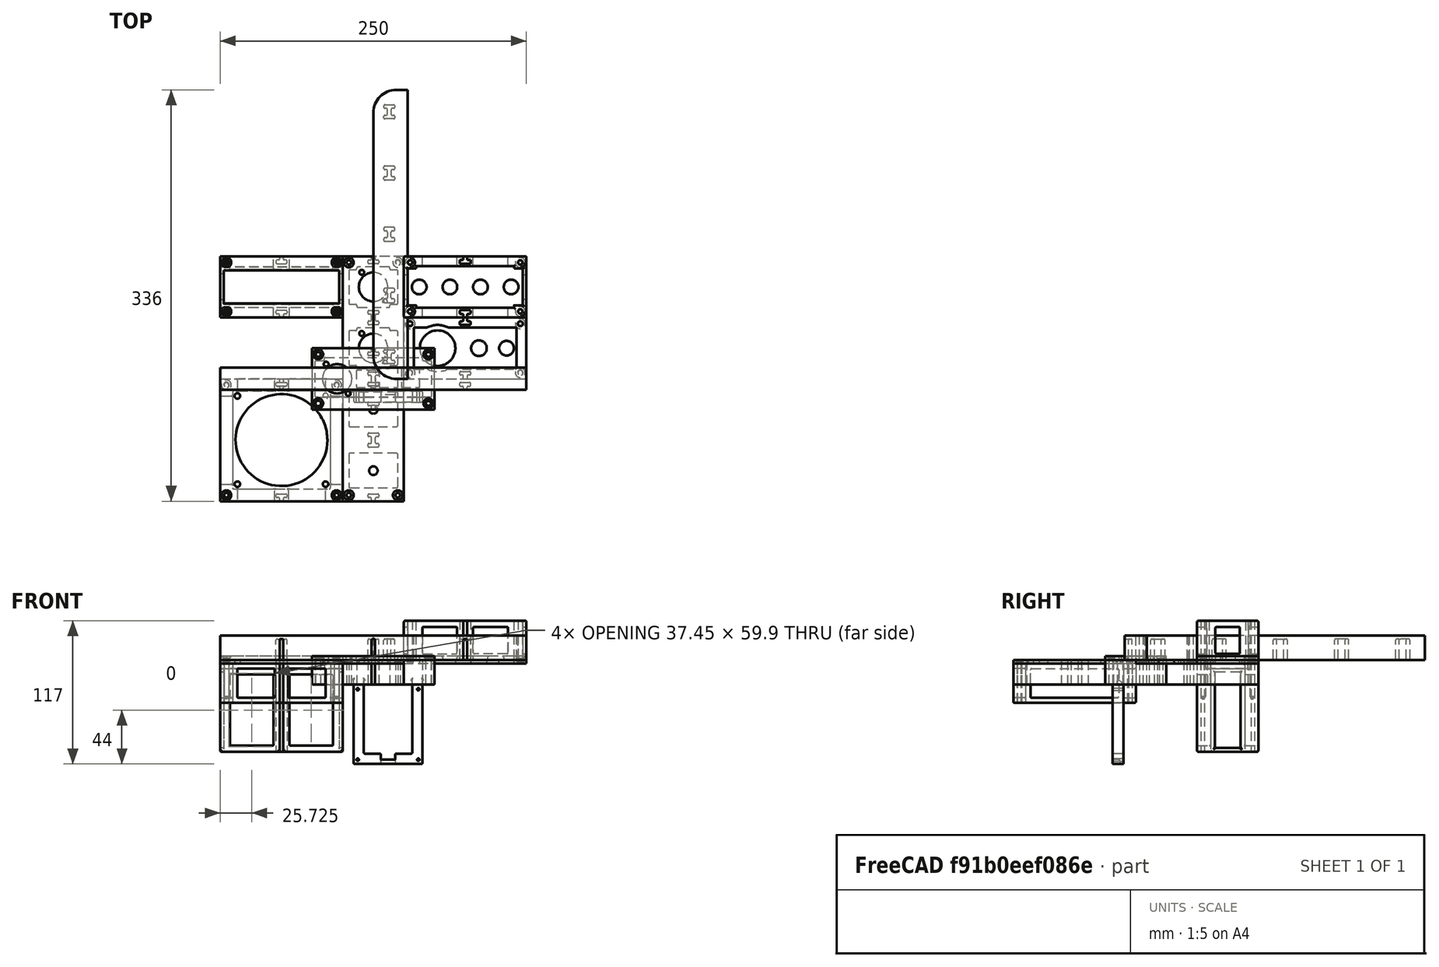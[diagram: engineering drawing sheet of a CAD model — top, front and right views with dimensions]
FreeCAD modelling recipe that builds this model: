
FCSTD DOCUMENT  (FreeCAD 1.2R20260106 (Git shallow))
Label: Rack
License: All rights reserved
LicenseURL: https://en.wikipedia.org/wiki/All_rights_reserved
objects: Sketcher::SketchObject×46, PartDesign::Pocket×35, PartDesign::Pad×20, App::Link×20, PartDesign::Fillet×19, App::Point×15, PartDesign::Body×14, PartDesign::Hole×13, PartDesign::SubShapeBinder×12, App::FeaturePython×3, Assembly::JointGroup×1, Assembly::SimulationGroup×1, Assembly::AssemblyObject×1
note: 379 computed .brp shape members not serialized (recipe doc carries the construction recipe); baked Part::Feature solids carry a one-line shape summary decoded from their .brp
EXTERNAL_REF file=Joints.FCStd obj=Body003
EXTERNAL_REF file=Joints.FCStd obj=Body001
EXTERNAL_REF file=Joints.FCStd obj=Body005
EXTERNAL_REF file=Joints.FCStd obj=Body004

FEATURE [Sketcher::SketchObject] Sketch  label="Master Sketch"
  ArcFitTolerance = 1e-06
  ExternalTypes = [0]
  FullyConstrained = true
  MakeInternals = false
  MapMode = 5
  sketch-geometry (103):
    g0: LineSegment StartX=-125 StartY=100 StartZ=0 EndX=-125 EndY=50 EndZ=0
    g1: LineSegment StartX=-125 StartY=50 StartZ=0 EndX=-25 EndY=50 EndZ=0
    g2: LineSegment StartX=-25 StartY=50 StartZ=0 EndX=-25 EndY=100 EndZ=0
    g3: LineSegment StartX=-25 StartY=100 StartZ=0 EndX=-125 EndY=100 EndZ=0
    g4: LineSegment StartX=-25 StartY=100 StartZ=0 EndX=-25 EndY=-100 EndZ=0
    g5: LineSegment StartX=-25 StartY=-100 StartZ=0 EndX=25 EndY=-100 EndZ=0
    g6: LineSegment StartX=25 StartY=-100 StartZ=0 EndX=25 EndY=100 EndZ=0
    g7: LineSegment StartX=25 StartY=100 StartZ=0 EndX=-25 EndY=100 EndZ=0
    g8: LineSegment StartX=25 StartY=100 StartZ=0 EndX=25 EndY=50 EndZ=0
    g9: LineSegment StartX=25 StartY=50 StartZ=0 EndX=125 EndY=50 EndZ=0
    g10: LineSegment StartX=125 StartY=50 StartZ=0 EndX=125 EndY=100 EndZ=0
    g11: LineSegment StartX=125 StartY=100 StartZ=0 EndX=25 EndY=100 EndZ=0
    g12: LineSegment StartX=-25 StartY=50 StartZ=0 EndX=-125 EndY=50 EndZ=0
    g13: LineSegment StartX=-125 StartY=50 StartZ=0 EndX=-125 EndY=7.1e-15 EndZ=0
    g14: LineSegment StartX=-125 StartY=7.1e-15 StartZ=0 EndX=-25 EndY=7.1e-15 EndZ=0
    g15: LineSegment StartX=-25 StartY=7.1e-15 StartZ=0 EndX=-25 EndY=50 EndZ=0
    g16: LineSegment StartX=125 StartY=50 StartZ=0 EndX=25 EndY=50 EndZ=0
    g17: LineSegment StartX=25 StartY=50 StartZ=0 EndX=25 EndY=7.1e-15 EndZ=0
    g18: LineSegment StartX=25 StartY=7.1e-15 StartZ=0 EndX=125 EndY=7.1e-15 EndZ=0
    g19: LineSegment StartX=125 StartY=7.1e-15 StartZ=0 EndX=125 EndY=50 EndZ=0
    g20: LineSegment StartX=-125 StartY=7.1e-15 StartZ=0 EndX=-125 EndY=-50 EndZ=0
    g21: LineSegment StartX=125 StartY=-50 StartZ=0 EndX=125 EndY=7.1e-15 EndZ=0
    g22: LineSegment StartX=125 StartY=-50 StartZ=0 EndX=25 EndY=-50 EndZ=0
    g23: LineSegment StartX=25 StartY=-50 StartZ=0 EndX=25 EndY=-100 EndZ=0
    g24: LineSegment StartX=-125 StartY=-50 StartZ=0 EndX=-125 EndY=-100 EndZ=0
    g25: LineSegment StartX=-125 StartY=-100 StartZ=0 EndX=-25 EndY=-100 EndZ=0
    g26: LineSegment StartX=-25 StartY=-100 StartZ=0 EndX=-25 EndY=-50 EndZ=0
    g27: LineSegment StartX=-25 StartY=-50 StartZ=0 EndX=-125 EndY=-50 EndZ=0
    g28: LineSegment StartX=125 StartY=-50 StartZ=0 EndX=25 EndY=-50 EndZ=0
    g29: LineSegment StartX=25 StartY=-50 StartZ=0 EndX=25 EndY=-100 EndZ=0
    g30: LineSegment StartX=25 StartY=-100 StartZ=0 EndX=125 EndY=-100 EndZ=0
    g31: LineSegment StartX=125 StartY=-100 StartZ=0 EndX=125 EndY=-50 EndZ=0
    g32: Circle CenterX=-120 CenterY=95 CenterZ=0 NormalX=0 NormalY=0 NormalZ=1 AngleXU=0 Radius=0.825
    g33: Circle CenterX=-30 CenterY=55 CenterZ=0 NormalX=0 NormalY=0 NormalZ=1 AngleXU=0 Radius=0.825
    g34: Circle CenterX=-30 CenterY=95 CenterZ=0 NormalX=0 NormalY=0 NormalZ=1 AngleXU=0 Radius=0.825
    g35: Circle CenterX=-120 CenterY=55 CenterZ=0 NormalX=0 NormalY=0 NormalZ=1 AngleXU=0 Radius=0.825
    g36: LineSegment [constr] StartX=-120 StartY=95 StartZ=0 EndX=-120 EndY=55 EndZ=0
    g37: LineSegment [constr] StartX=-120 StartY=55 StartZ=0 EndX=-30 EndY=55 EndZ=0
    g38: LineSegment [constr] StartX=-30 StartY=55 StartZ=0 EndX=-30 EndY=95 EndZ=0
    g39: LineSegment [constr] StartX=-30 StartY=95 StartZ=0 EndX=-120 EndY=95 EndZ=0
    g40: LineSegment [constr] StartX=-120 StartY=-5 StartZ=0 EndX=-120 EndY=-95 EndZ=0
    g41: LineSegment [constr] StartX=-120 StartY=-95 StartZ=0 EndX=-30 EndY=-95 EndZ=0
    g42: LineSegment [constr] StartX=-30 StartY=-95 StartZ=0 EndX=-30 EndY=-5 EndZ=0
    g43: LineSegment [constr] StartX=-30 StartY=-5 StartZ=0 EndX=-120 EndY=-5 EndZ=0
    g44: Circle CenterX=-120 CenterY=-5 CenterZ=0 NormalX=0 NormalY=0 NormalZ=1 AngleXU=0 Radius=0.825
    g45: Circle CenterX=-30 CenterY=-5 CenterZ=0 NormalX=0 NormalY=0 NormalZ=1 AngleXU=0 Radius=0.825
    g46: Circle CenterX=-30 CenterY=-95 CenterZ=0 NormalX=0 NormalY=0 NormalZ=1 AngleXU=0 Radius=0.825
    g47: Circle CenterX=-120 CenterY=-95 CenterZ=0 NormalX=0 NormalY=0 NormalZ=1 AngleXU=0 Radius=0.825
    g48: LineSegment StartX=-115 StartY=-10 StartZ=0 EndX=-115 EndY=-90 EndZ=0
    g49: LineSegment StartX=-115 StartY=-90 StartZ=0 EndX=-35 EndY=-90 EndZ=0
    g50: LineSegment StartX=-35 StartY=-90 StartZ=0 EndX=-35 EndY=-10 EndZ=0
    g51: LineSegment StartX=-35 StartY=-10 StartZ=0 EndX=-115 EndY=-10 EndZ=0
    g52: GeomPoint X=-75 Y=-50 Z=0
    g53: GeomPoint X=-75 Y=-50 Z=0
    g54: LineSegment [constr] StartX=-111 StartY=-14 StartZ=0 EndX=-111 EndY=-86 EndZ=0
    g55: LineSegment [constr] StartX=-111 StartY=-86 StartZ=0 EndX=-39 EndY=-86 EndZ=0
    g56: LineSegment [constr] StartX=-39 StartY=-86 StartZ=0 EndX=-39 EndY=-14 EndZ=0
    g57: LineSegment [constr] StartX=-39 StartY=-14 StartZ=0 EndX=-111 EndY=-14 EndZ=0
    g58: Circle CenterX=-111 CenterY=-14 CenterZ=0 NormalX=0 NormalY=0 NormalZ=1 AngleXU=0 Radius=2
    g59: Circle CenterX=-39 CenterY=-14 CenterZ=0 NormalX=0 NormalY=0 NormalZ=1 AngleXU=0 Radius=2
    g60: Circle CenterX=-39 CenterY=-86 CenterZ=0 NormalX=0 NormalY=0 NormalZ=1 AngleXU=0 Radius=2
    g61: Circle CenterX=-111 CenterY=-86 CenterZ=0 NormalX=0 NormalY=0 NormalZ=1 AngleXU=0 Radius=2
    g62: Circle CenterX=-75 CenterY=-50 CenterZ=0 NormalX=0 NormalY=0 NormalZ=1 AngleXU=0 Radius=37.5
    g63: GeomPoint X=75 Y=75 Z=0
    g64: LineSegment [constr] StartX=30 StartY=55 StartZ=0 EndX=120 EndY=55 EndZ=0
    g65: LineSegment [constr] StartX=120 StartY=55 StartZ=0 EndX=120 EndY=95 EndZ=0
    g66: LineSegment [constr] StartX=120 StartY=95 StartZ=0 EndX=30 EndY=95 EndZ=0
    g67: LineSegment [constr] StartX=30 StartY=95 StartZ=0 EndX=30 EndY=55 EndZ=0
    g68: GeomPoint [constr] X=75 Y=75 Z=0
    g69: Circle CenterX=30 CenterY=95 CenterZ=0 NormalX=0 NormalY=0 NormalZ=1 AngleXU=0 Radius=0.825
    g70: Circle CenterX=120 CenterY=95 CenterZ=0 NormalX=0 NormalY=0 NormalZ=1 AngleXU=0 Radius=0.825
    g71: Circle CenterX=120 CenterY=55 CenterZ=0 NormalX=0 NormalY=0 NormalZ=1 AngleXU=0 Radius=0.825
    g72: Circle CenterX=30 CenterY=55 CenterZ=0 NormalX=0 NormalY=0 NormalZ=1 AngleXU=0 Radius=0.825
    g73: Circle CenterX=37.5 CenterY=75 CenterZ=0 NormalX=0 NormalY=0 NormalZ=1 AngleXU=0 Radius=6
    g74: LineSegment [constr] StartX=30 StartY=75 StartZ=0 EndX=120 EndY=75 EndZ=0
    g75: Circle CenterX=62.5 CenterY=75 CenterZ=0 NormalX=0 NormalY=0 NormalZ=1 AngleXU=0 Radius=6
    g76: Circle CenterX=87.5 CenterY=75 CenterZ=0 NormalX=0 NormalY=0 NormalZ=1 AngleXU=0 Radius=6
    g77: Circle CenterX=112.5 CenterY=75 CenterZ=0 NormalX=0 NormalY=0 NormalZ=1 AngleXU=0 Radius=6
    g78: LineSegment [constr] StartX=62.5 StartY=55 StartZ=0 EndX=87.5 EndY=55 EndZ=0
    g79: LineSegment [constr] StartX=87.5 StartY=55 StartZ=0 EndX=87.5 EndY=95 EndZ=0
    g80: LineSegment [constr] StartX=87.5 StartY=95 StartZ=0 EndX=62.5 EndY=95 EndZ=0
    g81: LineSegment [constr] StartX=62.5 StartY=95 StartZ=0 EndX=62.5 EndY=55 EndZ=0
    g82: GeomPoint [constr] X=75 Y=75 Z=0
    g83: GeomPoint [constr] X=75 Y=25 Z=0
    g84: LineSegment StartX=30 StartY=5 StartZ=0 EndX=120 EndY=5 EndZ=0
    g85: LineSegment StartX=120 StartY=5 StartZ=0 EndX=120 EndY=45 EndZ=0
    g86: LineSegment StartX=120 StartY=45 StartZ=0 EndX=30 EndY=45 EndZ=0
    g87: LineSegment StartX=30 StartY=45 StartZ=0 EndX=30 EndY=5 EndZ=0
    g88: GeomPoint [constr] X=75 Y=25 Z=0
    g89: LineSegment [constr] StartX=75 StartY=25 StartZ=0 EndX=120 EndY=25 EndZ=0
    g90: LineSegment [constr] StartX=75 StartY=25 StartZ=0 EndX=30 EndY=25 EndZ=0
    g91: LineSegment [constr] StartX=75 StartY=25 StartZ=0 EndX=75 EndY=5 EndZ=0
    g92: LineSegment [constr] StartX=75 StartY=25 StartZ=0 EndX=75 EndY=45 EndZ=0
    g93: Circle CenterX=52.5 CenterY=25 CenterZ=0 NormalX=0 NormalY=0 NormalZ=1 AngleXU=0 Radius=14.5
    g94: Circle CenterX=86.25 CenterY=25 CenterZ=0 NormalX=0 NormalY=0 NormalZ=1 AngleXU=0 Radius=6.375
    g95: Circle CenterX=108.75 CenterY=25 CenterZ=0 NormalX=0 NormalY=0 NormalZ=1 AngleXU=0 Radius=6
    g96: GeomPoint [constr] X=97.5 Y=25 Z=0
    g97: LineSegment [constr] StartX=97.5 StartY=25 StartZ=0 EndX=97.5 EndY=45 EndZ=0
    g98: GeomPoint [constr] X=86.25 Y=35 Z=0
    g99: LineSegment [constr] StartX=86.25 StartY=35 StartZ=0 EndX=86.25 EndY=25 EndZ=0
    g100: GeomPoint [constr] X=108.75 Y=35 Z=0
    g101: LineSegment [constr] StartX=108.75 StartY=35 StartZ=0 EndX=108.75 EndY=25 EndZ=0
    g102: GeomPoint [constr] X=52.5 Y=25 Z=0
  constraints (255):
    c: Coincident(g0,g1)
    c: Coincident(g1,g2)
    c: Coincident(g2,g3)
    c: Coincident(g3,g0)
    c: Vertical(g0)
    c: Vertical(g2)
    c: Horizontal(g1)
    c: Horizontal(g3)
    c: DistanceX(g3,g3) = 100
    c: DistanceY(g0,g0) = 50
    c: Coincident(g4,g5)
    c: Coincident(g5,g6)
    c: Coincident(g6,g7)
    c: Coincident(g7,g4)
    c: Vertical(g4)
    c: Vertical(g6)
    c: Horizontal(g5)
    c: Horizontal(g7)
    c: DistanceY(g6,g6) = 200
    c: DistanceX(g7,g7) = 50
    c: Symmetric(g6,g4,g-1)
    c: Coincident(g2,g4)
    c: Coincident(g8,g9)
    c: Coincident(g9,g10)
    c: Coincident(g10,g11)
    c: Coincident(g11,g8)
    c: Vertical(g8)
    c: Vertical(g10)
    c: Horizontal(g9)
    c: Horizontal(g11)
    c: Coincident(g8,g6)
    c: Equal(g3,g11)
    c: Equal(g0,g10)
    c: Coincident(g12,g13)
    c: Coincident(g13,g14)
    c: Coincident(g14,g15)
    c: Coincident(g15,g12)
    c: Horizontal(g12)
    c: Horizontal(g14)
    c: Vertical(g13)
    c: Vertical(g15)
    c: Coincident(g12,g1)
    c: Equal(g14,g1)
    c: Equal(g13,g0)
    c: Coincident(g16,g17)
    c: Coincident(g17,g18)
    c: Coincident(g18,g19)
    c: Coincident(g19,g16)
    c: Horizontal(g16)
    c: Horizontal(g18)
    c: Vertical(g17)
    c: Vertical(g19)
    c: Coincident(g16,g9)
    c: Equal(g0,g19)
    c: Equal(g14,g18)
    c: Vertical(g20)
    c: Coincident(g20,g13)
    c: Equal(g20,g13)
    c: Vertical(g21)
    c: Coincident(g21,g18)
    c: Coincident(g22,g23)
    c: Horizontal(g22)
    c: Vertical(g23)
    c: Coincident(g22,g21)
    c: Coincident(g23,g5)
    c: Equal(g21,g20)
    c: Coincident(g24,g25)
    c: Coincident(g25,g26)
    c: Coincident(g26,g27)
    c: Coincident(g27,g24)
    c: Vertical(g24)
    c: Vertical(g26)
    c: Horizontal(g25)
    c: Horizontal(g27)
    c: Coincident(g24,g20)
    c: PointOnObject(g25,g4)
    c: Coincident(g28,g29)
    c: Coincident(g29,g30)
    c: Coincident(g30,g31)
    c: Coincident(g31,g28)
    c: Horizontal(g28)
    c: Horizontal(g30)
    c: Vertical(g29)
    c: Vertical(g31)
    c: Coincident(g28,g21)
    c: PointOnObject(g29,g6)
    c: Equal(g31,g21)
    c: Equal(g24,g20)
    c: Diameter(g32) = 1.65
    c: Equal(g32,g34)
    c: Equal(g34,g35)
    c: Equal(g35,g33)
    c: Coincident(g36,g37)
    c: Coincident(g37,g38)
    c: Coincident(g38,g39)
    c: Coincident(g39,g36)
    c: Vertical(g36)
    c: Vertical(g38)
    c: Horizontal(g37)
    c: Horizontal(g39)
    c: Coincident(g36,g32)
    c: Coincident(g36,g35)
    c: Coincident(g37,g33)
    c: Coincident(g38,g34)
    c: Distance(g39,g3) = 5
    c: Distance(g0,g36) = 5
    c: Distance(g1,g37) = 5
    c: Distance(g2,g38) = 5
    c: Coincident(g40,g41)
    c: Coincident(g41,g42)
    c: Coincident(g42,g43)
    c: Coincident(g43,g40)
    c: Vertical(g40)
    c: Vertical(g42)
    c: Horizontal(g41)
    c: Horizontal(g43)
    c: Equal(g43,g39)
    c: Distance(g43,g14) = 5
    c: Distance(g20,g40) = 5
    c: Diameter(g44) = 1.65
    c: Coincident(g44,g40)
    c: Coincident(g45,g42)
    c: Coincident(g46,g41)
    c: Coincident(g47,g40)
    c: Equal(g45,g44)
    c: Equal(g46,g45)
    c: Equal(g47,g46)
    c: Coincident(g48,g49)
    c: Coincident(g49,g50)
    c: Coincident(g50,g51)
    c: Coincident(g51,g48)
    c: Vertical(g48)
    c: Vertical(g50)
    c: Horizontal(g49)
    c: Horizontal(g51)
    c: DistanceX(g51,g51) = 80
    c: Equal(g51,g50)
    c: Distance(g25,g41) = 5
    c: Symmetric(g40,g42,g52)
    c: Symmetric(g48,g50,g53)
    c: Coincident(g52,g53)
    c: Coincident(g54,g55)
    c: Coincident(g55,g56)
    c: Coincident(g56,g57)
    c: Coincident(g57,g54)
    c: Vertical(g54)
    c: Vertical(g56)
    c: Horizontal(g55)
    c: Horizontal(g57)
    c: Distance(g51,g57) = 4
    c: Distance(g48,g54) = 4
    c: Distance(g50,g56) = 4
    c: Distance(g55,g49) = 4
    c: Diameter(g58) = 4
    c: Coincident(g58,g54)
    c: Coincident(g59,g56)
    c: Coincident(g60,g55)
    c: Coincident(g61,g54)
    c: Equal(g58,g59)
    c: Equal(g60,g61)
    c: Equal(g60,g59)
    c: Diameter(g62) = 75
    c: Coincident(g62,g52)
    c: Symmetric(g8,g10,g63)
    c: Coincident(g64,g65)
    c: Coincident(g65,g66)
    c: Coincident(g66,g67)
    c: Coincident(g67,g64)
    c: Horizontal(g64)
    c: Horizontal(g66)
    c: Vertical(g65)
    c: Vertical(g67)
    c: Symmetric(g66,g64,g68)
    c: Coincident(g68,g63)
    c: Distance(g11,g66) = 5
    c: Distance(g10,g65) = 5
    c: Coincident(g69,g66)
    c: Equal(g69,g34)
    c: Coincident(g70,g65)
    c: Coincident(g71,g64)
    c: Coincident(g72,g64)
    c: Equal(g69,g70)
    c: Equal(g70,g71)
    c: Equal(g72,g71)
    c: Diameter(g73) = 12
    c: Horizontal(g74)
    c: PointOnObject(g63,g74)
    c: PointOnObject(g74,g67)
    c: PointOnObject(g74,g65)
    c: PointOnObject(g73,g74)
    c: Diameter(g75) = 12
    c: Diameter(g76) = 12
    c: Diameter(g77) = 12
    c: DistanceX(g73,g75) = 25
    c: DistanceX(g76,g77) = 25
    c: PointOnObject(g75,g74)
    c: PointOnObject(g76,g74)
    c: PointOnObject(g77,g74)
    c: Coincident(g78,g79)
    c: Coincident(g79,g80)
    c: Coincident(g80,g81)
    c: Coincident(g81,g78)
    c: Horizontal(g78)
    c: Horizontal(g80)
    c: Vertical(g79)
    c: Vertical(g81)
    c: Symmetric(g80,g78,g82)
    c: Coincident(g82,g63)
    c: DistanceX(g80,g80) = 25
    c: PointOnObject(g75,g81)
    c: PointOnObject(g76,g79)
    c: PointOnObject(g78,g64)
    c: Symmetric(g17,g9,g83)
    c: Coincident(g84,g85)
    c: Coincident(g85,g86)
    c: Coincident(g86,g87)
    c: Coincident(g87,g84)
    c: Horizontal(g84)
    c: Horizontal(g86)
    c: Vertical(g85)
    c: Vertical(g87)
    c: Symmetric(g86,g84,g88)
    c: Coincident(g88,g83)
    c: Equal(g86,g64)
    c: Equal(g85,g65)
    c: Coincident(g89,g83)
    c: Horizontal(g89)
    c: PointOnObject(g89,g85)
    c: Coincident(g90,g83)
    c: Horizontal(g90)
    c: PointOnObject(g90,g87)
    c: Coincident(g91,g83)
    c: Symmetric(g84,g84,g91)
    c: Coincident(g92,g83)
    c: Vertical(g92)
    c: PointOnObject(g92,g86)
    c: Diameter(g93) = 29
    c: Diameter(g94) = 12.75
    c: Diameter(g95) = 12
    c: Symmetric(g91,g85,g96)
    c: Coincident(g97,g96)
    c: Vertical(g97)
    c: PointOnObject(g97,g86)
    c: Symmetric(g83,g97,g98)
    c: Coincident(g99,g98)
    c: Vertical(g99)
    c: PointOnObject(g99,g89)
    c: Coincident(g94,g99)
    c: Symmetric(g96,g85,g100)
    c: Coincident(g101,g100)
    c: Vertical(g101)
    c: PointOnObject(g101,g89)
    c: Coincident(g95,g101)
    c: Symmetric(g84,g92,g102)
    c: Coincident(g93,g102)
FEATURE [App::Point] Origin001
  Role = Origin
FEATURE [PartDesign::SubShapeBinder] Binder
  BindCopyOnChange = 0
  BindMode = 0
  ClaimChildren = false
  Context = -> Body [Binder.]
  Fuse = false
  MakeFace = true
  OffsetFill = false
  OffsetIntersection = false
  OffsetJoinType = 0
  OffsetOpenResult = false
  PartialLoad = false
  Refine = true
  Relative = true
  Support = -> [Sketch]
  _Version = 2
FEATURE [Sketcher::SketchObject] Sketch001  label="SketchHoles"
  ArcFitTolerance = 1e-06
  AttachmentSupport = -> [Origin]
  ExternalGeometry = -> [Binder]
  ExternalTypes = [0,0,0,0,0,0,0,0]
  FullyConstrained = true
  MakeInternals = false
  MapMode = 5
FEATURE [PartDesign::Pad] Pad
  Direction = (0,0,1)
  Length = 3
  Length2 = 10
  Profile = -> Sketch001
  ReferenceAxis = -> Sketch001 [N_Axis]
  Refine = true
  Reversed = true
  SideType = 0
  Suppressed = false
  Type = 0
  Type2 = 0
FEATURE [PartDesign::Hole] Hole
  BaseFeature = -> Pad
  BaseProfileType = 7
  CustomThreadClearance = 0
  Depth = 3
  DepthType = 0
  Diameter = 4.5
  DrillForDepth = false
  DrillPoint = 1
  DrillPointAngle = 118
  HoleCutCountersinkAngle = 90
  HoleCutCustomValues = false
  HoleCutDepth = 4
  HoleCutDiameter = 8
  HoleCutType = 2
  ModelThread = false
  Profile = -> Pad [Face5,Face6,Face7,Face8]
  Refine = true
  Suppressed = false
  Tapered = false
  TaperedAngle = 90
  ThreadClass = 0
  ThreadDepth = 3
  ThreadDepthType = 0
  ThreadDiameter = 4
  ThreadDirection = 0
  ThreadFit = 0
  ThreadSize = 11
  ThreadType = 1
  Threaded = false
  UseCustomThreadClearance = false
FEATURE [Sketcher::SketchObject] Sketch002  label="SketchInside"
  ArcFitTolerance = 1e-06
  AttachmentSupport = -> [Hole]
  ExternalGeometry = -> [Sketch001,Hole]
  ExternalTypes = [0,0,0,0,0,0,0,0]
  FullyConstrained = true
  MakeInternals = false
  MapMode = 5
  Placement = pos=(0,0,0) rot=(0,1,0;3.14159rad)
  sketch-geometry (17):
    g0: LineSegment StartX=27.95 StartY=84 StartZ=0 EndX=27.95 EndY=66 EndZ=0
    g1: LineSegment StartX=27.95 StartY=66 StartZ=0 EndX=122.05 EndY=66 EndZ=0
    g2: LineSegment StartX=122.05 StartY=66 StartZ=0 EndX=122.05 EndY=84 EndZ=0
    g3: LineSegment StartX=122.05 StartY=84 StartZ=0 EndX=27.95 EndY=84 EndZ=0
    g4: GeomPoint X=75 Y=75 Z=0
    g5: LineSegment [constr] StartX=120 StartY=95 StartZ=0 EndX=120 EndY=55 EndZ=0
    g6: LineSegment [constr] StartX=120 StartY=55 StartZ=0 EndX=30 EndY=55 EndZ=0
    g7: LineSegment [constr] StartX=30 StartY=55 StartZ=0 EndX=30 EndY=95 EndZ=0
    g8: LineSegment [constr] StartX=30 StartY=95 StartZ=0 EndX=120 EndY=95 EndZ=0
    g9: LineSegment StartX=27.95 StartY=88.5 StartZ=0 EndX=27.95 EndY=61.5 EndZ=0
    g10: LineSegment StartX=27.95 StartY=61.5 StartZ=0 EndX=122.05 EndY=61.5 EndZ=0
    g11: LineSegment StartX=122.05 StartY=61.5 StartZ=0 EndX=122.05 EndY=88.5 EndZ=0
    g12: LineSegment StartX=122.05 StartY=88.5 StartZ=0 EndX=27.95 EndY=88.5 EndZ=0
    g13: LineSegment StartX=25 StartY=91.5 StartZ=0 EndX=125 EndY=91.5 EndZ=0
    g14: LineSegment StartX=125 StartY=91.5 StartZ=0 EndX=125 EndY=58.5 EndZ=0
    g15: LineSegment StartX=125 StartY=58.5 StartZ=0 EndX=25 EndY=58.5 EndZ=0
    g16: LineSegment StartX=25 StartY=58.5 StartZ=0 EndX=25 EndY=91.5 EndZ=0
  constraints (44):
    c: Coincident(g0,g1)
    c: Coincident(g1,g2)
    c: Coincident(g2,g3)
    c: Coincident(g3,g0)
    c: Vertical(g0)
    c: Vertical(g2)
    c: Horizontal(g1)
    c: Horizontal(g3)
    c: DistanceX(g3,g3) = 94.1
    c: DistanceY(g0,g0) = 18
    c: Symmetric(g0,g2,g4)
    c: Coincident(g5,g6)
    c: Coincident(g6,g7)
    c: Coincident(g7,g8)
    c: Coincident(g8,g5)
    c: Vertical(g5)
    c: Vertical(g7)
    c: Horizontal(g6)
    c: Horizontal(g8)
    c: Coincident(g5,g-7)
    c: Coincident(g6,g-10)
    c: Symmetric(g5,g7,g4)
    c: Coincident(g9,g10)
    c: Coincident(g10,g11)
    c: Coincident(g11,g12)
    c: Coincident(g12,g9)
    c: Vertical(g9)
    c: Vertical(g11)
    c: Horizontal(g10)
    c: Horizontal(g12)
    c: Symmetric(g9,g10,g4)
    c: DistanceY(g11,g11) = 27
    c: Equal(g12,g3)
    c: Coincident(g13,g14)
    c: Coincident(g14,g15)
    c: Coincident(g15,g16)
    c: Coincident(g16,g13)
    c: Horizontal(g13)
    c: Horizontal(g15)
    c: Vertical(g14)
    c: Vertical(g16)
    c: Symmetric(g13,g14,g4)
    c: Distance(g12,g13) = 3
    c: Equal(g13,g-3)
FEATURE [PartDesign::Pocket] Pocket
  BaseFeature = -> Hole
  Direction = (0,0,1)
  Length = 3
  Length2 = 5
  Profile = -> Sketch002 [Edge3,Edge2,Edge1,Edge4]
  ReferenceAxis = -> Sketch002 [N_Axis]
  Refine = true
  Reversed = true
  SideType = 0
  Suppressed = false
  Type = 0
  Type2 = 0
FEATURE [PartDesign::Pad] Pad001
  BaseFeature = -> Pocket
  Direction = (0,0,-1)
  Length = 10
  Length2 = 10
  Profile = -> Sketch002 [Edge7,Edge8,Edge5,Edge6,Edge11,Edge12,Edge9,Edge10]
  ReferenceAxis = -> Sketch002 [N_Axis]
  Refine = true
  SideType = 0
  Suppressed = false
  Type = 0
  Type2 = 0
FEATURE [Sketcher::SketchObject] Sketch003
  ArcFitTolerance = 1e-06
  AttachmentSupport = -> [Pad001]
  ExternalGeometry = -> [Sketch002]
  ExternalTypes = [0,0,0,0,0,0]
  FullyConstrained = true
  MakeInternals = false
  MapMode = 5
  Placement = pos=(0,0,-3) rot=(1,0,0;3.14159rad)
  sketch-geometry (8):
    g0: LineSegment StartX=-122.05 StartY=-61.5 StartZ=0 EndX=-122.05 EndY=-66 EndZ=0
    g1: LineSegment StartX=-122.05 StartY=-66 StartZ=0 EndX=-27.95 EndY=-66 EndZ=0
    g2: LineSegment StartX=-27.95 StartY=-66 StartZ=0 EndX=-27.95 EndY=-61.5 EndZ=0
    g3: LineSegment StartX=-27.95 StartY=-61.5 StartZ=0 EndX=-122.05 EndY=-61.5 EndZ=0
    g4: LineSegment StartX=-122.05 StartY=-84 StartZ=0 EndX=-122.05 EndY=-88.5 EndZ=0
    g5: LineSegment StartX=-122.05 StartY=-88.5 StartZ=0 EndX=-27.95 EndY=-88.5 EndZ=0
    g6: LineSegment StartX=-27.95 StartY=-88.5 StartZ=0 EndX=-27.95 EndY=-84 EndZ=0
    g7: LineSegment StartX=-27.95 StartY=-84 StartZ=0 EndX=-122.05 EndY=-84 EndZ=0
  constraints (20):
    c: Coincident(g0,g1)
    c: Coincident(g1,g2)
    c: Coincident(g2,g3)
    c: Coincident(g3,g0)
    c: Vertical(g0)
    c: Vertical(g2)
    c: Horizontal(g1)
    c: Horizontal(g3)
    c: Coincident(g0,g-4)
    c: Coincident(g1,g-7)
    c: Coincident(g4,g5)
    c: Coincident(g5,g6)
    c: Coincident(g6,g7)
    c: Coincident(g7,g4)
    c: Vertical(g4)
    c: Vertical(g6)
    c: Horizontal(g5)
    c: Horizontal(g7)
    c: Coincident(g4,g-8)
    c: Coincident(g5,g-6)
FEATURE [PartDesign::Pocket] Pocket001
  BaseFeature = -> Pad001
  Direction = (0,0,1)
  Length = 2
  Length2 = 5
  Profile = -> Sketch003
  ReferenceAxis = -> Sketch003 [N_Axis]
  Refine = true
  SideType = 0
  Suppressed = false
  Type = 3
  Type2 = 0
  UpToFace = -> Pad001 [Face28]
FEATURE [PartDesign::Body] Body  label="Switch Top"
  AllowCompound = true
  Group = -> [Binder,Sketch001,Pad,Hole,Sketch002,Pocket,Pad001,Sketch003,Pocket001]
  Origin = -> Origin
  Placement = pos=(0,0,3) rot=(0,0,1;0rad)
  Tip = -> Pocket001
FEATURE [App::Point] Origin003
  Role = Origin
FEATURE [PartDesign::SubShapeBinder] Binder001
  BindCopyOnChange = 0
  BindMode = 0
  ClaimChildren = false
  Context = -> Body001 [Binder001.]
  Fuse = false
  MakeFace = true
  OffsetFill = false
  OffsetIntersection = false
  OffsetJoinType = 0
  OffsetOpenResult = false
  PartialLoad = false
  Refine = true
  Relative = true
  Support = -> [Sketch]
  _Version = 2
FEATURE [Sketcher::SketchObject] Sketch004
  ArcFitTolerance = 1e-06
  AttachmentSupport = -> [Origin002]
  ExternalGeometry = -> [Binder001]
  ExternalTypes = [0,0,0,0,0,0,0,0,0]
  FullyConstrained = true
  MakeInternals = false
  MapMode = 5
  sketch-geometry (1):
    g0: LineSegment StartX=-25 StartY=0 StartZ=0 EndX=-25 EndY=-100 EndZ=0
  constraints (2):
    c: Coincident(g0,g-4)
    c: Coincident(g0,g-6)
FEATURE [PartDesign::Pad] Pad002
  Direction = (0,0,1)
  Length = 3
  Length2 = 10
  Profile = -> Sketch004
  ReferenceAxis = -> Sketch004 [N_Axis]
  Refine = true
  Reversed = true
  SideType = 0
  Suppressed = false
  Type = 0
  Type2 = 0
FEATURE [PartDesign::Hole] Hole001  label="HolesOutside"
  BaseFeature = -> Pad002
  BaseProfileType = 7
  CustomThreadClearance = 0
  Depth = 10
  DepthType = 0
  Diameter = 4.5
  DrillForDepth = false
  DrillPoint = 1
  DrillPointAngle = 118
  HoleCutCountersinkAngle = 90
  HoleCutCustomValues = false
  HoleCutDepth = 4
  HoleCutDiameter = 8
  HoleCutType = 2
  ModelThread = false
  Profile = -> Pad002 [Face8,Face7,Face6,Face5]
  Refine = true
  Suppressed = false
  Tapered = false
  TaperedAngle = 90
  ThreadClass = 0
  ThreadDepth = 10
  ThreadDepthType = 0
  ThreadDiameter = 4
  ThreadDirection = 0
  ThreadFit = 0
  ThreadSize = 11
  ThreadType = 1
  Threaded = false
  UseCustomThreadClearance = false
FEATURE [PartDesign::Hole] Hole002  label="HolesInside"
  BaseFeature = -> Hole001
  BaseProfileType = 7
  CustomThreadClearance = 0
  Depth = 3
  DepthType = 0
  Diameter = 4.5
  DrillForDepth = false
  DrillPoint = 1
  DrillPointAngle = 118
  HoleCutCountersinkAngle = 90
  HoleCutCustomValues = false
  HoleCutDepth = 0
  HoleCutDiameter = 0
  HoleCutType = 0
  ModelThread = false
  Profile = -> Binder001 [Edge45,Edge46,Edge47,Edge48]
  Refine = true
  Suppressed = false
  Tapered = false
  TaperedAngle = 90
  ThreadClass = 0
  ThreadDepth = 3
  ThreadDepthType = 0
  ThreadDiameter = 4
  ThreadDirection = 0
  ThreadFit = 0
  ThreadSize = 11
  ThreadType = 1
  Threaded = false
  UseCustomThreadClearance = false
FEATURE [PartDesign::Pocket] Pocket002
  BaseFeature = -> Hole002
  Direction = (0,0,-1)
  Length = 5
  Length2 = 5
  Profile = -> Binder001 [Edge49]
  Refine = true
  SideType = 0
  Suppressed = false
  Type = 0
  Type2 = 0
FEATURE [Sketcher::SketchObject] Sketch005  label="SketchBottomInner"
  ArcFitTolerance = 1e-06
  AttachmentSupport = -> [Pocket002]
  ExternalGeometry = -> [Binder001]
  ExternalTypes = [0,0,0,0]
  FullyConstrained = true
  MakeInternals = false
  MapMode = 5
  Placement = pos=(0,0,-3) rot=(1,0,0;3.14159rad)
FEATURE [App::Point] Origin005  label="Origin006"
  Role = Origin
FEATURE [PartDesign::SubShapeBinder] Binder002
  BindCopyOnChange = 0
  BindMode = 0
  ClaimChildren = false
  Context = -> Body002 [Pad003.Binder002.]
  Fuse = false
  MakeFace = true
  OffsetFill = false
  OffsetIntersection = false
  OffsetJoinType = 0
  OffsetOpenResult = false
  PartialLoad = false
  Refine = true
  Relative = true
  Support = -> [Sketch,Binder003]
  _Version = 2
FEATURE [PartDesign::Pad] Pad003  label="PadBody"
  Direction = (0,0,1)
  Length = 75
  Length2 = 10
  Profile = -> Binder002 [Edge52,Edge27,Edge55,Edge54,Edge25,Edge21,Edge56,Edge53]
  Refine = true
  Reversed = true
  SideType = 0
  Suppressed = false
  Type = 0
  Type2 = 0
FEATURE [PartDesign::SubShapeBinder] Binder003
  BindCopyOnChange = 0
  BindMode = 0
  ClaimChildren = false
  Context = -> Body002 [Binder003.]
  Fuse = false
  MakeFace = true
  OffsetFill = false
  OffsetIntersection = false
  OffsetJoinType = 0
  OffsetOpenResult = false
  PartialLoad = false
  Refine = true
  Relative = true
  Support = -> [Body[Sketch002.]]
  _Version = 2
FEATURE [Sketcher::SketchObject] Sketch006  label="SketchInside001"
  ArcFitTolerance = 1e-06
  AttachmentSupport = -> [Pad003]
  ExternalGeometry = -> [Binder003]
  ExternalTypes = [0,0,0,0,0,0,0,0]
  FullyConstrained = true
  MakeInternals = false
  MapMode = 5
  sketch-geometry (4):
    g0: LineSegment StartX=-122.05 StartY=88.5 StartZ=0 EndX=-122.05 EndY=61.5 EndZ=0
    g1: LineSegment StartX=-122.05 StartY=61.5 StartZ=0 EndX=-27.95 EndY=61.5 EndZ=0
    g2: LineSegment StartX=-27.95 StartY=61.5 StartZ=0 EndX=-27.95 EndY=88.5 EndZ=0
    g3: LineSegment StartX=-27.95 StartY=88.5 StartZ=0 EndX=-122.05 EndY=88.5 EndZ=0
  constraints (10):
    c: Coincident(g0,g1)
    c: Coincident(g1,g2)
    c: Coincident(g2,g3)
    c: Coincident(g3,g0)
    c: Vertical(g0)
    c: Vertical(g2)
    c: Horizontal(g1)
    c: Horizontal(g3)
    c: Coincident(g0,g-5)
    c: Coincident(g1,g-9)
FEATURE [PartDesign::Pocket] Pocket004  label="PocketInner"
  BaseFeature = -> Pad003
  Direction = (0,0,-1)
  Length = 82
  Length2 = 5
  Profile = -> Sketch006
  ReferenceAxis = -> Sketch006 [N_Axis]
  Refine = true
  SideType = 0
  Suppressed = false
  Type = 0
  Type2 = 0
FEATURE [Sketcher::SketchObject] Sketch007
  ArcFitTolerance = 1e-06
  AttachmentOffset = pos=(0,-3,0) rot=(0,0,1;0rad)
  AttachmentSupport = -> [Pocket004,Pad003]
  ExternalGeometry = -> [Binder003,Binder002]
  ExternalTypes = [0,0,0]
  FullyConstrained = true
  MakeInternals = false
  MapMode = 5
  Placement = pos=(-125,0,-3) rot=(0.57735,-0.57735,-0.57735;2.0944rad)
  sketch-geometry (6):
    g0: LineSegment StartX=-91.5 StartY=3 StartZ=0 EndX=-91.5 EndY=-4 EndZ=0
    g1: LineSegment StartX=-91.5 StartY=-4 StartZ=0 EndX=-58.5 EndY=-4 EndZ=0
    g2: LineSegment StartX=-58.5 StartY=-4 StartZ=0 EndX=-58.5 EndY=3 EndZ=0
    g3: LineSegment StartX=-58.5 StartY=3 StartZ=0 EndX=-91.5 EndY=3 EndZ=0
    g4: LineSegment [constr] StartX=-91.5 StartY=6 StartZ=0 EndX=-91.5 EndY=3 EndZ=0
    g5: LineSegment [constr] StartX=-58.5 StartY=6 StartZ=0 EndX=-58.5 EndY=3 EndZ=0
  constraints (16):
    c: Vertical(g0)
    c: Vertical(g2)
    c: Horizontal(g1)
    c: DistanceY(g2,g2) = 7
    c: Coincident(g4,g-3)
    c: PointOnObject(g4,g-5)
    c: Vertical(g4)
    c: Coincident(g5,g-4)
    c: PointOnObject(g5,g-5)
    c: Vertical(g5)
    c: Coincident(g3,g4)
    c: Coincident(g3,g5)
    c: Coincident(g0,g1)
    c: Coincident(g1,g2)
    c: Coincident(g0,g3)
    c: Coincident(g2,g3)
FEATURE [PartDesign::Pocket] Pocket005  label="PocketKnotch"
  BaseFeature = -> Pocket004
  Direction = (1,0,0)
  Length = 5
  Length2 = 5
  Offset = -3
  Profile = -> Sketch007
  ReferenceAxis = -> Sketch007 [N_Axis]
  Refine = true
  SideType = 0
  Suppressed = false
  Type = 1
  Type2 = 0
FEATURE [PartDesign::Pocket] Pocket006  label="PocketTopTolerance"
  BaseFeature = -> Pocket005
  Direction = (0,1,0)
  Length = 0.575
  Length2 = 5
  Profile = -> Pocket005 [Face18]
  Refine = true
  SideType = 0
  Suppressed = false
  Type = 0
  Type2 = 0
  expr: Length = (27.15 - 26) / 2
FEATURE [PartDesign::Pocket] Pocket007  label="PocketBottomTolerance"
  BaseFeature = -> Pocket006
  Direction = (0,-1,0)
  Length = 0.575
  Length2 = 5
  Profile = -> Pocket006 [Face15]
  Refine = true
  SideType = 0
  Suppressed = false
  Type = 0
  Type2 = 0
  expr: Length = (27.15 - 26) / 2
FEATURE [Sketcher::SketchObject] Sketch008  label="SketchJointFemale"
  ArcFitTolerance = 1e-06
  AttachmentSupport = -> [Pocket007]
  ExternalGeometry = -> [Pocket007]
  ExternalTypes = [0,0,0,0]
  FullyConstrained = true
  MakeInternals = false
  MapMode = 5
  sketch-geometry (26):
    g0: LineSegment StartX=-76.5 StartY=100 StartZ=0 EndX=-76.5 EndY=97 EndZ=0
    g1: LineSegment StartX=-76.5 StartY=97 StartZ=0 EndX=-79.5 EndY=97 EndZ=0
    g2: LineSegment StartX=-79.5 StartY=97 StartZ=0 EndX=-79.5 EndY=94 EndZ=0
    g3: LineSegment StartX=-79.5 StartY=94 StartZ=0 EndX=-70.5 EndY=94 EndZ=0
    g4: LineSegment StartX=-70.5 StartY=94 StartZ=0 EndX=-70.5 EndY=97 EndZ=0
    g5: LineSegment StartX=-70.5 StartY=97 StartZ=0 EndX=-73.5 EndY=97 EndZ=0
    g6: LineSegment StartX=-73.5 StartY=97 StartZ=0 EndX=-73.5 EndY=100 EndZ=0
    g7: LineSegment StartX=-73.5 StartY=100 StartZ=0 EndX=-76.5 EndY=100 EndZ=0
    g8: GeomPoint [constr] X=-75 Y=95.5 Z=0
    g9: LineSegment [constr] StartX=-75 StartY=91 StartZ=0 EndX=-75 EndY=100 EndZ=0
    g10: LineSegment [constr] StartX=-75 StartY=100 StartZ=0 EndX=-76.5 EndY=100 EndZ=0
    g11: LineSegment [constr] StartX=-76.5 StartY=100 StartZ=0 EndX=-76.5 EndY=97 EndZ=0
    g12: LineSegment [constr] StartX=-76.5 StartY=97 StartZ=0 EndX=-75 EndY=97 EndZ=0
    g13: LineSegment [constr] StartX=-75 StartY=97 StartZ=0 EndX=-75 EndY=100 EndZ=0
    g14: LineSegment [constr] StartX=-75 StartY=100 StartZ=0 EndX=-75 EndY=97 EndZ=0
    g15: LineSegment [constr] StartX=-75 StartY=97 StartZ=0 EndX=-73.5 EndY=97 EndZ=0
    g16: LineSegment [constr] StartX=-73.5 StartY=97 StartZ=0 EndX=-73.5 EndY=100 EndZ=0
    g17: LineSegment [constr] StartX=-73.5 StartY=100 StartZ=0 EndX=-75 EndY=100 EndZ=0
    g18: LineSegment [constr] StartX=-73.5 StartY=97 StartZ=0 EndX=-73.5 EndY=94 EndZ=0
    g19: LineSegment [constr] StartX=-73.5 StartY=94 StartZ=0 EndX=-70.5 EndY=94 EndZ=0
    g20: LineSegment [constr] StartX=-70.5 StartY=94 StartZ=0 EndX=-70.5 EndY=97 EndZ=0
    g21: LineSegment [constr] StartX=-70.5 StartY=97 StartZ=0 EndX=-73.5 EndY=97 EndZ=0
    g22: LineSegment [constr] StartX=-76.5 StartY=97 StartZ=0 EndX=-79.5 EndY=97 EndZ=0
    g23: LineSegment [constr] StartX=-79.5 StartY=97 StartZ=0 EndX=-79.5 EndY=94 EndZ=0
    g24: LineSegment [constr] StartX=-79.5 StartY=94 StartZ=0 EndX=-76.5 EndY=94 EndZ=0
    g25: LineSegment [constr] StartX=-76.5 StartY=94 StartZ=0 EndX=-76.5 EndY=97 EndZ=0
  constraints (65):
    c: Symmetric(g-5,g-6,g8)
    c: Vertical(g9)
    c: PointOnObject(g8,g9)
    c: PointOnObject(g9,g-3)
    c: PointOnObject(g9,g-5)
    c: Coincident(g10,g11)
    c: Coincident(g11,g12)
    c: Coincident(g12,g13)
    c: Coincident(g13,g10)
    c: Horizontal(g10)
    c: Horizontal(g12)
    c: Vertical(g11)
    c: Vertical(g13)
    c: Coincident(g10,g9)
    c: Coincident(g14,g15)
    c: Coincident(g15,g16)
    c: Coincident(g16,g17)
    c: Coincident(g17,g14)
    c: Vertical(g14)
    c: Vertical(g16)
    c: Horizontal(g15)
    c: Horizontal(g17)
    c: Coincident(g14,g9)
    c: DistanceX(g10,g10) = 1.5
    c: Equal(g10,g17)
    c: DistanceY(g16,g16) = 3
    c: Equal(g11,g16)
    c: Coincident(g18,g19)
    c: Coincident(g19,g20)
    c: Coincident(g20,g21)
    c: Coincident(g21,g18)
    c: Vertical(g18)
    c: Vertical(g20)
    c: Horizontal(g19)
    c: Horizontal(g21)
    c: Coincident(g18,g15)
    c: Coincident(g22,g23)
    c: Coincident(g23,g24)
    c: Coincident(g24,g25)
    c: Coincident(g25,g22)
    c: Horizontal(g22)
    c: Horizontal(g24)
    c: Vertical(g23)
    c: Vertical(g25)
    c: Coincident(g22,g11)
    c: Equal(g21,g16)
    c: Equal(g20,g21)
    c: Equal(g23,g18)
    c: Equal(g22,g23)
    c: Coincident(g10,g7)
    c: Coincident(g7,g16)
    c: Coincident(g0,g7)
    c: Coincident(g0,g11)
    c: Coincident(g1,g0)
    c: Coincident(g1,g22)
    c: Coincident(g2,g1)
    c: Coincident(g2,g23)
    c: Coincident(g3,g2)
    c: Coincident(g3,g19)
    c: Coincident(g4,g3)
    c: Coincident(g4,g20)
    c: Coincident(g5,g4)
    c: Coincident(g5,g15)
    c: Coincident(g6,g7)
    c: Coincident(g6,g5)
FEATURE [PartDesign::Pocket] Pocket008  label="JointFemale"
  BaseFeature = -> Pocket007
  Direction = (0,0,-1)
  Length = 67
  Length2 = 5
  Profile = -> Sketch008
  ReferenceAxis = -> Sketch008 [N_Axis]
  Refine = true
  SideType = 0
  Suppressed = false
  Type = 3
  Type2 = 0
  UpToFace = -> Pocket007 [Face5]
FEATURE [Sketcher::SketchObject] Sketch009  label="SketchJointFemale001"
  ArcFitTolerance = 1e-06
  AttachmentSupport = -> [Pocket008]
  ExternalGeometry = -> [Sketch008,Binder003]
  ExternalTypes = [0,0,0,0,0,0,0,0,0,0,0,0]
  FullyConstrained = true
  MakeInternals = false
  MapMode = 5
  sketch-geometry (26):
    g0: GeomPoint [constr] X=-75 Y=54.25 Z=0
    g1: LineSegment [constr] StartX=-75 StartY=54.25 StartZ=0 EndX=-75 EndY=50 EndZ=0
    g2: LineSegment [constr] StartX=-75 StartY=50 StartZ=0 EndX=-73.5 EndY=50 EndZ=0
    g3: LineSegment [constr] StartX=-73.5 StartY=50 StartZ=0 EndX=-73.5 EndY=53 EndZ=0
    g4: LineSegment [constr] StartX=-73.5 StartY=53 StartZ=0 EndX=-75 EndY=53 EndZ=0
    g5: LineSegment [constr] StartX=-75 StartY=53 StartZ=0 EndX=-75 EndY=50 EndZ=0
    g6: LineSegment [constr] StartX=-75 StartY=50 StartZ=0 EndX=-75 EndY=53 EndZ=0
    g7: LineSegment [constr] StartX=-75 StartY=53 StartZ=0 EndX=-76.5 EndY=53 EndZ=0
    g8: LineSegment [constr] StartX=-76.5 StartY=53 StartZ=0 EndX=-76.5 EndY=50 EndZ=0
    g9: LineSegment [constr] StartX=-76.5 StartY=50 StartZ=0 EndX=-75 EndY=50 EndZ=0
    g10: LineSegment [constr] StartX=-76.5 StartY=53 StartZ=0 EndX=-76.5 EndY=56 EndZ=0
    g11: LineSegment [constr] StartX=-76.5 StartY=56 StartZ=0 EndX=-79.5 EndY=56 EndZ=0
    g12: LineSegment [constr] StartX=-79.5 StartY=56 StartZ=0 EndX=-79.5 EndY=53 EndZ=0
    g13: LineSegment [constr] StartX=-79.5 StartY=53 StartZ=0 EndX=-76.5 EndY=53 EndZ=0
    g14: LineSegment [constr] StartX=-73.5 StartY=53 StartZ=0 EndX=-70.5 EndY=53 EndZ=0
    g15: LineSegment [constr] StartX=-70.5 StartY=53 StartZ=0 EndX=-70.5 EndY=56 EndZ=0
    g16: LineSegment [constr] StartX=-70.5 StartY=56 StartZ=0 EndX=-73.5 EndY=56 EndZ=0
    g17: LineSegment [constr] StartX=-73.5 StartY=56 StartZ=0 EndX=-73.5 EndY=53 EndZ=0
    g18: LineSegment StartX=-79.5 StartY=56 StartZ=0 EndX=-79.5 EndY=53 EndZ=0
    g19: LineSegment StartX=-79.5 StartY=53 StartZ=0 EndX=-76.5 EndY=53 EndZ=0
    g20: LineSegment StartX=-76.5 StartY=53 StartZ=0 EndX=-76.5 EndY=50 EndZ=0
    g21: LineSegment StartX=-76.5 StartY=50 StartZ=0 EndX=-73.5 EndY=50 EndZ=0
    g22: LineSegment StartX=-73.5 StartY=50 StartZ=0 EndX=-73.5 EndY=53 EndZ=0
    g23: LineSegment StartX=-73.5 StartY=53 StartZ=0 EndX=-70.5 EndY=53 EndZ=0
    g24: LineSegment StartX=-70.5 StartY=53 StartZ=0 EndX=-70.5 EndY=56 EndZ=0
    g25: LineSegment StartX=-70.5 StartY=56 StartZ=0 EndX=-79.5 EndY=56 EndZ=0
  constraints (63):
    c: Symmetric(g-12,g-13,g0)
    c: Coincident(g1,g0)
    c: Symmetric(g-11,g-11,g1)
    c: Coincident(g2,g3)
    c: Coincident(g3,g4)
    c: Coincident(g4,g5)
    c: Coincident(g5,g2)
    c: Horizontal(g2)
    c: Horizontal(g4)
    c: Vertical(g3)
    c: Vertical(g5)
    c: Coincident(g2,g1)
    c: Coincident(g6,g7)
    c: Coincident(g7,g8)
    c: Coincident(g8,g9)
    c: Coincident(g9,g6)
    c: Vertical(g6)
    c: Vertical(g8)
    c: Horizontal(g7)
    c: Horizontal(g9)
    c: Coincident(g6,g1)
    c: DistanceX(g9,g9) = 1.5
    c: Equal(g2,g9)
    c: DistanceY(g8,g8) = 3
    c: Equal(g8,g3)
    c: Coincident(g10,g11)
    c: Coincident(g11,g12)
    c: Coincident(g12,g13)
    c: Coincident(g13,g10)
    c: Vertical(g10)
    c: Vertical(g12)
    c: Horizontal(g11)
    c: Horizontal(g13)
    c: Distance(g10,g12) = 3
    c: Distance(g11,g13) = 3
    c: Coincident(g10,g7)
    c: Coincident(g14,g15)
    c: Coincident(g15,g16)
    c: Coincident(g16,g17)
    c: Coincident(g17,g14)
    c: Horizontal(g14)
    c: Horizontal(g16)
    c: Vertical(g15)
    c: Vertical(g17)
    c: Coincident(g14,g3)
    c: Equal(g12,g17)
    c: Equal(g14,g13)
    c: Coincident(g18,g11)
    c: Coincident(g18,g12)
    c: Coincident(g19,g12)
    c: Coincident(g19,g7)
    c: Coincident(g20,g7)
    c: Coincident(g20,g8)
    c: Coincident(g21,g8)
    c: Coincident(g21,g2)
    c: Coincident(g22,g2)
    c: Coincident(g22,g3)
    c: Coincident(g23,g3)
    c: Coincident(g23,g14)
    c: Coincident(g24,g14)
    c: Coincident(g24,g15)
    c: Coincident(g25,g15)
    c: Coincident(g25,g11)
FEATURE [PartDesign::Pocket] Pocket009  label="PocketBottomJoint"
  BaseFeature = -> Pocket008
  Direction = (0,0,-1)
  Length = 67
  Length2 = 5
  Profile = -> Sketch009
  ReferenceAxis = -> Sketch009 [N_Axis]
  Refine = true
  SideType = 0
  Suppressed = false
  Type = 3
  Type2 = 0
  UpToFace = -> Pocket008 [Face4]
FEATURE [PartDesign::Hole] Hole003  label="HoleScrews"
  BaseFeature = -> Pocket009
  BaseProfileType = 7
  CustomThreadClearance = 0
  Depth = 30
  DepthType = 0
  Diameter = 3.7
  DrillForDepth = false
  DrillPoint = 1
  DrillPointAngle = 118
  HoleCutCountersinkAngle = 90
  HoleCutCustomValues = false
  HoleCutDepth = 0
  HoleCutDiameter = 0
  HoleCutType = 0
  ModelThread = false
  Profile = -> Binder002 [Edge53,Edge54,Edge56,Edge55]
  Refine = true
  Suppressed = false
  Tapered = false
  TaperedAngle = 90
  ThreadClass = 0
  ThreadDepth = 30
  ThreadDepthType = 0
  ThreadDiameter = 4.5
  ThreadDirection = 0
  ThreadFit = 0
  ThreadSize = 12
  ThreadType = 1
  Threaded = true
  UseCustomThreadClearance = false
FEATURE [App::Point] Origin007  label="Origin009"
  Role = Origin
FEATURE [App::Point] Origin009  label="Origin011"
  Role = Origin
FEATURE [PartDesign::SubShapeBinder] Binder008
  BindCopyOnChange = 0
  BindMode = 0
  ClaimChildren = false
  Context = -> Body003 [Binder008.]
  Fuse = false
  MakeFace = true
  OffsetFill = false
  OffsetIntersection = false
  OffsetJoinType = 0
  OffsetOpenResult = false
  PartialLoad = false
  Refine = true
  Relative = true
  Support = -> [Sketch]
  _Version = 2
FEATURE [Sketcher::SketchObject] Sketch012  label="SketchFanBottom"
  ArcFitTolerance = 1e-06
  AttachmentSupport = -> [Origin008]
  ExternalGeometry = -> [Binder008]
  ExternalTypes = [0,0,0,0,0,0,0,0,0,0,0,0,0]
  FullyConstrained = true
  MakeInternals = false
  MapMode = 5
  sketch-geometry (1):
    g0: LineSegment StartX=-25 StartY=0 StartZ=0 EndX=-25 EndY=-100 EndZ=0
  constraints (2):
    c: Coincident(g0,g-3)
    c: Coincident(g0,g-5)
FEATURE [PartDesign::Pad] Pad005  label="PadBody001"
  Direction = (0,0,1)
  Length = 32
  Length2 = 10
  Profile = -> Sketch012 [Edge4,Edge5,Edge3,Edge2,Edge1,Edge8,Edge7,Edge6,Edge9]
  ReferenceAxis = -> Sketch012 [N_Axis]
  Refine = true
  Reversed = true
  SideType = 0
  Suppressed = false
  Type = 0
  Type2 = 0
FEATURE [PartDesign::Hole] Hole004  label="HoleScrews001"
  BaseFeature = -> Pad005
  BaseProfileType = 7
  CustomThreadClearance = 0
  Depth = 292.893
  DepthType = 1
  Diameter = 3.7
  DrillForDepth = false
  DrillPoint = 1
  DrillPointAngle = 118
  HoleCutCountersinkAngle = 90
  HoleCutCustomValues = false
  HoleCutDepth = 0
  HoleCutDiameter = 0
  HoleCutType = 0
  ModelThread = false
  Profile = -> Sketch012 [Edge13,Edge10,Edge11,Edge12]
  Refine = true
  Suppressed = false
  Tapered = false
  TaperedAngle = 90
  ThreadClass = 0
  ThreadDepth = 292.893
  ThreadDepthType = 0
  ThreadDiameter = 4.5
  ThreadDirection = 0
  ThreadFit = 0
  ThreadSize = 12
  ThreadType = 1
  Threaded = true
  UseCustomThreadClearance = false
FEATURE [Sketcher::SketchObject] Sketch013  label="SketchJointTop"
  ArcFitTolerance = 1e-06
  AttachmentSupport = -> [Origin008]
  ExternalGeometry = -> [Sketch012]
  ExternalTypes = [0,0,0,0,0,0,0]
  FullyConstrained = true
  MakeInternals = false
  MapMode = 5
  sketch-geometry (21):
    g0: LineSegment [constr] StartX=-35 StartY=-10 StartZ=0 EndX=-35 EndY=0 EndZ=0
    g1: GeomPoint [constr] X=-75 Y=-5 Z=0
    g2: LineSegment [constr] StartX=-75 StartY=0 StartZ=0 EndX=-75 EndY=-100 EndZ=0
    g3: LineSegment [constr] StartX=-79.5 StartY=-3 StartZ=0 EndX=-79.5 EndY=-6 EndZ=0
    g4: LineSegment [constr] StartX=-79.5 StartY=-6 StartZ=0 EndX=-70.5 EndY=-6 EndZ=0
    g5: LineSegment [constr] StartX=-70.5 StartY=-6 StartZ=0 EndX=-70.5 EndY=-3 EndZ=0
    g6: LineSegment [constr] StartX=-70.5 StartY=-3 StartZ=0 EndX=-79.5 EndY=-3 EndZ=0
    g7: LineSegment [constr] StartX=-76.5 StartY=0 StartZ=0 EndX=-76.5 EndY=-6 EndZ=0
    g8: LineSegment [constr] StartX=-76.5 StartY=-6 StartZ=0 EndX=-73.5 EndY=-6 EndZ=0
    g9: LineSegment [constr] StartX=-73.5 StartY=-6 StartZ=0 EndX=-73.5 EndY=0 EndZ=0
    g10: LineSegment [constr] StartX=-73.5 StartY=0 StartZ=0 EndX=-76.5 EndY=0 EndZ=0
    g11: LineSegment StartX=-76.5 StartY=0 StartZ=0 EndX=-73.5 EndY=0 EndZ=0
    g12: GeomPoint X=-73.5 Y=-3 Z=0
    g13: GeomPoint X=-76.5 Y=-3 Z=0
    g14: LineSegment StartX=-73.5 StartY=0 StartZ=0 EndX=-73.5 EndY=-3 EndZ=0
    g15: LineSegment StartX=-73.5 StartY=-3 StartZ=0 EndX=-70.5 EndY=-3 EndZ=0
    g16: LineSegment StartX=-70.5 StartY=-3 StartZ=0 EndX=-70.5 EndY=-6 EndZ=0
    g17: LineSegment StartX=-70.5 StartY=-6 StartZ=0 EndX=-79.5 EndY=-6 EndZ=0
    g18: LineSegment StartX=-79.5 StartY=-6 StartZ=0 EndX=-79.5 EndY=-3 EndZ=0
    g19: LineSegment StartX=-79.5 StartY=-3 StartZ=0 EndX=-76.5 EndY=-3 EndZ=0
    g20: LineSegment StartX=-76.5 StartY=-3 StartZ=0 EndX=-76.5 EndY=0 EndZ=0
  constraints (52):
    c: Coincident(g0,g-8)
    c: PointOnObject(g0,g-5)
    c: Vertical(g0)
    c: Symmetric(g-8,g0,g1)
    c: Vertical(g2)
    c: PointOnObject(g1,g2)
    c: PointOnObject(g2,g-6)
    c: PointOnObject(g2,g-5)
    c: Coincident(g3,g4)
    c: Coincident(g4,g5)
    c: Coincident(g5,g6)
    c: Coincident(g6,g3)
    c: Vertical(g3)
    c: Vertical(g5)
    c: Horizontal(g4)
    c: Horizontal(g6)
    c: Coincident(g7,g8)
    c: Coincident(g8,g9)
    c: Coincident(g9,g10)
    c: Coincident(g10,g7)
    c: Vertical(g7)
    c: Vertical(g9)
    c: Horizontal(g8)
    c: Horizontal(g10)
    c: DistanceX(g10,g10) = 3
    c: DistanceY(g9,g9) = 6
    c: Equal(g5,g10)
    c: DistanceX(g4,g4) = 9
    c: PointOnObject(g7,g4)
    c: Distance(g7,g3) = 3
    c: PointOnObject(g2,g10)
    c: Distance(g2,g7) = 1.5
    c: Coincident(g11,g7)
    c: Coincident(g11,g9)
    c: PointOnObject(g12,g6)
    c: PointOnObject(g12,g9)
    c: PointOnObject(g13,g6)
    c: PointOnObject(g13,g7)
    c: Coincident(g14,g9)
    c: Coincident(g14,g12)
    c: Coincident(g15,g12)
    c: Coincident(g15,g5)
    c: Coincident(g16,g5)
    c: Coincident(g16,g4)
    c: Coincident(g17,g4)
    c: Coincident(g17,g3)
    c: Coincident(g18,g3)
    c: Coincident(g18,g3)
    c: Coincident(g19,g3)
    c: Coincident(g19,g13)
    c: Coincident(g20,g13)
    c: Coincident(g20,g7)
FEATURE [PartDesign::Pocket] Pocket014  label="PocketJointTop"
  BaseFeature = -> Hole004
  Direction = (0,0,-1)
  Length = 25
  Length2 = 5
  Profile = -> Sketch013
  ReferenceAxis = -> Sketch013 [N_Axis]
  Refine = true
  SideType = 0
  Suppressed = false
  Type = 3
  Type2 = 0
  UpToFace = -> Hole004 [Face5]
FEATURE [Sketcher::SketchObject] Sketch014  label="SketchJointBottom"
  ArcFitTolerance = 1e-06
  AttachmentSupport = -> [Pocket014]
  ExternalGeometry = -> [Sketch013,Binder008]
  ExternalTypes = [0,0,0,0,0,0,0,0,0,0]
  FullyConstrained = true
  MakeInternals = false
  MapMode = 5
  sketch-geometry (21):
    g0: LineSegment [constr] StartX=-115 StartY=-90 StartZ=0 EndX=-115 EndY=-100 EndZ=0
    g1: GeomPoint [constr] X=-75 Y=-95 Z=0
    g2: LineSegment [constr] StartX=-75 StartY=-95 StartZ=0 EndX=-75 EndY=-100 EndZ=0
    g3: LineSegment [constr] StartX=-76.5 StartY=-100 StartZ=0 EndX=-73.5 EndY=-100 EndZ=0
    g4: LineSegment [constr] StartX=-73.5 StartY=-100 StartZ=0 EndX=-73.5 EndY=-97 EndZ=0
    g5: LineSegment [constr] StartX=-73.5 StartY=-97 StartZ=0 EndX=-76.5 EndY=-97 EndZ=0
    g6: LineSegment [constr] StartX=-76.5 StartY=-97 StartZ=0 EndX=-76.5 EndY=-100 EndZ=0
    g7: GeomPoint [constr] X=-75 Y=-98.5 Z=0
    g8: LineSegment [constr] StartX=-79.5 StartY=-94 StartZ=0 EndX=-79.5 EndY=-97 EndZ=0
    g9: LineSegment [constr] StartX=-79.5 StartY=-97 StartZ=0 EndX=-70.5 EndY=-97 EndZ=0
    g10: LineSegment [constr] StartX=-70.5 StartY=-97 StartZ=0 EndX=-70.5 EndY=-94 EndZ=0
    g11: LineSegment [constr] StartX=-70.5 StartY=-94 StartZ=0 EndX=-79.5 EndY=-94 EndZ=0
    g12: GeomPoint [constr] X=-75 Y=-95.5 Z=0
    g13: LineSegment StartX=-79.5 StartY=-94 StartZ=0 EndX=-70.5 EndY=-94 EndZ=0
    g14: LineSegment StartX=-70.5 StartY=-94 StartZ=0 EndX=-70.5 EndY=-97 EndZ=0
    g15: LineSegment StartX=-70.5 StartY=-97 StartZ=0 EndX=-73.5 EndY=-97 EndZ=0
    g16: LineSegment StartX=-73.5 StartY=-97 StartZ=0 EndX=-73.5 EndY=-100 EndZ=0
    g17: LineSegment StartX=-73.5 StartY=-100 StartZ=0 EndX=-76.5 EndY=-100 EndZ=0
    g18: LineSegment StartX=-76.5 StartY=-100 StartZ=0 EndX=-76.5 EndY=-97 EndZ=0
    g19: LineSegment StartX=-76.5 StartY=-97 StartZ=0 EndX=-79.5 EndY=-97 EndZ=0
    g20: LineSegment StartX=-79.5 StartY=-97 StartZ=0 EndX=-79.5 EndY=-94 EndZ=0
  constraints (48):
    c: Coincident(g0,g-12)
    c: PointOnObject(g0,g-11)
    c: Vertical(g0)
    c: Symmetric(g0,g-12,g1)
    c: Coincident(g2,g1)
    c: Symmetric(g-11,g-11,g2)
    c: Coincident(g3,g4)
    c: Coincident(g4,g5)
    c: Coincident(g5,g6)
    c: Coincident(g6,g3)
    c: Horizontal(g3)
    c: Horizontal(g5)
    c: Vertical(g4)
    c: Vertical(g6)
    c: PointOnObject(g3,g-11)
    c: Symmetric(g3,g4,g7)
    c: PointOnObject(g7,g2)
    c: Equal(g3,g-3)
    c: Equal(g4,g-10)
    c: Coincident(g8,g9)
    c: Coincident(g9,g10)
    c: Coincident(g10,g11)
    c: Coincident(g11,g8)
    c: Vertical(g8)
    c: Vertical(g10)
    c: Horizontal(g9)
    c: Horizontal(g11)
    c: Symmetric(g8,g10,g12)
    c: Equal(g10,g4)
    c: Equal(g11,g-7)
    c: PointOnObject(g12,g2)
    c: PointOnObject(g5,g9)
    c: Coincident(g13,g8)
    c: Coincident(g13,g10)
    c: Coincident(g14,g10)
    c: Coincident(g14,g9)
    c: Coincident(g15,g9)
    c: Coincident(g15,g4)
    c: Coincident(g16,g4)
    c: Coincident(g16,g3)
    c: Coincident(g17,g3)
    c: Coincident(g17,g3)
    c: Coincident(g18,g3)
    c: Coincident(g18,g5)
    c: Coincident(g19,g5)
    c: Coincident(g19,g8)
    c: Coincident(g20,g8)
    c: Coincident(g20,g8)
FEATURE [PartDesign::Pocket] Pocket015  label="PocketJointBottom"
  BaseFeature = -> Pocket014
  Direction = (0,0,-1)
  Length = 25
  Length2 = 5
  Profile = -> Sketch014
  ReferenceAxis = -> Sketch014 [N_Axis]
  Refine = true
  SideType = 0
  Suppressed = false
  Type = 3
  Type2 = 0
  UpToFace = -> Pocket014 [Face4]
FEATURE [Sketcher::SketchObject] Sketch015  label="SketchFrontVents"
  ArcFitTolerance = 1e-06
  AttachmentSupport = -> [Pocket015]
  ExternalGeometry = -> [Pocket015]
  ExternalTypes = [0,0,0,0,0,0,0,0]
  FullyConstrained = true
  MakeInternals = false
  MapMode = 5
  Placement = pos=(0,-10,0) rot=(1,0,0;1.5708rad)
  sketch-geometry (12):
    g0: GeomPoint X=-95.75 Y=-16 Z=0
    g1: GeomPoint [constr] X=-54.25 Y=-16 Z=0
    g2: LineSegment StartX=-111 StartY=-28 StartZ=0 EndX=-80.5 EndY=-28 EndZ=0
    g3: LineSegment StartX=-80.5 StartY=-28 StartZ=0 EndX=-80.5 EndY=-4 EndZ=0
    g4: LineSegment StartX=-80.5 StartY=-4 StartZ=0 EndX=-111 EndY=-4 EndZ=0
    g5: LineSegment StartX=-111 StartY=-4 StartZ=0 EndX=-111 EndY=-28 EndZ=0
    g6: GeomPoint [constr] X=-95.75 Y=-16 Z=0
    g7: LineSegment StartX=-69.5 StartY=-28 StartZ=0 EndX=-39 EndY=-28 EndZ=0
    g8: LineSegment StartX=-39 StartY=-28 StartZ=0 EndX=-39 EndY=-4 EndZ=0
    g9: LineSegment StartX=-39 StartY=-4 StartZ=0 EndX=-69.5 EndY=-4 EndZ=0
    g10: LineSegment StartX=-69.5 StartY=-4 StartZ=0 EndX=-69.5 EndY=-28 EndZ=0
    g11: GeomPoint [constr] X=-54.25 Y=-16 Z=0
  constraints (26):
    c: Coincident(g2,g3)
    c: Coincident(g3,g4)
    c: Coincident(g4,g5)
    c: Coincident(g5,g2)
    c: Horizontal(g2)
    c: Horizontal(g4)
    c: Vertical(g3)
    c: Vertical(g5)
    c: Symmetric(g4,g2,g6)
    c: Coincident(g7,g8)
    c: Coincident(g8,g9)
    c: Coincident(g9,g10)
    c: Coincident(g10,g7)
    c: Horizontal(g7)
    c: Horizontal(g9)
    c: Vertical(g8)
    c: Vertical(g10)
    c: Symmetric(g9,g7,g11)
    c: Distance(g4,g-4) = 4
    c: Equal(g9,g4)
    c: Equal(g10,g3)
    c: Coincident(g0,g6)
    c: Symmetric(g-8,g-5,g1)
    c: Coincident(g11,g1)
    c: Symmetric(g-6,g-10,g0)
    c: Distance(g-10,g5) = 4
FEATURE [PartDesign::Pocket] Pocket016  label="PocketFrontVents"
  BaseFeature = -> Pocket015
  Direction = (0,1,-2e-16)
  Length = 7
  Length2 = 5
  Profile = -> Sketch015
  ReferenceAxis = -> Sketch015 [N_Axis]
  Refine = true
  SideType = 1
  Suppressed = false
  Type = 3
  Type2 = 3
  UpToFace = -> Pocket015 [Face1]
  UpToFace2 = -> Pocket015 [Face22]
FEATURE [Sketcher::SketchObject] Sketch016  label="SketchSideVents"
  ArcFitTolerance = 1e-06
  AttachmentSupport = -> [Pocket016]
  ExternalGeometry = -> [Pocket016]
  ExternalTypes = [0,0,0,0]
  FullyConstrained = true
  MakeInternals = false
  MapMode = 5
  Placement = pos=(-125,0,0) rot=(0.57735,-0.57735,-0.57735;2.0944rad)
  sketch-geometry (6):
    g0: GeomPoint [constr] X=50 Y=-16 Z=0
    g1: LineSegment StartX=14 StartY=-28 StartZ=0 EndX=86 EndY=-28 EndZ=0
    g2: LineSegment StartX=86 StartY=-28 StartZ=0 EndX=86 EndY=-4 EndZ=0
    g3: LineSegment StartX=86 StartY=-4 StartZ=0 EndX=14 EndY=-4 EndZ=0
    g4: LineSegment StartX=14 StartY=-4 StartZ=0 EndX=14 EndY=-28 EndZ=0
    g5: GeomPoint [constr] X=50 Y=-16 Z=0
  constraints (13):
    c: Symmetric(g-6,g-5,g0)
    c: Coincident(g1,g2)
    c: Coincident(g2,g3)
    c: Coincident(g3,g4)
    c: Coincident(g4,g1)
    c: Horizontal(g1)
    c: Horizontal(g3)
    c: Vertical(g2)
    c: Vertical(g4)
    c: Symmetric(g3,g1,g5)
    c: Coincident(g5,g0)
    c: Distance(g-3,g4) = 4
    c: Distance(g3,g-5) = 4
FEATURE [PartDesign::Pocket] Pocket017  label="PocketSideVents001"
  BaseFeature = -> Pocket016
  Direction = (1,0,0)
  Length = 5
  Length2 = 5
  Profile = -> Sketch016
  ReferenceAxis = -> Sketch016 [N_Axis]
  Refine = true
  SideType = 0
  Suppressed = false
  Type = 3
  Type2 = 0
  UpToFace = -> Pocket016 [Face17]
FEATURE [PartDesign::Fillet] Fillet002
  Base = -> Pocket017 [Edge1,Edge2,?Edge3,Edge4,Edge5,Edge6,Edge7,Edge8,Edge9,Edge10,Edge11,Edge12,Edge13,Edge14,Edge15,Edge16,Edge17,Edge18,Edge19,Edge20,Edge21,Edge22,Edge23,Edge24,Edge25,Edge26,Edge27,Edge28,Edge29,Edge30,Edge31,Edge32,Edge33,Edge34,Edge35,Edge36,Edge37,Edge38,Edge39,Edge40,+116 more]
  BaseFeature = -> Pocket017
  Radius = 1
  Refine = true
  SupportTransform = false
  Suppressed = false
  UseAllEdges = true
FEATURE [PartDesign::Body] Body003  label="Fan Bottom"
  AllowCompound = true
  Group = -> [Binder008,Sketch012,Pad005,Hole004,Sketch013,Pocket014,Sketch014,Pocket015,Sketch015,Pocket016,Sketch016,Pocket017,Fillet002]
  Origin = -> Origin008
  Placement = pos=(0,0,-3) rot=(0,0,1;0rad)
  Tip = -> Fillet002
FEATURE [App::Point] Origin011  label="Origin014"
  Role = Origin
FEATURE [PartDesign::SubShapeBinder] Binder009
  BindCopyOnChange = 0
  BindMode = 0
  ClaimChildren = false
  Context = -> Body004 [Binder009.]
  Fuse = false
  MakeFace = true
  OffsetFill = false
  OffsetIntersection = false
  OffsetJoinType = 0
  OffsetOpenResult = false
  PartialLoad = false
  Refine = true
  Relative = true
  Support = -> [Sketch]
  _Version = 2
FEATURE [Sketcher::SketchObject] Sketch017
  ArcFitTolerance = 1e-06
  AttachmentSupport = -> [Origin010]
  ExternalGeometry = -> [Binder009]
  ExternalTypes = [0,0,0,0,0,0,0,0,0,0,0,0]
  FullyConstrained = true
  MakeInternals = false
  MapMode = 5
  sketch-geometry (1):
    g0: LineSegment StartX=25 StartY=100 StartZ=0 EndX=25 EndY=50 EndZ=0
  constraints (2):
    c: Coincident(g0,g-4)
    c: Coincident(g0,g-6)
FEATURE [App::Point] Origin013  label="Origin017"
  Role = Origin
FEATURE [PartDesign::SubShapeBinder] Binder010
  BindCopyOnChange = 0
  BindMode = 0
  ClaimChildren = false
  Context = -> Body005 [Binder010.]
  Fuse = false
  MakeFace = true
  OffsetFill = false
  OffsetIntersection = false
  OffsetJoinType = 0
  OffsetOpenResult = false
  PartialLoad = false
  Refine = true
  Relative = true
  Support = -> [Sketch]
  _Version = 2
FEATURE [Sketcher::SketchObject] Sketch018  label="SketchBody"
  ArcFitTolerance = 1e-06
  AttachmentSupport = -> [Origin012]
  ExternalGeometry = -> [Binder010]
  ExternalTypes = [0,0,0,0,0,0,0,0]
  FullyConstrained = true
  MakeInternals = false
  MapMode = 5
  sketch-geometry (40):
    g0: LineSegment [constr] StartX=35 StartY=90 StartZ=0 EndX=35 EndY=100 EndZ=0
    g1: LineSegment [constr] StartX=35 StartY=100 StartZ=0 EndX=25 EndY=100 EndZ=0
    g2: LineSegment [constr] StartX=25 StartY=100 StartZ=0 EndX=25 EndY=90 EndZ=0
    g3: LineSegment [constr] StartX=25 StartY=90 StartZ=0 EndX=35 EndY=90 EndZ=0
    g4: GeomPoint [constr] X=30 Y=95 Z=0
    g5: LineSegment [constr] StartX=115 StartY=90 StartZ=0 EndX=125 EndY=90 EndZ=0
    g6: LineSegment [constr] StartX=125 StartY=90 StartZ=0 EndX=125 EndY=100 EndZ=0
    g7: LineSegment [constr] StartX=125 StartY=100 StartZ=0 EndX=115 EndY=100 EndZ=0
    g8: LineSegment [constr] StartX=115 StartY=100 StartZ=0 EndX=115 EndY=90 EndZ=0
    g9: GeomPoint [constr] X=120 Y=95 Z=0
    g10: LineSegment [constr] StartX=115 StartY=60 StartZ=0 EndX=115 EndY=50 EndZ=0
    g11: LineSegment [constr] StartX=115 StartY=50 StartZ=0 EndX=125 EndY=50 EndZ=0
    g12: LineSegment [constr] StartX=125 StartY=50 StartZ=0 EndX=125 EndY=60 EndZ=0
    g13: LineSegment [constr] StartX=125 StartY=60 StartZ=0 EndX=115 EndY=60 EndZ=0
    g14: GeomPoint [constr] X=120 Y=55 Z=0
    g15: LineSegment [constr] StartX=35 StartY=60 StartZ=0 EndX=25 EndY=60 EndZ=0
    g16: LineSegment [constr] StartX=25 StartY=60 StartZ=0 EndX=25 EndY=50 EndZ=0
    g17: LineSegment [constr] StartX=25 StartY=50 StartZ=0 EndX=35 EndY=50 EndZ=0
    g18: LineSegment [constr] StartX=35 StartY=50 StartZ=0 EndX=35 EndY=60 EndZ=0
    g19: GeomPoint [constr] X=30 Y=55 Z=0
    g20: LineSegment [constr] StartX=28 StartY=90 StartZ=0 EndX=28 EndY=60 EndZ=0
    g21: LineSegment [constr] StartX=115 StartY=58 StartZ=0 EndX=35 EndY=58 EndZ=0
    g22: LineSegment [constr] StartX=35 StartY=92 StartZ=0 EndX=115 EndY=92 EndZ=0
    g23: LineSegment StartX=25 StartY=100 StartZ=0 EndX=25 EndY=50 EndZ=0
    g24: LineSegment StartX=25 StartY=50 StartZ=0 EndX=125 EndY=50 EndZ=0
    g25: LineSegment StartX=125 StartY=50 StartZ=0 EndX=125 EndY=100 EndZ=0
    g26: LineSegment StartX=125 StartY=100 StartZ=0 EndX=25 EndY=100 EndZ=0
    g27: LineSegment StartX=35 StartY=92 StartZ=0 EndX=35 EndY=90 EndZ=0
    g28: LineSegment StartX=35 StartY=90 StartZ=0 EndX=28 EndY=90 EndZ=0
    g29: LineSegment StartX=28 StartY=90 StartZ=0 EndX=28 EndY=60 EndZ=0
    g30: LineSegment StartX=28 StartY=60 StartZ=0 EndX=35 EndY=60 EndZ=0
    g31: LineSegment StartX=35 StartY=60 StartZ=0 EndX=35 EndY=58 EndZ=0
    g32: LineSegment StartX=35 StartY=58 StartZ=0 EndX=115 EndY=58 EndZ=0
    g33: LineSegment StartX=115 StartY=58 StartZ=0 EndX=115 EndY=60 EndZ=0
    g34: LineSegment StartX=35 StartY=92 StartZ=0 EndX=115 EndY=92 EndZ=0
    g35: LineSegment StartX=115 StartY=92 StartZ=0 EndX=115 EndY=90 EndZ=0
    g36: LineSegment [constr] StartX=122 StartY=60 StartZ=0 EndX=122 EndY=90 EndZ=0
    g37: LineSegment StartX=115 StartY=90 StartZ=0 EndX=122 EndY=90 EndZ=0
    g38: LineSegment StartX=122 StartY=90 StartZ=0 EndX=122 EndY=60 EndZ=0
    g39: LineSegment StartX=122 StartY=60 StartZ=0 EndX=115 EndY=60 EndZ=0
  constraints (92):
    c: Coincident(g0,g1)
    c: Coincident(g1,g2)
    c: Coincident(g2,g3)
    c: Coincident(g3,g0)
    c: Vertical(g0)
    c: Vertical(g2)
    c: Horizontal(g1)
    c: Horizontal(g3)
    c: Symmetric(g2,g0,g4)
    c: Coincident(g4,g-7)
    c: Coincident(g1,g-4)
    c: Coincident(g5,g6)
    c: Coincident(g6,g7)
    c: Coincident(g7,g8)
    c: Coincident(g8,g5)
    c: Horizontal(g5)
    c: Horizontal(g7)
    c: Vertical(g6)
    c: Vertical(g8)
    c: Symmetric(g7,g5,g9)
    c: Coincident(g9,g-10)
    c: Coincident(g6,g-6)
    c: Coincident(g10,g11)
    c: Coincident(g11,g12)
    c: Coincident(g12,g13)
    c: Coincident(g13,g10)
    c: Vertical(g10)
    c: Vertical(g12)
    c: Horizontal(g11)
    c: Horizontal(g13)
    c: Symmetric(g12,g10,g14)
    c: Coincident(g14,g-9)
    c: Coincident(g11,g-6)
    c: Coincident(g15,g16)
    c: Coincident(g16,g17)
    c: Coincident(g17,g18)
    c: Coincident(g18,g15)
    c: Horizontal(g15)
    c: Horizontal(g17)
    c: Vertical(g16)
    c: Vertical(g18)
    c: Symmetric(g17,g15,g19)
    c: Coincident(g19,g-8)
    c: Coincident(g16,g-5)
    c: PointOnObject(g20,g3)
    c: PointOnObject(g20,g15)
    c: Vertical(g20)
    c: PointOnObject(g21,g10)
    c: PointOnObject(g21,g18)
    c: Horizontal(g21)
    c: Distance(g-5,g21) = 8
    c: Distance(g20,g-3) = 3
    c: PointOnObject(g22,g0)
    c: PointOnObject(g22,g8)
    c: Horizontal(g22)
    c: Distance(g-4,g22) = 8
    c: Coincident(g23,g1)
    c: Coincident(g23,g16)
    c: Coincident(g24,g16)
    c: Coincident(g24,g11)
    c: Coincident(g25,g11)
    c: Coincident(g25,g6)
    c: Coincident(g26,g6)
    c: Coincident(g26,g1)
    c: Coincident(g27,g22)
    c: Coincident(g27,g0)
    c: Coincident(g28,g0)
    c: Coincident(g28,g20)
    c: Coincident(g29,g20)
    c: Coincident(g29,g20)
    c: Coincident(g30,g20)
    c: Coincident(g30,g15)
    c: Coincident(g31,g15)
    c: Coincident(g31,g21)
    c: Coincident(g32,g21)
    c: Coincident(g32,g21)
    c: Coincident(g33,g21)
    c: Coincident(g33,g10)
    c: Coincident(g34,g22)
    c: Coincident(g34,g22)
    c: Coincident(g35,g22)
    c: Coincident(g35,g5)
    c: Vertical(g36)
    c: PointOnObject(g36,g5)
    c: PointOnObject(g36,g13)
    c: Distance(g25,g36) = 3
    c: Coincident(g37,g5)
    c: Coincident(g37,g36)
    c: Coincident(g38,g36)
    c: Coincident(g38,g36)
    c: Coincident(g39,g36)
    c: Coincident(g39,g10)
FEATURE [PartDesign::Pad] Pad007  label="PadBody003"
  Direction = (0,0,1)
  Length = 32
  Length2 = 10
  Profile = -> Sketch018
  ReferenceAxis = -> Sketch018 [N_Axis]
  Refine = true
  SideType = 0
  Suppressed = false
  Type = 0
  Type2 = 0
FEATURE [Sketcher::SketchObject] Sketch019  label="SketchHoles001"
  ArcFitTolerance = 1e-06
  AttachmentSupport = -> [Pad007]
  ExternalGeometry = -> [Binder010]
  ExternalTypes = [0,0,0,0]
  FullyConstrained = true
  MakeInternals = false
  MapMode = 5
  Placement = pos=(0,0,32) rot=(0,0,1;0rad)
FEATURE [PartDesign::Hole] Hole006  label="HoleScrews002"
  BaseFeature = -> Pad007
  BaseProfileType = 7
  CustomThreadClearance = 0
  Depth = 35
  DepthType = 0
  Diameter = 3.7
  DrillForDepth = false
  DrillPoint = 1
  DrillPointAngle = 118
  HoleCutCountersinkAngle = 90
  HoleCutCustomValues = false
  HoleCutDepth = 0
  HoleCutDiameter = 0
  HoleCutType = 0
  ModelThread = false
  Profile = -> Sketch019
  Refine = true
  Suppressed = false
  Tapered = false
  TaperedAngle = 90
  ThreadClass = 0
  ThreadDepth = 35
  ThreadDepthType = 0
  ThreadDiameter = 4.5
  ThreadDirection = 0
  ThreadFit = 0
  ThreadSize = 12
  ThreadType = 1
  Threaded = true
  UseCustomThreadClearance = false
FEATURE [Sketcher::SketchObject] Sketch020  label="SketchJoints"
  ArcFitTolerance = 1e-06
  AttachmentSupport = -> [Hole006]
  ExternalGeometry = -> [Binder010]
  ExternalTypes = [0,0,0]
  FullyConstrained = true
  MakeInternals = false
  MapMode = 5
  Placement = pos=(0,0,32) rot=(0,0,1;0rad)
  sketch-geometry (55):
    g0: LineSegment [constr] StartX=25 StartY=100 StartZ=0 EndX=25 EndY=90 EndZ=0
    g1: LineSegment [constr] StartX=25 StartY=90 StartZ=0 EndX=125 EndY=90 EndZ=0
    g2: LineSegment [constr] StartX=125 StartY=90 StartZ=0 EndX=125 EndY=100 EndZ=0
    g3: LineSegment [constr] StartX=125 StartY=100 StartZ=0 EndX=25 EndY=100 EndZ=0
    g4: LineSegment [constr] StartX=25 StartY=60 StartZ=0 EndX=25 EndY=50 EndZ=0
    g5: LineSegment [constr] StartX=25 StartY=50 StartZ=0 EndX=125 EndY=50 EndZ=0
    g6: LineSegment [constr] StartX=125 StartY=50 StartZ=0 EndX=125 EndY=60 EndZ=0
    g7: LineSegment [constr] StartX=125 StartY=60 StartZ=0 EndX=25 EndY=60 EndZ=0
    g8: GeomPoint [constr] X=75 Y=95 Z=0
    g9: GeomPoint [constr] X=75 Y=55 Z=0
    g10: LineSegment [constr] StartX=75 StartY=100 StartZ=0 EndX=75 EndY=50 EndZ=0
    g11: LineSegment [constr] StartX=73.5 StartY=100 StartZ=0 EndX=73.5 EndY=97 EndZ=0
    g12: LineSegment [constr] StartX=73.5 StartY=97 StartZ=0 EndX=76.5 EndY=97 EndZ=0
    g13: LineSegment [constr] StartX=76.5 StartY=97 StartZ=0 EndX=76.5 EndY=100 EndZ=0
    g14: LineSegment [constr] StartX=76.5 StartY=100 StartZ=0 EndX=73.5 EndY=100 EndZ=0
    g15: LineSegment [constr] StartX=70.5 StartY=97 StartZ=0 EndX=70.5 EndY=94 EndZ=0
    g16: LineSegment [constr] StartX=70.5 StartY=94 StartZ=0 EndX=79.5 EndY=94 EndZ=0
    g17: LineSegment [constr] StartX=79.5 StartY=94 StartZ=0 EndX=79.5 EndY=97 EndZ=0
    g18: LineSegment [constr] StartX=79.5 StartY=97 StartZ=0 EndX=70.5 EndY=97 EndZ=0
    g19: GeomPoint [constr] X=75 Y=95.5 Z=0
    g20: GeomPoint [constr] X=75 Y=98.5 Z=0
    g21: LineSegment [constr] StartX=75 StartY=98.5 StartZ=0 EndX=75 EndY=97 EndZ=0
    g22: LineSegment [constr] StartX=75 StartY=97 StartZ=0 EndX=75 EndY=95.5 EndZ=0
    g23: GeomPoint [constr] X=75 Y=97 Z=0
    g24: LineSegment [constr] StartX=75 StartY=98.5 StartZ=0 EndX=75 EndY=100 EndZ=0
    g25: LineSegment StartX=73.5 StartY=100 StartZ=0 EndX=76.5 EndY=100 EndZ=0
    g26: LineSegment StartX=76.5 StartY=100 StartZ=0 EndX=76.5 EndY=97 EndZ=0
    g27: LineSegment StartX=76.5 StartY=97 StartZ=0 EndX=79.5 EndY=97 EndZ=0
    g28: LineSegment StartX=79.5 StartY=97 StartZ=0 EndX=79.5 EndY=94 EndZ=0
    g29: LineSegment StartX=79.5 StartY=94 StartZ=0 EndX=70.5 EndY=94 EndZ=0
    g30: LineSegment StartX=70.5 StartY=94 StartZ=0 EndX=70.5 EndY=97 EndZ=0
    g31: LineSegment StartX=70.5 StartY=97 StartZ=0 EndX=73.5 EndY=97 EndZ=0
    g32: LineSegment StartX=73.5 StartY=97 StartZ=0 EndX=73.5 EndY=100 EndZ=0
    g33: LineSegment [constr] StartX=70.5 StartY=56 StartZ=0 EndX=70.5 EndY=53 EndZ=0
    g34: LineSegment [constr] StartX=70.5 StartY=53 StartZ=0 EndX=79.5 EndY=53 EndZ=0
    g35: LineSegment [constr] StartX=79.5 StartY=53 StartZ=0 EndX=79.5 EndY=56 EndZ=0
    g36: LineSegment [constr] StartX=79.5 StartY=56 StartZ=0 EndX=70.5 EndY=56 EndZ=0
    g37: LineSegment [constr] StartX=73.5 StartY=53 StartZ=0 EndX=73.5 EndY=50 EndZ=0
    g38: LineSegment [constr] StartX=73.5 StartY=50 StartZ=0 EndX=76.5 EndY=50 EndZ=0
    g39: LineSegment [constr] StartX=76.5 StartY=50 StartZ=0 EndX=76.5 EndY=53 EndZ=0
    g40: LineSegment [constr] StartX=76.5 StartY=53 StartZ=0 EndX=73.5 EndY=53 EndZ=0
    g41: GeomPoint [constr] X=75 Y=54.5 Z=0
    g42: LineSegment [constr] StartX=75 StartY=56 StartZ=0 EndX=75 EndY=53 EndZ=0
    g43: GeomPoint [constr] X=75 Y=51.5 Z=0
    g44: LineSegment [constr] StartX=75 StartY=53 StartZ=0 EndX=75 EndY=51.5 EndZ=0
    g45: LineSegment [constr] StartX=75 StartY=51.5 StartZ=0 EndX=75 EndY=50 EndZ=0
    g46: LineSegment [constr] StartX=70.5 StartY=56 StartZ=0 EndX=79.5 EndY=56 EndZ=0
    g47: LineSegment StartX=70.5 StartY=56 StartZ=0 EndX=79.5 EndY=56 EndZ=0
    g48: LineSegment StartX=79.5 StartY=56 StartZ=0 EndX=79.5 EndY=53 EndZ=0
    g49: LineSegment StartX=79.5 StartY=53 StartZ=0 EndX=76.5 EndY=53 EndZ=0
    g50: LineSegment StartX=76.5 StartY=53 StartZ=0 EndX=76.5 EndY=50 EndZ=0
    g51: LineSegment StartX=76.5 StartY=50 StartZ=0 EndX=73.5 EndY=50 EndZ=0
    g52: LineSegment StartX=73.5 StartY=50 StartZ=0 EndX=73.5 EndY=53 EndZ=0
    g53: LineSegment StartX=73.5 StartY=53 StartZ=0 EndX=70.5 EndY=53 EndZ=0
    g54: LineSegment StartX=70.5 StartY=53 StartZ=0 EndX=70.5 EndY=56 EndZ=0
  constraints (130):
    c: Coincident(g0,g1)
    c: Coincident(g1,g2)
    c: Coincident(g2,g3)
    c: Coincident(g3,g0)
    c: Vertical(g0)
    c: Vertical(g2)
    c: Horizontal(g1)
    c: Horizontal(g3)
    c: Coincident(g0,g-4)
    c: PointOnObject(g1,g-5)
    c: Distance(g3,g1) = 10
    c: Coincident(g4,g5)
    c: Coincident(g5,g6)
    c: Coincident(g6,g7)
    c: Coincident(g7,g4)
    c: Vertical(g4)
    c: Vertical(g6)
    c: Horizontal(g5)
    c: Horizontal(g7)
    c: PointOnObject(g4,g-4)
    c: Coincident(g5,g-5)
    c: Distance(g5,g7) = 10
    c: Symmetric(g0,g2,g8)
    c: Symmetric(g4,g6,g9)
    c: Vertical(g10)
    c: PointOnObject(g10,g5)
    c: PointOnObject(g10,g3)
    c: PointOnObject(g8,g10)
    c: Coincident(g11,g12)
    c: Coincident(g12,g13)
    c: Coincident(g13,g14)
    c: Coincident(g14,g11)
    c: Vertical(g11)
    c: Vertical(g13)
    c: Horizontal(g12)
    c: Horizontal(g14)
    c: Coincident(g15,g16)
    c: Coincident(g16,g17)
    c: Coincident(g17,g18)
    c: Coincident(g18,g15)
    c: Vertical(g15)
    c: Vertical(g17)
    c: Horizontal(g16)
    c: Horizontal(g18)
    c: DistanceX(g14,g14) = 3
    c: Equal(g13,g14)
    c: Symmetric(g15,g17,g19)
    c: Symmetric(g11,g13,g20)
    c: Coincident(g21,g20)
    c: Symmetric(g18,g18,g21)
    c: Vertical(g21)
    c: Coincident(g22,g21)
    c: Coincident(g22,g19)
    c: PointOnObject(g23,g12)
    c: PointOnObject(g23,g21)
    c: PointOnObject(g23,g18)
    c: DistanceX(g18,g18) = 9
    c: Equal(g17,g13)
    c: Coincident(g24,g20)
    c: Symmetric(g14,g14,g24)
    c: Coincident(g24,g10)
    c: Coincident(g25,g11)
    c: Coincident(g25,g13)
    c: Coincident(g26,g13)
    c: Coincident(g26,g12)
    c: Coincident(g27,g12)
    c: Coincident(g27,g17)
    c: Coincident(g28,g17)
    c: Coincident(g28,g16)
    c: Coincident(g29,g16)
    c: Coincident(g29,g15)
    c: Coincident(g30,g15)
    c: Coincident(g30,g15)
    c: Coincident(g31,g15)
    c: Coincident(g31,g11)
    c: Coincident(g32,g11)
    c: Coincident(g32,g11)
    c: Coincident(g33,g34)
    c: Coincident(g34,g35)
    c: Coincident(g35,g36)
    c: Coincident(g36,g33)
    c: Vertical(g33)
    c: Vertical(g35)
    c: Horizontal(g34)
    c: Horizontal(g36)
    c: Coincident(g37,g38)
    c: Coincident(g38,g39)
    c: Coincident(g39,g40)
    c: Coincident(g40,g37)
    c: Vertical(g37)
    c: Vertical(g39)
    c: Horizontal(g38)
    c: Horizontal(g40)
    c: PointOnObject(g37,g34)
    c: Equal(g38,g37)
    c: Equal(g37,g25)
    c: Equal(g39,g35)
    c: Equal(g34,g29)
    c: Symmetric(g33,g35,g41)
    c: Vertical(g42)
    c: PointOnObject(g41,g42)
    c: PointOnObject(g42,g34)
    c: PointOnObject(g42,g36)
    c: Symmetric(g37,g39,g43)
    c: Vertical(g44)
    c: Coincident(g44,g42)
    c: Coincident(g44,g43)
    c: PointOnObject(g45,g38)
    c: Vertical(g45)
    c: Coincident(g45,g43)
    c: Coincident(g45,g10)
    c: Coincident(g47,g46)
    c: Coincident(g47,g46)
    c: Horizontal(g47)
    c: Coincident(g46,g33)
    c: Equal(g47,g36)
    c: Coincident(g48,g35)
    c: Coincident(g48,g34)
    c: Coincident(g49,g34)
    c: Coincident(g49,g39)
    c: Coincident(g50,g39)
    c: Coincident(g50,g38)
    c: Coincident(g51,g38)
    c: Coincident(g51,g37)
    c: Coincident(g52,g37)
    c: Coincident(g52,g37)
    c: Coincident(g53,g37)
    c: Coincident(g53,g33)
    c: Coincident(g54,g33)
    c: Coincident(g54,g33)
FEATURE [PartDesign::Pocket] Pocket018  label="PocketJoints"
  BaseFeature = -> Hole006
  Direction = (0,0,-1)
  Length = 5
  Length2 = 5
  Profile = -> Sketch020
  ReferenceAxis = -> Sketch020 [N_Axis]
  Refine = true
  SideType = 0
  Suppressed = false
  Type = 3
  Type2 = 0
  UpToFace = -> Hole006 [Face4]
FEATURE [Sketcher::SketchObject] Sketch021  label="SketchFrontVents001"
  ArcFitTolerance = 1e-06
  AttachmentSupport = -> [Pocket018]
  ExternalGeometry = -> [Pocket018]
  ExternalTypes = [0,0,0,0,0,0,0,0]
  FullyConstrained = true
  MakeInternals = false
  MapMode = 5
  Placement = pos=(0,50,0) rot=(1,0,0;1.5708rad)
  sketch-geometry (12):
    g0: GeomPoint [constr] X=54.25 Y=16 Z=0
    g1: GeomPoint [constr] X=95.75 Y=16 Z=0
    g2: LineSegment StartX=40 StartY=5 StartZ=0 EndX=68.5 EndY=5 EndZ=0
    g3: LineSegment StartX=68.5 StartY=5 StartZ=0 EndX=68.5 EndY=27 EndZ=0
    g4: LineSegment StartX=68.5 StartY=27 StartZ=0 EndX=40 EndY=27 EndZ=0
    g5: LineSegment StartX=40 StartY=27 StartZ=0 EndX=40 EndY=5 EndZ=0
    g6: GeomPoint [constr] X=54.25 Y=16 Z=0
    g7: LineSegment StartX=81.5 StartY=5 StartZ=0 EndX=110 EndY=5 EndZ=0
    g8: LineSegment StartX=110 StartY=5 StartZ=0 EndX=110 EndY=27 EndZ=0
    g9: LineSegment StartX=110 StartY=27 StartZ=0 EndX=81.5 EndY=27 EndZ=0
    g10: LineSegment StartX=81.5 StartY=27 StartZ=0 EndX=81.5 EndY=5 EndZ=0
    g11: GeomPoint [constr] X=95.75 Y=16 Z=0
  constraints (26):
    c: Symmetric(g-3,g-7,g0)
    c: Symmetric(g-10,g-4,g1)
    c: Coincident(g2,g3)
    c: Coincident(g3,g4)
    c: Coincident(g4,g5)
    c: Coincident(g5,g2)
    c: Horizontal(g2)
    c: Horizontal(g4)
    c: Vertical(g3)
    c: Vertical(g5)
    c: Symmetric(g4,g2,g6)
    c: Coincident(g6,g0)
    c: Coincident(g7,g8)
    c: Coincident(g8,g9)
    c: Coincident(g9,g10)
    c: Coincident(g10,g7)
    c: Horizontal(g7)
    c: Horizontal(g9)
    c: Vertical(g8)
    c: Vertical(g10)
    c: Symmetric(g9,g7,g11)
    c: Coincident(g11,g1)
    c: Distance(g-6,g4) = 5
    c: Distance(g-3,g5) = 5
    c: Equal(g9,g4)
    c: Equal(g10,g3)
FEATURE [PartDesign::Pocket] Pocket019  label="PocketFrontVents001"
  BaseFeature = -> Pocket018
  Direction = (0,1,-2e-16)
  Length = 5
  Length2 = 5
  Profile = -> Sketch021
  ReferenceAxis = -> Sketch021 [N_Axis]
  Refine = true
  SideType = 0
  Suppressed = false
  Type = 3
  Type2 = 0
  UpToFace = -> Pocket018 [Face14]
FEATURE [Sketcher::SketchObject] Sketch022  label="SketchSideVents001"
  ArcFitTolerance = 1e-06
  AttachmentSupport = -> [Pocket019]
  ExternalGeometry = -> [Pocket019]
  ExternalTypes = [0,0,0,0]
  FullyConstrained = true
  MakeInternals = false
  MapMode = 5
  Placement = pos=(25,0,0) rot=(0.57735,-0.57735,-0.57735;2.0944rad)
  sketch-geometry (6):
    g0: GeomPoint [constr] X=-75 Y=16 Z=0
    g1: LineSegment StartX=-85 StartY=5 StartZ=0 EndX=-65 EndY=5 EndZ=0
    g2: LineSegment StartX=-65 StartY=5 StartZ=0 EndX=-65 EndY=27 EndZ=0
    g3: LineSegment StartX=-65 StartY=27 StartZ=0 EndX=-85 EndY=27 EndZ=0
    g4: LineSegment StartX=-85 StartY=27 StartZ=0 EndX=-85 EndY=5 EndZ=0
    g5: GeomPoint [constr] X=-75 Y=16 Z=0
  constraints (13):
    c: Symmetric(g-3,g-5,g0)
    c: Coincident(g1,g2)
    c: Coincident(g2,g3)
    c: Coincident(g3,g4)
    c: Coincident(g4,g1)
    c: Horizontal(g1)
    c: Horizontal(g3)
    c: Vertical(g2)
    c: Vertical(g4)
    c: Symmetric(g3,g1,g5)
    c: Coincident(g5,g0)
    c: Distance(g-5,g3) = 5
    c: Distance(g-4,g2) = 5
FEATURE [PartDesign::Pocket] Pocket020  label="PocketSideVents002"
  BaseFeature = -> Pocket019
  Direction = (1,0,0)
  Length = 5
  Length2 = 5
  Profile = -> Sketch022
  ReferenceAxis = -> Sketch022 [N_Axis]
  Refine = true
  SideType = 0
  Suppressed = false
  Type = 3
  Type2 = 0
  UpToFace = -> Pocket019 [Face23]
FEATURE [PartDesign::Fillet] Fillet004
  Base = -> Pocket020 [Face61,Face62,Face60,Face59,Face48,Face49,Face50,Face47,Face14,Face13,Face11,Face54,Face51,Face53,Face52,Face12]
  BaseFeature = -> Pocket020
  Radius = 1
  Refine = true
  SupportTransform = false
  Suppressed = false
  UseAllEdges = false
FEATURE [PartDesign::Fillet] Fillet005
  Base = -> Fillet004 [Face75,Face78,Edge138,Face76,Face77,Face58,Face55,Face57,Face56]
  BaseFeature = -> Fillet004
  Radius = 1
  Refine = true
  SupportTransform = false
  Suppressed = false
  UseAllEdges = false
FEATURE [PartDesign::Fillet] Fillet006
  Base = -> Fillet005 [Face10,Face37,Face1,Face13,Face39,Face38]
  BaseFeature = -> Fillet005
  Radius = 1
  Refine = true
  SupportTransform = false
  Suppressed = false
  UseAllEdges = false
FEATURE [PartDesign::Fillet] Fillet007
  Base = -> Fillet006 [Edge87,Edge78,Edge80,Edge82,Edge84,Edge86,Edge88,Edge85,Edge83,Edge81,Edge79,Edge77]
  BaseFeature = -> Fillet006
  Radius = 1
  Refine = true
  SupportTransform = false
  Suppressed = false
  UseAllEdges = false
FEATURE [PartDesign::Fillet] Fillet008
  Base = -> Fillet007 [Vertex81,Edge141,Edge145,Edge165,Edge169,Edge172,Edge171,Edge167,Edge155,Edge143,Edge138,Edge118]
  BaseFeature = -> Fillet007
  Radius = 1
  Refine = true
  SupportTransform = false
  Suppressed = false
  UseAllEdges = false
FEATURE [PartDesign::Fillet] Fillet009
  Base = -> Fillet008 [Edge143,Edge272,Edge178,Edge67]
  BaseFeature = -> Fillet008
  Radius = 1
  Refine = true
  SupportTransform = false
  Suppressed = false
  UseAllEdges = false
FEATURE [PartDesign::Fillet] Fillet010
  Base = -> Fillet009 [Edge162,Edge160,Edge164,Edge168,Edge172,Edge158]
  BaseFeature = -> Fillet009
  Radius = 1
  Refine = true
  SupportTransform = false
  Suppressed = false
  UseAllEdges = false
FEATURE [PartDesign::Body] Body005  label="SwitchBoxBottom"
  AllowCompound = true
  Group = -> [Binder010,Sketch018,Pad007,Sketch019,Hole006,Sketch020,Pocket018,Sketch021,Pocket019,Sketch022,Pocket020,Fillet004,Fillet005,Fillet006,Fillet007,Fillet008,Fillet009,Fillet010]
  Origin = -> Origin012
  Tip = -> Fillet010
FEATURE [PartDesign::Fillet] Fillet012
  Base = -> Pocket002 [Face11,Face12,Face14,Face10,Face8]
  BaseFeature = -> Pocket002
  Radius = 1
  Refine = true
  SupportTransform = false
  Suppressed = false
  UseAllEdges = false
FEATURE [PartDesign::Body] Body001  label="Fan Right Top"
  AllowCompound = true
  Group = -> [Binder001,Sketch004,Pad002,Hole001,Hole002,Pocket002,Sketch005,Fillet012]
  Origin = -> Origin002
  Tip = -> Fillet012
FEATURE [App::Link] Pole82mm
  LinkPlacement = pos=(133.113,57.3188,-85.6169) rot=(0,0,1;0rad)
  LinkedObject = -> <external Joints.FCStd>#Body003
  Placement = pos=(133.113,57.3188,-85.6169) rot=(0,0,1;0rad)
FEATURE [App::Link] SwitchBoxTop  label="SwitchBoxTop001"
  LinkPlacement = pos=(-88.6868,-48.2812,-0.116936) rot=(0.688247,-0.688247,-0.229416;0rad)
  LinkedObject = -> Body004
  Placement = pos=(-88.6868,-48.2812,-0.116936) rot=(0.688247,-0.688247,-0.229416;0rad)
FEATURE [App::Link] SwitchBoxBottom  label="SwitchBoxBottom001"
  LinkPlacement = pos=(-89.6868,-47.2812,-32.1169) rot=(0.688247,-0.688247,-0.229416;0rad)
  LinkedObject = -> Body005
  Placement = pos=(-89.6868,-47.2812,-32.1169) rot=(0.688247,-0.688247,-0.229416;0rad)
FEATURE [App::Link] Fan_Bottom  label="Fan Bottom001"
  LinkPlacement = pos=(-70.3,-105.6,83.5) rot=(0,0,1;3.14159rad)
  LinkedObject = -> Body003
  Placement = pos=(-70.3,-105.6,83.5) rot=(0,0,1;3.14159rad)
FEATURE [App::Link] Fan_Right_Top  label="Fan Right Top001"
  LinkPlacement = pos=(79.7597,-5.44972,86.4727) rot=(0,0,1;0rad)
  LinkedObject = -> Body001
  Placement = pos=(79.7597,-5.44972,86.4727) rot=(0,0,1;0rad)
FEATURE [App::Link] Connector5Way
  LinkedObject = -> <external Joints.FCStd>#Body001
FEATURE [App::FeaturePython] GroundedJoint  label="GroundedJoint001"  # Assembly grounded joint (typed FeaturePython)
  ObjectToGround = -> Connector5Way
FEATURE [Assembly::JointGroup] Joints
  Group = -> [GroundedJoint]
FEATURE [App::Link] Connector5Way001
  LinkPlacement = pos=(1.92e-14,-99.8795,5e-15) rot=(0,0,1;0rad)
  LinkedObject = -> <external Joints.FCStd>#Body001
  Placement = pos=(1.92e-14,-99.8795,5e-15) rot=(0,0,1;0rad)
FEATURE [App::FeaturePython] Motion  label="Slider022 (Linear)"  # WARN: FeaturePython — macro-defined, semantics opaque (R4)
  Formula = 5*time
  MotionType = 1
FEATURE [App::FeaturePython] Simulation  # WARN: FeaturePython — macro-defined, semantics opaque (R4)
  Group = -> [Motion]
  aTimeStart = 0
  bTimeEnd = 1
  cTimeStepOutput = 0.01
  fGlobalErrorTolerance = 1e-06
  jFramesPerSecond = 30
FEATURE [Assembly::SimulationGroup] Simulations
  Group = -> [Simulation]
FEATURE [App::Link] Pole82mm001
  LinkPlacement = pos=(0.3,-99.8795,5e-15) rot=(0,0,1;0rad)
  LinkedObject = -> <external Joints.FCStd>#Body003
  Placement = pos=(0.3,-99.8795,5e-15) rot=(0,0,1;0rad)
FEATURE [App::Link] Connector5Way002
  LinkPlacement = pos=(-19.1868,58.3188,-84.6169) rot=(0.688247,-0.688247,-0.229416;0rad)
  LinkedObject = -> <external Joints.FCStd>#Body001
  Placement = pos=(-19.1868,58.3188,-84.6169) rot=(0.688247,-0.688247,-0.229416;0rad)
FEATURE [App::Link] Pole82mm002
  LinkPlacement = pos=(-18.8868,58.3188,-84.6169) rot=(0.688247,-0.688247,-0.229416;0rad)
  LinkedObject = -> <external Joints.FCStd>#Body003
  Placement = pos=(-18.8868,58.3188,-84.6169) rot=(0.688247,-0.688247,-0.229416;0rad)
FEATURE [Sketcher::SketchObject] Sketch023  label="SketchFrontVent"
  ArcFitTolerance = 1e-06
  AttachmentSupport = -> [Hole003]
  ExternalGeometry = -> [Hole003]
  ExternalTypes = [0,0,0,0,0,0]
  FullyConstrained = true
  MakeInternals = false
  MapMode = 5
  Placement = pos=(0,50,0) rot=(1,0,0;1.5708rad)
  sketch-geometry (16):
    g0: LineSegment [constr] StartX=-122.05 StartY=-7 StartZ=0 EndX=-122.05 EndY=-75 EndZ=0
    g1: LineSegment [constr] StartX=-76.5 StartY=-7 StartZ=0 EndX=-76.5 EndY=-75 EndZ=0
    g2: LineSegment [constr] StartX=-73.5 StartY=-7 StartZ=0 EndX=-73.5 EndY=-75 EndZ=0
    g3: LineSegment [constr] StartX=-27.95 StartY=-7 StartZ=0 EndX=-27.95 EndY=-75 EndZ=0
    g4: GeomPoint [constr] X=-99.275 Y=-41 Z=0
    g5: GeomPoint [constr] X=-50.725 Y=-41 Z=0
    g6: LineSegment StartX=-117.05 StartY=-70 StartZ=0 EndX=-81.5 EndY=-70 EndZ=0
    g7: LineSegment StartX=-81.5 StartY=-70 StartZ=0 EndX=-81.5 EndY=-12 EndZ=0
    g8: LineSegment StartX=-81.5 StartY=-12 StartZ=0 EndX=-117.05 EndY=-12 EndZ=0
    g9: LineSegment StartX=-117.05 StartY=-12 StartZ=0 EndX=-117.05 EndY=-70 EndZ=0
    g10: GeomPoint [constr] X=-99.275 Y=-41 Z=0
    g11: LineSegment StartX=-68.5 StartY=-70 StartZ=0 EndX=-32.95 EndY=-70 EndZ=0
    g12: LineSegment StartX=-32.95 StartY=-70 StartZ=0 EndX=-32.95 EndY=-12 EndZ=0
    g13: LineSegment StartX=-32.95 StartY=-12 StartZ=0 EndX=-68.5 EndY=-12 EndZ=0
    g14: LineSegment StartX=-68.5 StartY=-12 StartZ=0 EndX=-68.5 EndY=-70 EndZ=0
    g15: GeomPoint [constr] X=-50.725 Y=-41 Z=0
  constraints (42):
    c: Vertical(g0)
    c: Vertical(g1)
    c: Vertical(g2)
    c: Vertical(g3)
    c: Symmetric(g0,g1,g4)
    c: Symmetric(g2,g3,g5)
    c: Coincident(g6,g7)
    c: Coincident(g7,g8)
    c: Coincident(g8,g9)
    c: Coincident(g9,g6)
    c: Horizontal(g6)
    c: Horizontal(g8)
    c: Vertical(g7)
    c: Vertical(g9)
    c: Symmetric(g8,g6,g10)
    c: Coincident(g10,g4)
    c: Coincident(g11,g12)
    c: Coincident(g12,g13)
    c: Coincident(g13,g14)
    c: Coincident(g14,g11)
    c: Horizontal(g11)
    c: Horizontal(g13)
    c: Vertical(g12)
    c: Vertical(g14)
    c: Symmetric(g13,g11,g15)
    c: Coincident(g15,g5)
    c: Equal(g13,g8)
    c: Equal(g7,g14)
    c: Distance(g0,g9) = 5
    c: PointOnObject(g0,g-5)
    c: PointOnObject(g1,g-5)
    c: PointOnObject(g2,g-5)
    c: PointOnObject(g3,g-5)
    c: PointOnObject(g3,g-6)
    c: PointOnObject(g2,g-6)
    c: PointOnObject(g1,g-6)
    c: PointOnObject(g-5,g0)
    c: PointOnObject(g1,g-7)
    c: PointOnObject(g2,g-8)
    c: PointOnObject(g3,g-4)
    c: Distance(g-5,g8) = 5
    c: Distance(g-6,g6) = 5
FEATURE [PartDesign::Pocket] Pocket021  label="PocketFrontVent"
  BaseFeature = -> Hole003
  Direction = (0,1,-2e-16)
  Length = 5
  Length2 = 5
  Profile = -> Sketch023
  ReferenceAxis = -> Sketch023 [N_Axis]
  Refine = true
  SideType = 0
  Suppressed = false
  Type = 1
  Type2 = 0
FEATURE [Sketcher::SketchObject] Sketch024  label="SketchSideVent"
  ArcFitTolerance = 1e-06
  AttachmentSupport = -> [Pocket021]
  ExternalGeometry = -> [Pocket021]
  ExternalTypes = [0,0]
  FullyConstrained = true
  MakeInternals = false
  MapMode = 5
  Placement = pos=(-25,0,0) rot=(0.57735,0.57735,0.57735;2.0944rad)
  sketch-geometry (8):
    g0: LineSegment [constr] StartX=61.425 StartY=-7 StartZ=0 EndX=61.425 EndY=-75 EndZ=0
    g1: LineSegment [constr] StartX=88.575 StartY=-75 StartZ=0 EndX=88.575 EndY=-7 EndZ=0
    g2: GeomPoint [constr] X=75 Y=-41 Z=0
    g3: LineSegment StartX=64.425 StartY=-72 StartZ=0 EndX=85.575 EndY=-72 EndZ=0
    g4: LineSegment StartX=85.575 StartY=-72 StartZ=0 EndX=85.575 EndY=-10 EndZ=0
    g5: LineSegment StartX=85.575 StartY=-10 StartZ=0 EndX=64.425 EndY=-10 EndZ=0
    g6: LineSegment StartX=64.425 StartY=-10 StartZ=0 EndX=64.425 EndY=-72 EndZ=0
    g7: GeomPoint [constr] X=75 Y=-41 Z=0
  constraints (19):
    c: Coincident(g0,g-3)
    c: Coincident(g1,g-4)
    c: Symmetric(g0,g1,g2)
    c: Coincident(g3,g4)
    c: Coincident(g4,g5)
    c: Coincident(g5,g6)
    c: Coincident(g6,g3)
    c: Horizontal(g3)
    c: Horizontal(g5)
    c: Vertical(g4)
    c: Vertical(g6)
    c: Symmetric(g5,g3,g7)
    c: Coincident(g7,g2)
    c: Distance(g-5,g5) = 3
    c: Distance(g1,g4) = 3
    c: PointOnObject(g1,g-6)
    c: PointOnObject(g0,g-6)
    c: Vertical(g0)
    c: Vertical(g1)
FEATURE [PartDesign::Pocket] Pocket022  label="PocketSideVent"
  BaseFeature = -> Pocket021
  Direction = (-1,0,0)
  Length = 5
  Length2 = 5
  Profile = -> Sketch024
  ReferenceAxis = -> Sketch024 [N_Axis]
  Refine = true
  SideType = 0
  Suppressed = false
  Type = 1
  Type2 = 0
FEATURE [PartDesign::Pad] Pad008  label="PadBottomHoles"
  BaseFeature = -> Pocket022
  Direction = (0,0,1)
  Length = 43
  Length2 = 10
  Profile = -> Pocket022 [Edge51,Edge52,Edge58,Edge57]
  Refine = true
  SideType = 0
  Suppressed = false
  Type = 0
  Type2 = 0
FEATURE [PartDesign::Fillet] Fillet  label="FilletJoints"
  Base = -> Pad008 [Edge118,Edge112,Edge114,Edge84,Edge83,Edge81,Edge79,Edge78,Edge76,Edge82,Edge116,Edge110,Edge108,Edge106,Edge87,Edge113,Edge111,Edge109,Edge107,Edge119,Edge117,Edge115,Edge19,Edge17,Edge15,Edge66,Edge18,Edge16,Edge14,Edge13,Edge60,Edge54,Edge3,Edge33,Edge69,Edge65,Edge62,Edge61,Edge32,Edge64,+4 more]
  BaseFeature = -> Pad008
  Radius = 1
  Refine = true
  SupportTransform = false
  Suppressed = false
  UseAllEdges = false
FEATURE [PartDesign::Fillet] Fillet013  label="FilletSides"
  Base = -> Fillet [Face4,Face12]
  BaseFeature = -> Fillet
  Radius = 1
  Refine = true
  SupportTransform = false
  Suppressed = false
  UseAllEdges = false
FEATURE [App::Point] Origin015  label="Origin020"
  Role = Origin
FEATURE [PartDesign::SubShapeBinder] Binder011  label="BinderPowerPanel"
  BindCopyOnChange = 0
  BindMode = 0
  ClaimChildren = false
  Context = -> Body006 [Binder011.]
  Fuse = false
  MakeFace = true
  OffsetFill = false
  OffsetIntersection = false
  OffsetJoinType = 0
  OffsetOpenResult = false
  PartialLoad = false
  Refine = true
  Relative = true
  Support = -> [Sketch]
  _Version = 2
FEATURE [Sketcher::SketchObject] Sketch025  label="SketchPowerPanel"
  ArcFitTolerance = 1e-06
  AttachmentSupport = -> [Origin014]
  ExternalGeometry = -> [Binder011]
  ExternalTypes = [0,0,0,0,0,0,0,0,0,0,0]
  FullyConstrained = true
  MakeInternals = false
  MapMode = 5
  sketch-geometry (5):
    g0: LineSegment StartX=25 StartY=50 StartZ=0 EndX=25 EndY=0 EndZ=0
    g1: GeomPoint X=30 Y=45 Z=0
    g2: GeomPoint X=30 Y=5 Z=0
    g3: GeomPoint X=120 Y=5 Z=0
    g4: GeomPoint X=120 Y=45 Z=0
  constraints (6):
    c: Coincident(g0,g-4)
    c: Coincident(g0,g-6)
    c: Coincident(g1,g-11)
    c: Coincident(g2,g-12)
    c: Coincident(g3,g-13)
    c: Coincident(g4,g-13)
FEATURE [PartDesign::Pad] Pad009  label="PadPowerPanel"
  Direction = (0,0,1)
  Length = 3
  Length2 = 10
  Profile = -> Sketch025
  ReferenceAxis = -> Sketch025 [N_Axis]
  Refine = true
  Reversed = true
  SideType = 0
  Suppressed = false
  Type = 0
  Type2 = 0
FEATURE [PartDesign::Hole] Hole007  label="HolePowerPanel"
  BaseFeature = -> Pad009
  BaseProfileType = 7
  CustomThreadClearance = 0
  Depth = 25
  DepthType = 0
  Diameter = 4.5
  DrillForDepth = false
  DrillPoint = 1
  DrillPointAngle = 118
  HoleCutCountersinkAngle = 90
  HoleCutCustomValues = false
  HoleCutDepth = 4
  HoleCutDiameter = 8
  HoleCutType = 2
  ModelThread = false
  Profile = -> Sketch025 [Vertex8,Vertex9,Vertex10,Vertex11]
  Refine = true
  Suppressed = false
  Tapered = false
  TaperedAngle = 90
  ThreadClass = 0
  ThreadDepth = 25
  ThreadDepthType = 0
  ThreadDiameter = 4
  ThreadDirection = 0
  ThreadFit = 0
  ThreadSize = 11
  ThreadType = 1
  Threaded = false
  UseCustomThreadClearance = false
FEATURE [PartDesign::Fillet] Fillet015
  Base = -> Hole007 [Face9,Face11,Face12]
  BaseFeature = -> Hole007
  Radius = 1
  Refine = true
  SupportTransform = false
  Suppressed = false
  UseAllEdges = false
FEATURE [PartDesign::Body] Body006  label="PowerPanelTop"
  AllowCompound = true
  Group = -> [Binder011,Sketch025,Pad009,Hole007,Fillet015]
  Origin = -> Origin014
  Tip = -> Fillet015
FEATURE [App::Link] Connector5Way003
  LinkPlacement = pos=(56.8132,57.3188,-85.6169) rot=(0.688247,-0.688247,-0.229416;0rad)
  LinkedObject = -> <external Joints.FCStd>#Body001
  Placement = pos=(56.8132,57.3188,-85.6169) rot=(0.688247,-0.688247,-0.229416;0rad)
FEATURE [App::Link] Pole85mm
  LinkPlacement = pos=(57.1132,57.3188,-85.6169) rot=(0.688247,-0.688247,-0.229416;0rad)
  LinkedObject = -> <external Joints.FCStd>#Body003
  Placement = pos=(57.1132,57.3188,-85.6169) rot=(0.688247,-0.688247,-0.229416;0rad)
FEATURE [App::Point] Origin017  label="Origin022"
  Role = Origin
FEATURE [PartDesign::SubShapeBinder] Binder012  label="BinderCenterPanelBottom"
  BindCopyOnChange = 0
  BindMode = 0
  ClaimChildren = false
  Context = -> Body007 [Binder012.]
  Fuse = false
  MakeFace = true
  OffsetFill = false
  OffsetIntersection = false
  OffsetJoinType = 0
  OffsetOpenResult = false
  PartialLoad = false
  Refine = true
  Relative = true
  Support = -> [Sketch]
  _Version = 2
FEATURE [PartDesign::Fillet] Fillet016
  Base = -> Fillet013 [Face13,Face69,Face57,Face135,Face56,Edge205,Face120,Face119,Face122,Face90,Face58,Face123,Face124,Face126,Face125,Face10,Face64,Face61,Face62,Face63,Face1,Face7,Face8,Face9,Face6,Face52,Face31,Face98,Face97,Face117,Face118,Face95,Face96,Face116,Face115]
  BaseFeature = -> Fillet013
  Radius = 0.95
  Refine = true
  SupportTransform = false
  Suppressed = false
  UseAllEdges = false
FEATURE [PartDesign::Body] Body002  label="Switch Bottom"
  AllowCompound = true
  Group = -> [Binder002,Pad003,Binder003,Sketch006,Pocket004,Sketch007,Pocket005,Pocket006,Pocket007,Sketch008,Pocket008,Sketch009,Pocket009,Hole003,Sketch023,Pocket021,Sketch024,Pocket022,Pad008,Fillet,Fillet013,Fillet016]
  Origin = -> Origin004
  Tip = -> Fillet016
FEATURE [App::Point] Origin019  label="Origin025"
  Role = Origin
FEATURE [PartDesign::SubShapeBinder] Binder014  label="BinderCenterPanelTop"
  BindCopyOnChange = 0
  BindMode = 0
  ClaimChildren = false
  Context = -> Body008 [Binder014.]
  Fuse = false
  MakeFace = true
  OffsetFill = false
  OffsetIntersection = false
  OffsetJoinType = 0
  OffsetOpenResult = false
  PartialLoad = false
  Refine = true
  Relative = true
  Support = -> [Body007[Sketch026.]]
  _Version = 2
FEATURE [Sketcher::SketchObject] Sketch031  label="SketchCenterPanelTop"
  ArcFitTolerance = 1e-06
  AttachmentSupport = -> [Origin018]
  ExternalGeometry = -> [Binder014]
  ExternalTypes = [0]
  FullyConstrained = true
  MakeInternals = false
  MapMode = 5
  sketch-geometry (9):
    g0: LineSegment [constr] StartX=-20 StartY=-95 StartZ=0 EndX=20 EndY=-95 EndZ=0
    g1: LineSegment [constr] StartX=20 StartY=-95 StartZ=0 EndX=20 EndY=95 EndZ=0
    g2: LineSegment [constr] StartX=20 StartY=95 StartZ=0 EndX=-20 EndY=95 EndZ=0
    g3: LineSegment [constr] StartX=-20 StartY=95 StartZ=0 EndX=-20 EndY=-95 EndZ=0
    g4: GeomPoint [constr] X=0 Y=0 Z=0
    g5: GeomPoint X=-20 Y=95 Z=0
    g6: GeomPoint X=20 Y=95 Z=0
    g7: GeomPoint X=20 Y=-95 Z=0
    g8: GeomPoint X=-20 Y=-95 Z=0
  constraints (16):
    c: Coincident(g0,g1)
    c: Coincident(g1,g2)
    c: Coincident(g2,g3)
    c: Coincident(g3,g0)
    c: Horizontal(g0)
    c: Horizontal(g2)
    c: Vertical(g1)
    c: Vertical(g3)
    c: Symmetric(g2,g0,g4)
    c: Coincident(g4,g-1)
    c: Distance(g-6,g2) = 5
    c: Distance(g-5,g1) = 5
    c: Coincident(g5,g2)
    c: Coincident(g6,g1)
    c: Coincident(g7,g0)
    c: Coincident(g8,g0)
FEATURE [PartDesign::Pad] Pad011  label="PadCenterPanelTop"
  Direction = (0,0,1)
  Length = 3
  Length2 = 10
  Profile = -> Sketch031
  ReferenceAxis = -> Sketch031 [N_Axis]
  Refine = true
  Reversed = true
  SideType = 0
  Suppressed = false
  Type = 0
  Type2 = 0
FEATURE [PartDesign::Hole] Hole009
  BaseFeature = -> Pad011
  BaseProfileType = 7
  CustomThreadClearance = 0
  Depth = 25
  DepthType = 0
  Diameter = 4.5
  DrillForDepth = false
  DrillPoint = 1
  DrillPointAngle = 118
  HoleCutCountersinkAngle = 90
  HoleCutCustomValues = false
  HoleCutDepth = 4
  HoleCutDiameter = 8
  HoleCutType = 2
  ModelThread = false
  Profile = -> Sketch031 [Vertex5,Vertex6,Vertex7,Vertex8]
  Refine = true
  Suppressed = false
  Tapered = false
  TaperedAngle = 90
  ThreadClass = 0
  ThreadDepth = 25
  ThreadDepthType = 0
  ThreadDiameter = 4
  ThreadDirection = 0
  ThreadFit = 0
  ThreadSize = 11
  ThreadType = 1
  Threaded = false
  UseCustomThreadClearance = false
FEATURE [Sketcher::SketchObject] Sketch032  label="SketchCenterPanelBottom"
  ArcFitTolerance = 1e-06
  AttachmentSupport = -> [Origin016]
  ExternalGeometry = -> [Binder012]
  ExternalTypes = [0,0,0,0,0,0]
  FullyConstrained = true
  MakeInternals = false
  MapMode = 5
  sketch-geometry (13):
    g0: LineSegment StartX=-25 StartY=100 StartZ=0 EndX=-25 EndY=-100 EndZ=0
    g1: LineSegment StartX=-25 StartY=-100 StartZ=0 EndX=25 EndY=-100 EndZ=0
    g2: LineSegment StartX=25 StartY=-100 StartZ=0 EndX=25 EndY=100 EndZ=0
    g3: LineSegment StartX=25 StartY=100 StartZ=0 EndX=-25 EndY=100 EndZ=0
    g4: LineSegment [constr] StartX=-20 StartY=-95 StartZ=0 EndX=20 EndY=-95 EndZ=0
    g5: LineSegment [constr] StartX=20 StartY=-95 StartZ=0 EndX=20 EndY=95 EndZ=0
    g6: LineSegment [constr] StartX=20 StartY=95 StartZ=0 EndX=-20 EndY=95 EndZ=0
    g7: LineSegment [constr] StartX=-20 StartY=95 StartZ=0 EndX=-20 EndY=-95 EndZ=0
    g8: GeomPoint [constr] X=0 Y=0 Z=0
    g9: GeomPoint X=-20 Y=95 Z=0
    g10: GeomPoint X=20 Y=95 Z=0
    g11: GeomPoint X=20 Y=-95 Z=0
    g12: GeomPoint X=-20 Y=-95 Z=0
  constraints (26):
    c: Coincident(g0,g1)
    c: Coincident(g1,g2)
    c: Coincident(g2,g3)
    c: Coincident(g3,g0)
    c: Vertical(g0)
    c: Vertical(g2)
    c: Horizontal(g1)
    c: Horizontal(g3)
    c: Coincident(g0,g-7)
    c: Coincident(g1,g-8)
    c: Coincident(g4,g5)
    c: Coincident(g5,g6)
    c: Coincident(g6,g7)
    c: Coincident(g7,g4)
    c: Horizontal(g4)
    c: Horizontal(g6)
    c: Vertical(g5)
    c: Vertical(g7)
    c: Symmetric(g6,g4,g8)
    c: Coincident(g8,g-1)
    c: Distance(g3,g6) = 5
    c: Distance(g2,g5) = 5
    c: Coincident(g9,g6)
    c: Coincident(g10,g5)
    c: Coincident(g11,g4)
    c: Coincident(g12,g4)
FEATURE [PartDesign::Pad] Pad012  label="PadCenterPanelBottom"
  Direction = (0,0,1)
  Length = 20
  Length2 = 10
  Profile = -> Sketch032
  ReferenceAxis = -> Sketch032 [N_Axis]
  Refine = true
  Reversed = true
  SideType = 0
  Suppressed = false
  Type = 0
  Type2 = 0
FEATURE [PartDesign::Pad] Pad006  label="PadBody002"
  Direction = (0,0,1)
  Length = 3
  Length2 = 10
  Profile = -> Sketch017
  ReferenceAxis = -> Sketch017 [N_Axis]
  Refine = true
  SideType = 0
  Suppressed = false
  Type = 0
  Type2 = 0
FEATURE [Sketcher::SketchObject] Sketch033  label="SketchCenterPanelBottomJoints"
  ArcFitTolerance = 1e-06
  AttachmentSupport = -> [Pad012]
  ExternalGeometry = -> [Sketch032]
  ExternalTypes = [0,0,0,0]
  FullyConstrained = true
  MakeInternals = false
  MapMode = 5
  sketch-geometry (40):
    g0: GeomPoint [constr] X=-1.3e-15 Y=100 Z=0
    g1: GeomPoint [constr] X=-4e-16 Y=-100 Z=0
    g2: LineSegment [constr] StartX=-1.5 StartY=100 StartZ=0 EndX=-1.5 EndY=97 EndZ=0
    g3: LineSegment [constr] StartX=-1.5 StartY=97 StartZ=0 EndX=1.5 EndY=97 EndZ=0
    g4: LineSegment [constr] StartX=1.5 StartY=97 StartZ=0 EndX=1.5 EndY=100 EndZ=0
    g5: LineSegment [constr] StartX=1.5 StartY=100 StartZ=0 EndX=-1.5 EndY=100 EndZ=0
    g6: LineSegment [constr] StartX=-4.5 StartY=97 StartZ=0 EndX=-4.5 EndY=94 EndZ=0
    g7: LineSegment [constr] StartX=-4.5 StartY=94 StartZ=0 EndX=4.5 EndY=94 EndZ=0
    g8: LineSegment [constr] StartX=4.5 StartY=94 StartZ=0 EndX=4.5 EndY=97 EndZ=0
    g9: LineSegment [constr] StartX=4.5 StartY=97 StartZ=0 EndX=-4.5 EndY=97 EndZ=0
    g10: GeomPoint [constr] X=-1.3e-15 Y=97 Z=0
    g11: GeomPoint [constr] X=-1.3e-15 Y=97 Z=0
    g12: GeomPoint [constr] X=-1.3e-15 Y=100 Z=0
    g13: LineSegment [constr] StartX=1.5 StartY=-100 StartZ=0 EndX=1.5 EndY=-97 EndZ=0
    g14: LineSegment [constr] StartX=1.5 StartY=-97 StartZ=0 EndX=-1.5 EndY=-97 EndZ=0
    g15: LineSegment [constr] StartX=-1.5 StartY=-97 StartZ=0 EndX=-1.5 EndY=-100 EndZ=0
    g16: LineSegment [constr] StartX=-1.5 StartY=-100 StartZ=0 EndX=1.5 EndY=-100 EndZ=0
    g17: LineSegment [constr] StartX=4.5 StartY=-97 StartZ=0 EndX=4.5 EndY=-94 EndZ=0
    g18: LineSegment [constr] StartX=4.5 StartY=-94 StartZ=0 EndX=-4.5 EndY=-94 EndZ=0
    g19: LineSegment [constr] StartX=-4.5 StartY=-94 StartZ=0 EndX=-4.5 EndY=-97 EndZ=0
    g20: LineSegment [constr] StartX=-4.5 StartY=-97 StartZ=0 EndX=4.5 EndY=-97 EndZ=0
    g21: GeomPoint [constr] X=-4e-16 Y=-97 Z=0
    g22: GeomPoint [constr] X=-4e-16 Y=-97 Z=0
    g23: GeomPoint [constr] X=-4e-16 Y=-100 Z=0
    g24: LineSegment StartX=-1.5 StartY=100 StartZ=0 EndX=1.5 EndY=100 EndZ=0
    g25: LineSegment StartX=1.5 StartY=100 StartZ=0 EndX=1.5 EndY=97 EndZ=0
    g26: LineSegment StartX=1.5 StartY=97 StartZ=0 EndX=4.5 EndY=97 EndZ=0
    g27: LineSegment StartX=4.5 StartY=97 StartZ=0 EndX=4.5 EndY=94 EndZ=0
    g28: LineSegment StartX=4.5 StartY=94 StartZ=0 EndX=-4.5 EndY=94 EndZ=0
    g29: LineSegment StartX=-4.5 StartY=94 StartZ=0 EndX=-4.5 EndY=97 EndZ=0
    g30: LineSegment StartX=-4.5 StartY=97 StartZ=0 EndX=-1.5 EndY=97 EndZ=0
    g31: LineSegment StartX=-1.5 StartY=97 StartZ=0 EndX=-1.5 EndY=100 EndZ=0
    g32: LineSegment StartX=-4.5 StartY=-94 StartZ=0 EndX=4.5 EndY=-94 EndZ=0
    g33: LineSegment StartX=4.5 StartY=-94 StartZ=0 EndX=4.5 EndY=-97 EndZ=0
    g34: LineSegment StartX=4.5 StartY=-97 StartZ=0 EndX=1.5 EndY=-97 EndZ=0
    g35: LineSegment StartX=1.5 StartY=-97 StartZ=0 EndX=1.5 EndY=-100 EndZ=0
    g36: LineSegment StartX=1.5 StartY=-100 StartZ=0 EndX=-1.5 EndY=-100 EndZ=0
    g37: LineSegment StartX=-1.5 StartY=-100 StartZ=0 EndX=-1.5 EndY=-97 EndZ=0
    g38: LineSegment StartX=-1.5 StartY=-97 StartZ=0 EndX=-4.5 EndY=-97 EndZ=0
    g39: LineSegment StartX=-4.5 StartY=-97 StartZ=0 EndX=-4.5 EndY=-94 EndZ=0
  constraints (84):
    c: Symmetric(g-6,g-6,g1)
    c: Symmetric(g-4,g-5,g0)
    c: Coincident(g2,g3)
    c: Coincident(g3,g4)
    c: Coincident(g4,g5)
    c: Coincident(g5,g2)
    c: Vertical(g2)
    c: Vertical(g4)
    c: Horizontal(g3)
    c: Horizontal(g5)
    c: Distance(g2,g4) = 3
    c: Distance(g3,g5) = 3
    c: Coincident(g6,g7)
    c: Coincident(g7,g8)
    c: Coincident(g8,g9)
    c: Coincident(g9,g6)
    c: Vertical(g6)
    c: Vertical(g8)
    c: Horizontal(g7)
    c: Horizontal(g9)
    c: Distance(g6,g8) = 9
    c: Distance(g7,g9) = 3
    c: Symmetric(g6,g8,g10)
    c: Symmetric(g2,g3,g11)
    c: Symmetric(g2,g4,g12)
    c: Coincident(g11,g10)
    c: Coincident(g13,g14)
    c: Coincident(g14,g15)
    c: Coincident(g15,g16)
    c: Coincident(g16,g13)
    c: Distance(g13,g15) = 3
    c: Distance(g14,g16) = 3
    c: Coincident(g17,g18)
    c: Coincident(g18,g19)
    c: Coincident(g19,g20)
    c: Coincident(g20,g17)
    c: Distance(g17,g19) = 9
    c: Distance(g18,g20) = 3
    c: Symmetric(g17,g19,g21)
    c: Symmetric(g13,g14,g22)
    c: Symmetric(g13,g15,g23)
    c: Coincident(g22,g21)
    c: Horizontal(g18)
    c: Horizontal(g20)
    c: Vertical(g17)
    c: Vertical(g19)
    c: Vertical(g15)
    c: Vertical(g13)
    c: Horizontal(g14)
    c: Horizontal(g16)
    c: Coincident(g12,g0)
    c: Coincident(g23,g1)
    c: Coincident(g24,g2)
    c: Coincident(g24,g4)
    c: Coincident(g25,g4)
    c: Coincident(g25,g3)
    c: Coincident(g26,g3)
    c: Coincident(g26,g8)
    c: Coincident(g27,g8)
    c: Coincident(g27,g7)
    c: Coincident(g28,g7)
    c: Coincident(g28,g6)
    c: Coincident(g29,g6)
    c: Coincident(g29,g6)
    c: Coincident(g30,g6)
    c: Coincident(g30,g2)
    c: Coincident(g31,g2)
    c: Coincident(g31,g2)
    c: Coincident(g32,g18)
    c: Coincident(g32,g17)
    c: Coincident(g33,g17)
    c: Coincident(g33,g17)
    c: Coincident(g34,g17)
    c: Coincident(g34,g13)
    c: Coincident(g35,g13)
    c: Coincident(g35,g13)
    c: Coincident(g36,g13)
    c: Coincident(g36,g15)
    c: Coincident(g37,g15)
    c: Coincident(g37,g14)
    c: Coincident(g38,g14)
    c: Coincident(g38,g19)
    c: Coincident(g39,g19)
    c: Coincident(g39,g18)
FEATURE [PartDesign::Pocket] Pocket023  label="PocketCenterPanelBottomJoints"
  BaseFeature = -> Pad012
  Direction = (0,0,-1)
  Length = 5
  Length2 = 5
  Profile = -> Sketch033
  ReferenceAxis = -> Sketch033 [N_Axis]
  Refine = true
  SideType = 0
  Suppressed = false
  Type = 1
  Type2 = 0
FEATURE [Sketcher::SketchObject] Sketch034  label="SketchCenterPanelBottomMidJoints"
  ArcFitTolerance = 1e-06
  AttachmentSupport = -> [Pocket023]
  ExternalGeometry = -> [Sketch032]
  ExternalTypes = [0,0,0,0]
  FullyConstrained = true
  MakeInternals = false
  MapMode = 5
  sketch-geometry (84):
    g0: GeomPoint [constr] X=-1.6e-15 Y=100 Z=0
    g1: GeomPoint [constr] X=0 Y=-100 Z=0
    g2: LineSegment [constr] StartX=0 StartY=-100 StartZ=0 EndX=-1.6e-15 EndY=100 EndZ=0
    g3: LineSegment [constr] StartX=-1.5 StartY=52.8 StartZ=0 EndX=-1.5 EndY=47.2 EndZ=0
    g4: LineSegment [constr] StartX=-1.5 StartY=47.2 StartZ=0 EndX=1.5 EndY=47.2 EndZ=0
    g5: LineSegment [constr] StartX=1.5 StartY=47.2 StartZ=0 EndX=1.5 EndY=52.8 EndZ=0
    g6: LineSegment [constr] StartX=1.5 StartY=52.8 StartZ=0 EndX=-1.5 EndY=52.8 EndZ=0
    g7: LineSegment [constr] StartX=-4.5 StartY=47.2 StartZ=0 EndX=-4.5 EndY=44.2 EndZ=0
    g8: LineSegment [constr] StartX=-4.5 StartY=44.2 StartZ=0 EndX=4.5 EndY=44.2 EndZ=0
    g9: LineSegment [constr] StartX=4.5 StartY=44.2 StartZ=0 EndX=4.5 EndY=47.2 EndZ=0
    g10: LineSegment [constr] StartX=4.5 StartY=47.2 StartZ=0 EndX=-4.5 EndY=47.2 EndZ=0
    g11: LineSegment [constr] StartX=-4.5 StartY=55.8 StartZ=0 EndX=-4.5 EndY=52.8 EndZ=0
    g12: LineSegment [constr] StartX=-4.5 StartY=52.8 StartZ=0 EndX=4.5 EndY=52.8 EndZ=0
    g13: LineSegment [constr] StartX=4.5 StartY=52.8 StartZ=0 EndX=4.5 EndY=55.8 EndZ=0
    g14: LineSegment [constr] StartX=4.5 StartY=55.8 StartZ=0 EndX=-4.5 EndY=55.8 EndZ=0
    g15: GeomPoint [constr] X=1.7e-15 Y=52.8 Z=0
    g16: GeomPoint [constr] X=1.7e-15 Y=47.2 Z=0
    g17: LineSegment [constr] StartX=-1.5 StartY=2.8 StartZ=0 EndX=-1.5 EndY=-2.8 EndZ=0
    g18: LineSegment [constr] StartX=-1.5 StartY=-2.8 StartZ=0 EndX=1.5 EndY=-2.8 EndZ=0
    g19: LineSegment [constr] StartX=1.5 StartY=-2.8 StartZ=0 EndX=1.5 EndY=2.8 EndZ=0
    g20: LineSegment [constr] StartX=1.5 StartY=2.8 StartZ=0 EndX=-1.5 EndY=2.8 EndZ=0
    g21: LineSegment [constr] StartX=-4.5 StartY=-2.8 StartZ=0 EndX=-4.5 EndY=-5.8 EndZ=0
    g22: LineSegment [constr] StartX=-4.5 StartY=-5.8 StartZ=0 EndX=4.5 EndY=-5.8 EndZ=0
    g23: LineSegment [constr] StartX=4.5 StartY=-5.8 StartZ=0 EndX=4.5 EndY=-2.8 EndZ=0
    g24: LineSegment [constr] StartX=4.5 StartY=-2.8 StartZ=0 EndX=-4.5 EndY=-2.8 EndZ=0
    g25: LineSegment [constr] StartX=-4.5 StartY=5.8 StartZ=0 EndX=-4.5 EndY=2.8 EndZ=0
    g26: LineSegment [constr] StartX=-4.5 StartY=2.8 StartZ=0 EndX=4.5 EndY=2.8 EndZ=0
    g27: LineSegment [constr] StartX=4.5 StartY=2.8 StartZ=0 EndX=4.5 EndY=5.8 EndZ=0
    g28: LineSegment [constr] StartX=4.5 StartY=5.8 StartZ=0 EndX=-4.5 EndY=5.8 EndZ=0
    g29: GeomPoint [constr] X=-1e-15 Y=2.8 Z=0
    g30: GeomPoint [constr] X=-1e-15 Y=-2.8 Z=0
    g31: LineSegment [constr] StartX=-1.5 StartY=-47.2 StartZ=0 EndX=-1.5 EndY=-52.8 EndZ=0
    g32: LineSegment [constr] StartX=-1.5 StartY=-52.8 StartZ=0 EndX=1.5 EndY=-52.8 EndZ=0
    g33: LineSegment [constr] StartX=1.5 StartY=-52.8 StartZ=0 EndX=1.5 EndY=-47.2 EndZ=0
    g34: LineSegment [constr] StartX=1.5 StartY=-47.2 StartZ=0 EndX=-1.5 EndY=-47.2 EndZ=0
    g35: LineSegment [constr] StartX=-4.5 StartY=-52.8 StartZ=0 EndX=-4.5 EndY=-55.8 EndZ=0
    g36: LineSegment [constr] StartX=-4.5 StartY=-55.8 StartZ=0 EndX=4.5 EndY=-55.8 EndZ=0
    g37: LineSegment [constr] StartX=4.5 StartY=-55.8 StartZ=0 EndX=4.5 EndY=-52.8 EndZ=0
    g38: LineSegment [constr] StartX=4.5 StartY=-52.8 StartZ=0 EndX=-4.5 EndY=-52.8 EndZ=0
    g39: LineSegment [constr] StartX=-4.5 StartY=-44.2 StartZ=0 EndX=-4.5 EndY=-47.2 EndZ=0
    g40: LineSegment [constr] StartX=-4.5 StartY=-47.2 StartZ=0 EndX=4.5 EndY=-47.2 EndZ=0
    g41: LineSegment [constr] StartX=4.5 StartY=-47.2 StartZ=0 EndX=4.5 EndY=-44.2 EndZ=0
    g42: LineSegment [constr] StartX=4.5 StartY=-44.2 StartZ=0 EndX=-4.5 EndY=-44.2 EndZ=0
    g43: GeomPoint [constr] X=-5e-16 Y=-47.2 Z=0
    g44: GeomPoint [constr] X=-5e-16 Y=-52.8 Z=0
    g45: GeomPoint [constr] X=-1.2e-15 Y=50 Z=0
    g46: GeomPoint [constr] X=-8e-16 Y=-1.7e-15 Z=0
    g47: GeomPoint [constr] X=-4e-16 Y=-50 Z=0
    g48: LineSegment StartX=-4.5 StartY=55.8 StartZ=0 EndX=4.5 EndY=55.8 EndZ=0
    g49: LineSegment StartX=4.5 StartY=55.8 StartZ=0 EndX=4.5 EndY=52.8 EndZ=0
    g50: LineSegment StartX=4.5 StartY=52.8 StartZ=0 EndX=1.5 EndY=52.8 EndZ=0
    g51: LineSegment StartX=1.5 StartY=52.8 StartZ=0 EndX=1.5 EndY=47.2 EndZ=0
    g52: LineSegment StartX=1.5 StartY=47.2 StartZ=0 EndX=4.5 EndY=47.2 EndZ=0
    g53: LineSegment StartX=4.5 StartY=47.2 StartZ=0 EndX=4.5 EndY=44.2 EndZ=0
    g54: LineSegment StartX=4.5 StartY=44.2 StartZ=0 EndX=-4.5 EndY=44.2 EndZ=0
    g55: LineSegment StartX=-4.5 StartY=44.2 StartZ=0 EndX=-4.5 EndY=47.2 EndZ=0
    g56: LineSegment StartX=-4.5 StartY=47.2 StartZ=0 EndX=-1.5 EndY=47.2 EndZ=0
    g57: LineSegment StartX=-1.5 StartY=47.2 StartZ=0 EndX=-1.5 EndY=52.8 EndZ=0
    g58: LineSegment StartX=-1.5 StartY=52.8 StartZ=0 EndX=-4.5 EndY=52.8 EndZ=0
    g59: LineSegment StartX=-4.5 StartY=52.8 StartZ=0 EndX=-4.5 EndY=55.8 EndZ=0
    g60: LineSegment StartX=-4.5 StartY=5.8 StartZ=0 EndX=4.5 EndY=5.8 EndZ=0
    g61: LineSegment StartX=4.5 StartY=5.8 StartZ=0 EndX=4.5 EndY=2.8 EndZ=0
    g62: LineSegment StartX=4.5 StartY=2.8 StartZ=0 EndX=1.5 EndY=2.8 EndZ=0
    g63: LineSegment StartX=1.5 StartY=2.8 StartZ=0 EndX=1.5 EndY=-2.8 EndZ=0
    g64: LineSegment StartX=1.5 StartY=-2.8 StartZ=0 EndX=4.5 EndY=-2.8 EndZ=0
    g65: LineSegment StartX=4.5 StartY=-2.8 StartZ=0 EndX=4.5 EndY=-5.8 EndZ=0
    g66: LineSegment StartX=4.5 StartY=-5.8 StartZ=0 EndX=-4.5 EndY=-5.8 EndZ=0
    g67: LineSegment StartX=-4.5 StartY=-5.8 StartZ=0 EndX=-4.5 EndY=-2.8 EndZ=0
    g68: LineSegment StartX=-4.5 StartY=-2.8 StartZ=0 EndX=-1.5 EndY=-2.8 EndZ=0
    g69: LineSegment StartX=-1.5 StartY=-2.8 StartZ=0 EndX=-1.5 EndY=2.8 EndZ=0
    g70: LineSegment StartX=-1.5 StartY=2.8 StartZ=0 EndX=-4.5 EndY=2.8 EndZ=0
    g71: LineSegment StartX=-4.5 StartY=2.8 StartZ=0 EndX=-4.5 EndY=5.8 EndZ=0
    g72: LineSegment StartX=4.5 StartY=-44.2 StartZ=0 EndX=4.5 EndY=-47.2 EndZ=0
    g73: LineSegment StartX=4.5 StartY=-47.2 StartZ=0 EndX=1.5 EndY=-47.2 EndZ=0
    g74: LineSegment StartX=1.5 StartY=-47.2 StartZ=0 EndX=1.5 EndY=-52.8 EndZ=0
    g75: LineSegment StartX=1.5 StartY=-52.8 StartZ=0 EndX=4.5 EndY=-52.8 EndZ=0
    g76: LineSegment StartX=4.5 StartY=-52.8 StartZ=0 EndX=4.5 EndY=-55.8 EndZ=0
    g77: LineSegment StartX=4.5 StartY=-55.8 StartZ=0 EndX=-4.5 EndY=-55.8 EndZ=0
    g78: LineSegment StartX=-4.5 StartY=-55.8 StartZ=0 EndX=-4.5 EndY=-52.8 EndZ=0
    g79: LineSegment StartX=-4.5 StartY=-52.8 StartZ=0 EndX=-1.5 EndY=-52.8 EndZ=0
    g80: LineSegment StartX=-1.5 StartY=-52.8 StartZ=0 EndX=-1.5 EndY=-47.2 EndZ=0
    g81: LineSegment StartX=-1.5 StartY=-47.2 StartZ=0 EndX=-4.5 EndY=-47.2 EndZ=0
    g82: LineSegment StartX=-4.5 StartY=-47.2 StartZ=0 EndX=-4.5 EndY=-44.2 EndZ=0
    g83: LineSegment StartX=-4.5 StartY=-44.2 StartZ=0 EndX=4.5 EndY=-44.2 EndZ=0
  constraints (187):
    c: Symmetric(g-4,g-5,g0)
    c: Symmetric(g-6,g-6,g1)
    c: Coincident(g2,g1)
    c: Coincident(g2,g0)
    c: Coincident(g3,g4)
    c: Coincident(g4,g5)
    c: Coincident(g5,g6)
    c: Coincident(g6,g3)
    c: Vertical(g3)
    c: Vertical(g5)
    c: Horizontal(g4)
    c: Horizontal(g6)
    c: Distance(g3,g5) = 3
    c: Distance(g4,g6) = 5.6
    c: Coincident(g7,g8)
    c: Coincident(g8,g9)
    c: Coincident(g9,g10)
    c: Coincident(g10,g7)
    c: Vertical(g7)
    c: Vertical(g9)
    c: Horizontal(g8)
    c: Horizontal(g10)
    c: Distance(g7,g9) = 9
    c: Distance(g8,g10) = 3
    c: Coincident(g11,g12)
    c: Coincident(g12,g13)
    c: Coincident(g13,g14)
    c: Coincident(g14,g11)
    c: Vertical(g11)
    c: Vertical(g13)
    c: Horizontal(g12)
    c: Horizontal(g14)
    c: Distance(g11,g13) = 9
    c: Distance(g12,g14) = 3
    c: Symmetric(g3,g4,g16)
    c: Symmetric(g3,g5,g15)
    c: Symmetric(g7,g9,g16)
    c: Symmetric(g11,g12,g15)
    c: Coincident(g17,g18)
    c: Coincident(g31,g32)
    c: Coincident(g18,g19)
    c: Coincident(g32,g33)
    c: Coincident(g19,g20)
    c: Coincident(g33,g34)
    c: Coincident(g20,g17)
    c: Coincident(g34,g31)
    c: Vertical(g17)
    c: Vertical(g31)
    c: Vertical(g19)
    c: Vertical(g33)
    c: Horizontal(g18)
    c: Horizontal(g32)
    c: Horizontal(g20)
    c: Horizontal(g34)
    c: Distance(g17,g19) = 3
    c: Distance(g31,g33) = 3
    c: Distance(g18,g20) = 5.6
    c: Distance(g32,g34) = 5.6
    c: Coincident(g21,g22)
    c: Coincident(g35,g36)
    c: Coincident(g22,g23)
    c: Coincident(g36,g37)
    c: Coincident(g23,g24)
    c: Coincident(g37,g38)
    c: Coincident(g24,g21)
    c: Coincident(g38,g35)
    c: Vertical(g21)
    c: Vertical(g35)
    c: Vertical(g23)
    c: Vertical(g37)
    c: Horizontal(g22)
    c: Horizontal(g36)
    c: Horizontal(g24)
    c: Horizontal(g38)
    c: Distance(g21,g23) = 9
    c: Distance(g35,g37) = 9
    c: Distance(g22,g24) = 3
    c: Distance(g36,g38) = 3
    c: Coincident(g25,g26)
    c: Coincident(g39,g40)
    c: Coincident(g26,g27)
    c: Coincident(g40,g41)
    c: Coincident(g27,g28)
    c: Coincident(g41,g42)
    c: Coincident(g28,g25)
    c: Coincident(g42,g39)
    c: Vertical(g25)
    c: Vertical(g39)
    c: Vertical(g27)
    c: Vertical(g41)
    c: Horizontal(g26)
    c: Horizontal(g40)
    c: Horizontal(g28)
    c: Horizontal(g42)
    c: Distance(g25,g27) = 9
    c: Distance(g39,g41) = 9
    c: Distance(g26,g28) = 3
    c: Distance(g40,g42) = 3
    c: Symmetric(g17,g18,g30)
    c: Symmetric(g31,g32,g44)
    c: Symmetric(g17,g19,g29)
    c: Symmetric(g31,g33,g43)
    c: Symmetric(g21,g23,g30)
    c: Symmetric(g35,g37,g44)
    c: Symmetric(g25,g26,g29)
    c: Symmetric(g39,g40,g43)
    c: Symmetric(g3,g5,g45)
    c: PointOnObject(g45,g2)
    c: Distance(g45,g-4) = 50
    c: Symmetric(g17,g19,g46)
    c: Symmetric(g31,g33,g47)
    c: PointOnObject(g46,g2)
    c: PointOnObject(g47,g2)
    c: Distance(g46,g45) = 50
    c: DistanceY(g47,g46) = 50
    c: Coincident(g48,g11)
    c: Coincident(g48,g13)
    c: Coincident(g49,g13)
    c: Coincident(g49,g12)
    c: Coincident(g50,g12)
    c: Coincident(g50,g5)
    c: Coincident(g51,g5)
    c: Coincident(g51,g4)
    c: Coincident(g52,g4)
    c: Coincident(g52,g9)
    c: Coincident(g53,g9)
    c: Coincident(g53,g8)
    c: Coincident(g54,g8)
    c: Coincident(g54,g7)
    c: Coincident(g55,g7)
    c: Coincident(g55,g7)
    c: Coincident(g56,g7)
    c: Coincident(g56,g3)
    c: Coincident(g57,g3)
    c: Coincident(g57,g3)
    c: Coincident(g58,g3)
    c: Coincident(g58,g11)
    c: Coincident(g59,g11)
    c: Coincident(g59,g11)
    c: Coincident(g60,g25)
    c: Coincident(g60,g27)
    c: Coincident(g61,g27)
    c: Coincident(g61,g26)
    c: Coincident(g62,g26)
    c: Coincident(g62,g19)
    c: Coincident(g63,g19)
    c: Coincident(g63,g18)
    c: Coincident(g64,g18)
    c: Coincident(g64,g23)
    c: Coincident(g65,g23)
    c: Coincident(g65,g22)
    c: Coincident(g66,g22)
    c: Coincident(g66,g21)
    c: Coincident(g67,g21)
    c: Coincident(g67,g21)
    c: Coincident(g68,g21)
    c: Coincident(g68,g17)
    c: Coincident(g69,g17)
    c: Coincident(g69,g17)
    c: Coincident(g70,g17)
    c: Coincident(g70,g25)
    c: Coincident(g71,g25)
    c: Coincident(g71,g25)
    c: Coincident(g72,g41)
    c: Coincident(g72,g40)
    c: Coincident(g73,g40)
    c: Coincident(g73,g33)
    c: Coincident(g74,g33)
    c: Coincident(g74,g32)
    c: Coincident(g75,g32)
    c: Coincident(g75,g37)
    c: Coincident(g76,g37)
    c: Coincident(g76,g36)
    c: Coincident(g77,g36)
    c: Coincident(g77,g35)
    c: Coincident(g78,g35)
    c: Coincident(g78,g35)
    c: Coincident(g79,g35)
    c: Coincident(g79,g31)
    c: Coincident(g80,g31)
    c: Coincident(g80,g31)
    c: Coincident(g81,g31)
    c: Coincident(g81,g39)
    c: Coincident(g82,g39)
    c: Coincident(g82,g39)
    c: Coincident(g83,g39)
    c: Coincident(g83,g41)
FEATURE [PartDesign::Pocket] Pocket024  label="PocketCenterPanelBottomMidJoints"
  BaseFeature = -> Pocket023
  Direction = (0,0,-1)
  Length = 5
  Length2 = 5
  Profile = -> Sketch034
  ReferenceAxis = -> Sketch034 [N_Axis]
  Refine = true
  SideType = 0
  Suppressed = false
  Type = 1
  Type2 = 0
FEATURE [Sketcher::SketchObject] Sketch035  label="SketchCenterPanelBottomCutouts"
  ArcFitTolerance = 1e-06
  AttachmentSupport = -> [Pocket024]
  ExternalGeometry = -> [Pocket024]
  ExternalTypes = [0]
  FullyConstrained = true
  MakeInternals = false
  MapMode = 5
  sketch-geometry (20):
    g0: LineSegment StartX=-20 StartY=60.8 StartZ=0 EndX=20 EndY=60.8 EndZ=0
    g1: LineSegment StartX=20 StartY=60.8 StartZ=0 EndX=20 EndY=89 EndZ=0
    g2: LineSegment StartX=20 StartY=89 StartZ=0 EndX=-20 EndY=89 EndZ=0
    g3: LineSegment StartX=-20 StartY=89 StartZ=0 EndX=-20 EndY=60.8 EndZ=0
    g4: GeomPoint [constr] X=0 Y=74.9 Z=0
    g5: LineSegment StartX=-20 StartY=11 StartZ=0 EndX=20 EndY=11 EndZ=0
    g6: LineSegment StartX=20 StartY=11 StartZ=0 EndX=20 EndY=39.2 EndZ=0
    g7: LineSegment StartX=20 StartY=39.2 StartZ=0 EndX=-20 EndY=39.2 EndZ=0
    g8: LineSegment StartX=-20 StartY=39.2 StartZ=0 EndX=-20 EndY=11 EndZ=0
    g9: GeomPoint [constr] X=0 Y=25.1 Z=0
    g10: LineSegment StartX=-20 StartY=-39 StartZ=0 EndX=20 EndY=-39 EndZ=0
    g11: LineSegment StartX=20 StartY=-39 StartZ=0 EndX=20 EndY=-10.8 EndZ=0
    g12: LineSegment StartX=20 StartY=-10.8 StartZ=0 EndX=-20 EndY=-10.8 EndZ=0
    g13: LineSegment StartX=-20 StartY=-10.8 StartZ=0 EndX=-20 EndY=-39 EndZ=0
    g14: GeomPoint [constr] X=0 Y=-24.9 Z=0
    g15: LineSegment StartX=-20 StartY=-89 StartZ=0 EndX=20 EndY=-89 EndZ=0
    g16: LineSegment StartX=20 StartY=-89 StartZ=0 EndX=20 EndY=-60.8 EndZ=0
    g17: LineSegment StartX=20 StartY=-60.8 StartZ=0 EndX=-20 EndY=-60.8 EndZ=0
    g18: LineSegment StartX=-20 StartY=-60.8 StartZ=0 EndX=-20 EndY=-89 EndZ=0
    g19: GeomPoint [constr] X=0 Y=-74.9 Z=0
  constraints (52):
    c: Coincident(g0,g1)
    c: Coincident(g1,g2)
    c: Coincident(g2,g3)
    c: Coincident(g3,g0)
    c: Horizontal(g0)
    c: Horizontal(g2)
    c: Vertical(g1)
    c: Vertical(g3)
    c: Symmetric(g2,g0,g4)
    c: PointOnObject(g4,g-2)
    c: Distance(g-10,g2) = 5
    c: Distance(g-20,g1) = 5
    c: Distance(g-58,g0) = 5
    c: Coincident(g5,g6)
    c: Coincident(g6,g7)
    c: Coincident(g7,g8)
    c: Coincident(g8,g5)
    c: Horizontal(g5)
    c: Horizontal(g7)
    c: Vertical(g6)
    c: Vertical(g8)
    c: Symmetric(g7,g5,g9)
    c: PointOnObject(g9,g-2)
    c: Equal(g7,g0)
    c: Equal(g1,g6)
    c: Distance(g-52,g7) = 5
    c: Coincident(g10,g11)
    c: Coincident(g11,g12)
    c: Coincident(g12,g13)
    c: Coincident(g13,g10)
    c: Horizontal(g10)
    c: Horizontal(g12)
    c: Vertical(g11)
    c: Vertical(g13)
    c: Symmetric(g12,g10,g14)
    c: PointOnObject(g14,g-2)
    c: Equal(g12,g5)
    c: Equal(g6,g11)
    c: Distance(g-40,g12) = 5
    c: Coincident(g15,g16)
    c: Coincident(g16,g17)
    c: Coincident(g17,g18)
    c: Coincident(g18,g15)
    c: Horizontal(g15)
    c: Horizontal(g17)
    c: Vertical(g16)
    c: Vertical(g18)
    c: Symmetric(g17,g15,g19)
    c: PointOnObject(g19,g-2)
    c: Equal(g10,g17)
    c: Equal(g16,g11)
    c: Distance(g-29,g17) = 5
FEATURE [PartDesign::Pocket] Pocket025  label="PocketCenterPanelBottomCutouts"
  BaseFeature = -> Pocket024
  Direction = (0,0,-1)
  Length = 5
  Length2 = 5
  Profile = -> Sketch035
  ReferenceAxis = -> Sketch035 [N_Axis]
  Refine = true
  SideType = 0
  Suppressed = false
  Type = 1
  Type2 = 0
FEATURE [PartDesign::Hole] Hole010
  BaseFeature = -> Pocket025
  BaseProfileType = 7
  CustomThreadClearance = 0
  Depth = 25
  DepthType = 0
  Diameter = 3.7
  DrillForDepth = false
  DrillPoint = 1
  DrillPointAngle = 118
  HoleCutCountersinkAngle = 90
  HoleCutCustomValues = false
  HoleCutDepth = 0
  HoleCutDiameter = 0
  HoleCutType = 0
  ModelThread = false
  Profile = -> Sketch032 [Vertex6,Vertex5,Vertex7,Vertex8]
  Refine = true
  Suppressed = false
  Tapered = false
  TaperedAngle = 90
  ThreadClass = 0
  ThreadDepth = 25
  ThreadDepthType = 0
  ThreadDiameter = 4.5
  ThreadDirection = 0
  ThreadFit = 0
  ThreadSize = 12
  ThreadType = 1
  Threaded = true
  UseCustomThreadClearance = false
FEATURE [App::Link] CenterPanelBottom  label="CenterPanelBottom001"
  LinkPlacement = pos=(61.3132,-48.2812,-0.116922) rot=(0.688247,-0.688247,-0.229416;0rad)
  LinkedObject = -> Body007
  Placement = pos=(61.3132,-48.2812,-0.116922) rot=(0.688247,-0.688247,-0.229416;0rad)
FEATURE [App::Link] CenterPanelTop  label="CenterPanelTop001"
  LinkPlacement = pos=(61.3132,-48.2812,2.88308) rot=(0.688247,-0.688247,-0.229416;0rad)
  LinkedObject = -> Body008
  Placement = pos=(61.3132,-48.2812,2.88308) rot=(0.688247,-0.688247,-0.229416;0rad)
FEATURE [App::Point] Origin021  label="Origin028"
  Role = Origin
FEATURE [PartDesign::SubShapeBinder] Binder015  label="BinderPowerPanelBottom"
  BindCopyOnChange = 0
  BindMode = 0
  ClaimChildren = false
  Context = -> Body009 [Binder015.]
  Fuse = false
  MakeFace = true
  OffsetFill = false
  OffsetIntersection = false
  OffsetJoinType = 0
  OffsetOpenResult = false
  PartialLoad = false
  Refine = true
  Relative = true
  Support = -> [Sketch]
  _Version = 2
FEATURE [Sketcher::SketchObject] Sketch036  label="SketchPowerPanelBottom"
  ArcFitTolerance = 1e-06
  AttachmentSupport = -> [Origin020]
  ExternalGeometry = -> [Binder015]
  ExternalTypes = [0,0,0,0,0,0,0,0]
  FullyConstrained = true
  MakeInternals = false
  MapMode = 5
  sketch-geometry (15):
    g0: LineSegment StartX=25 StartY=50 StartZ=0 EndX=25 EndY=0 EndZ=0
    g1: LineSegment StartX=25 StartY=0 StartZ=0 EndX=125 EndY=0 EndZ=0
    g2: LineSegment StartX=125 StartY=0 StartZ=0 EndX=125 EndY=50 EndZ=0
    g3: LineSegment StartX=125 StartY=50 StartZ=0 EndX=25 EndY=50 EndZ=0
    g4: Circle CenterX=30 CenterY=45 CenterZ=0 NormalX=0 NormalY=0 NormalZ=1 AngleXU=0 Radius=2
    g5: Circle CenterX=120 CenterY=45 CenterZ=0 NormalX=0 NormalY=0 NormalZ=1 AngleXU=0 Radius=2
    g6: Circle CenterX=120 CenterY=5 CenterZ=0 NormalX=0 NormalY=0 NormalZ=1 AngleXU=0 Radius=2
    g7: Circle CenterX=30 CenterY=5 CenterZ=0 NormalX=0 NormalY=0 NormalZ=1 AngleXU=0 Radius=2
    g8: GeomPoint [constr] X=75 Y=25 Z=0
    g9: LineSegment StartX=33 StartY=8 StartZ=0 EndX=117 EndY=8 EndZ=0
    g10: LineSegment StartX=117 StartY=8 StartZ=0 EndX=117 EndY=42 EndZ=0
    g11: LineSegment StartX=117 StartY=42 StartZ=0 EndX=33 EndY=42 EndZ=0
    g12: LineSegment StartX=33 StartY=42 StartZ=0 EndX=33 EndY=8 EndZ=0
    g13: GeomPoint [constr] X=75 Y=25 Z=0
    g14: Circle CenterX=52.5 CenterY=25 CenterZ=0 NormalX=0 NormalY=0 NormalZ=1 AngleXU=0 Radius=19
  constraints (33):
    c: Coincident(g0,g1)
    c: Coincident(g1,g2)
    c: Coincident(g2,g3)
    c: Coincident(g3,g0)
    c: Vertical(g0)
    c: Vertical(g2)
    c: Horizontal(g1)
    c: Horizontal(g3)
    c: Coincident(g0,g-3)
    c: Coincident(g1,g-5)
    c: Diameter(g4) = 4
    c: Coincident(g4,g-7)
    c: Diameter(g5) = 4
    c: Coincident(g5,g-8)
    c: Diameter(g6) = 4
    c: Coincident(g6,g-9)
    c: Diameter(g7) = 4
    c: Coincident(g7,g-9)
    c: Symmetric(g7,g5,g8)
    c: Coincident(g9,g10)
    c: Coincident(g10,g11)
    c: Coincident(g11,g12)
    c: Coincident(g12,g9)
    c: Horizontal(g9)
    c: Horizontal(g11)
    c: Vertical(g10)
    c: Vertical(g12)
    c: Symmetric(g11,g9,g13)
    c: Coincident(g13,g8)
    c: Distance(g3,g11) = 8
    c: Distance(g0,g12) = 8
    c: Diameter(g14) = 38
    c: Coincident(g14,g-10)
FEATURE [PartDesign::Pad] Pad015
  Direction = (0,0,1)
  Length = 20
  Length2 = 10
  Profile = -> Sketch036 [Edge4,Edge1,Edge2,Edge3,Edge6,Edge7,Edge5,Edge8,Edge9,Edge10,Edge11,Edge12]
  ReferenceAxis = -> Sketch036 [N_Axis]
  Refine = true
  SideType = 0
  Suppressed = false
  Type = 0
  Type2 = 0
FEATURE [PartDesign::Hole] Hole014
  BaseFeature = -> Pad015
  BaseProfileType = 7
  CustomThreadClearance = 0
  Depth = 25
  DepthType = 0
  Diameter = 3.7
  DrillForDepth = false
  DrillPoint = 1
  DrillPointAngle = 118
  HoleCutCountersinkAngle = 90
  HoleCutCustomValues = false
  HoleCutDepth = 0
  HoleCutDiameter = 0
  HoleCutType = 0
  ModelThread = false
  Profile = -> Pad015 [Edge33,Edge27,Edge30,Edge36]
  Refine = true
  Suppressed = false
  Tapered = false
  TaperedAngle = 90
  ThreadClass = 0
  ThreadDepth = 25
  ThreadDepthType = 0
  ThreadDiameter = 4.5
  ThreadDirection = 0
  ThreadFit = 0
  ThreadSize = 12
  ThreadType = 1
  Threaded = true
  UseCustomThreadClearance = false
FEATURE [PartDesign::Pocket] Pocket030
  BaseFeature = -> Hole014
  Direction = (0,0,-1)
  Length = 5
  Length2 = 5
  Profile = -> Sketch036 [Edge13]
  ReferenceAxis = -> Sketch036 [N_Axis]
  Refine = true
  Reversed = true
  SideType = 0
  Suppressed = false
  Type = 1
  Type2 = 0
FEATURE [Sketcher::SketchObject] Sketch042
  ArcFitTolerance = 1e-06
  AttachmentSupport = -> [Origin020]
  ExternalGeometry = -> [Binder015]
  ExternalTypes = [0,0,0,0]
  FullyConstrained = true
  MakeInternals = false
  MapMode = 5
  sketch-geometry (36):
    g0: GeomPoint [constr] X=75 Y=50 Z=0
    g1: GeomPoint [constr] X=75 Y=7.1e-15 Z=0
    g2: LineSegment [constr] StartX=73.5 StartY=50 StartZ=0 EndX=73.5 EndY=47 EndZ=0
    g3: LineSegment [constr] StartX=73.5 StartY=47 StartZ=0 EndX=76.5 EndY=47 EndZ=0
    g4: LineSegment [constr] StartX=76.5 StartY=47 StartZ=0 EndX=76.5 EndY=50 EndZ=0
    g5: LineSegment [constr] StartX=76.5 StartY=50 StartZ=0 EndX=73.5 EndY=50 EndZ=0
    g6: LineSegment [constr] StartX=70.5 StartY=47 StartZ=0 EndX=70.5 EndY=44 EndZ=0
    g7: LineSegment [constr] StartX=70.5 StartY=44 StartZ=0 EndX=79.5 EndY=44 EndZ=0
    g8: LineSegment [constr] StartX=79.5 StartY=44 StartZ=0 EndX=79.5 EndY=47 EndZ=0
    g9: LineSegment [constr] StartX=79.5 StartY=47 StartZ=0 EndX=70.5 EndY=47 EndZ=0
    g10: LineSegment [constr] StartX=73.5 StartY=3 StartZ=0 EndX=73.5 EndY=0 EndZ=0
    g11: LineSegment [constr] StartX=73.5 StartY=0 StartZ=0 EndX=76.5 EndY=0 EndZ=0
    g12: LineSegment [constr] StartX=76.5 StartY=0 StartZ=0 EndX=76.5 EndY=3 EndZ=0
    g13: LineSegment [constr] StartX=76.5 StartY=3 StartZ=0 EndX=73.5 EndY=3 EndZ=0
    g14: LineSegment [constr] StartX=70.5 StartY=6 StartZ=0 EndX=70.5 EndY=3 EndZ=0
    g15: LineSegment [constr] StartX=70.5 StartY=3 StartZ=0 EndX=79.5 EndY=3 EndZ=0
    g16: LineSegment [constr] StartX=79.5 StartY=3 StartZ=0 EndX=79.5 EndY=6 EndZ=0
    g17: LineSegment [constr] StartX=79.5 StartY=6 StartZ=0 EndX=70.5 EndY=6 EndZ=0
    g18: GeomPoint [constr] X=75 Y=47 Z=0
    g19: GeomPoint [constr] X=75 Y=3 Z=0
    g20: LineSegment StartX=73.5 StartY=50 StartZ=0 EndX=76.5 EndY=50 EndZ=0
    g21: LineSegment StartX=76.5 StartY=50 StartZ=0 EndX=76.5 EndY=47 EndZ=0
    g22: LineSegment StartX=76.5 StartY=47 StartZ=0 EndX=79.5 EndY=47 EndZ=0
    g23: LineSegment StartX=79.5 StartY=47 StartZ=0 EndX=79.5 EndY=44 EndZ=0
    g24: LineSegment StartX=79.5 StartY=44 StartZ=0 EndX=70.5 EndY=44 EndZ=0
    g25: LineSegment StartX=70.5 StartY=44 StartZ=0 EndX=70.5 EndY=47 EndZ=0
    g26: LineSegment StartX=70.5 StartY=47 StartZ=0 EndX=73.5 EndY=47 EndZ=0
    g27: LineSegment StartX=73.5 StartY=47 StartZ=0 EndX=73.5 EndY=50 EndZ=0
    g28: LineSegment StartX=70.5 StartY=6 StartZ=0 EndX=79.5 EndY=6 EndZ=0
    g29: LineSegment StartX=79.5 StartY=6 StartZ=0 EndX=79.5 EndY=3 EndZ=0
    g30: LineSegment StartX=79.5 StartY=3 StartZ=0 EndX=76.5 EndY=3 EndZ=0
    g31: LineSegment StartX=76.5 StartY=3 StartZ=0 EndX=76.5 EndY=0 EndZ=0
    g32: LineSegment StartX=73.5 StartY=0 StartZ=0 EndX=76.5 EndY=0 EndZ=0
    g33: LineSegment StartX=73.5 StartY=0 StartZ=0 EndX=73.5 EndY=3 EndZ=0
    g34: LineSegment StartX=73.5 StartY=3 StartZ=0 EndX=70.5 EndY=3 EndZ=0
    g35: LineSegment StartX=70.5 StartY=3 StartZ=0 EndX=70.5 EndY=6 EndZ=0
  constraints (80):
    c: Symmetric(g-5,g-6,g1)
    c: Symmetric(g-3,g-6,g0)
    c: Coincident(g2,g3)
    c: Coincident(g3,g4)
    c: Coincident(g4,g5)
    c: Coincident(g5,g2)
    c: Vertical(g2)
    c: Vertical(g4)
    c: Horizontal(g3)
    c: Horizontal(g5)
    c: Distance(g2,g4) = 3
    c: Distance(g3,g5) = 3
    c: Coincident(g6,g7)
    c: Coincident(g7,g8)
    c: Coincident(g8,g9)
    c: Coincident(g9,g6)
    c: Vertical(g6)
    c: Vertical(g8)
    c: Horizontal(g7)
    c: Horizontal(g9)
    c: Distance(g6,g8) = 9
    c: Distance(g7,g9) = 3
    c: Coincident(g10,g11)
    c: Coincident(g11,g12)
    c: Coincident(g12,g13)
    c: Coincident(g13,g10)
    c: Vertical(g10)
    c: Vertical(g12)
    c: Horizontal(g11)
    c: Horizontal(g13)
    c: Distance(g10,g12) = 3
    c: Distance(g11,g13) = 3
    c: Coincident(g14,g15)
    c: Coincident(g15,g16)
    c: Coincident(g16,g17)
    c: Coincident(g17,g14)
    c: Vertical(g14)
    c: Vertical(g16)
    c: Horizontal(g15)
    c: Horizontal(g17)
    c: Distance(g14,g16) = 9
    c: Distance(g15,g17) = 3
    c: Symmetric(g6,g8,g18)
    c: Symmetric(g2,g3,g18)
    c: Symmetric(g14,g15,g19)
    c: Symmetric(g10,g12,g19)
    c: Symmetric(g2,g4,g0)
    c: Symmetric(g10,g11,g1)
    c: Coincident(g20,g2)
    c: Coincident(g20,g4)
    c: Coincident(g21,g4)
    c: Coincident(g21,g3)
    c: Coincident(g22,g3)
    c: Coincident(g22,g8)
    c: Coincident(g23,g8)
    c: Coincident(g23,g7)
    c: Coincident(g24,g7)
    c: Coincident(g24,g6)
    c: Coincident(g25,g6)
    c: Coincident(g25,g6)
    c: Coincident(g26,g6)
    c: Coincident(g26,g2)
    c: Coincident(g27,g2)
    c: Coincident(g27,g2)
    c: Coincident(g28,g14)
    c: Coincident(g28,g16)
    c: Coincident(g29,g16)
    c: Coincident(g29,g15)
    c: Coincident(g30,g15)
    c: Coincident(g30,g12)
    c: Coincident(g31,g12)
    c: Coincident(g31,g11)
    c: Coincident(g32,g10)
    c: Coincident(g32,g11)
    c: Coincident(g33,g10)
    c: Coincident(g33,g10)
    c: Coincident(g34,g10)
    c: Coincident(g34,g14)
    c: Coincident(g35,g14)
    c: Coincident(g35,g14)
FEATURE [PartDesign::Pocket] Pocket031
  BaseFeature = -> Pocket030
  Direction = (0,0,-1)
  Length = 5
  Length2 = 5
  Profile = -> Sketch042
  ReferenceAxis = -> Sketch042 [N_Axis]
  Refine = true
  Reversed = true
  SideType = 0
  Suppressed = false
  Type = 1
  Type2 = 0
FEATURE [PartDesign::Fillet] Fillet023
  Base = -> Pocket031 [Edge1,Edge2,Edge3,Edge4,Edge5,Edge6,Edge7,Edge8,Edge9,Edge10,Edge11,Edge12,Edge13,Edge14,Edge15,Edge16,Edge17,Edge18,Edge19,Edge20,Edge21,Edge22,Edge23,Edge24,Edge25,Edge26,Edge27,Edge28,Edge29,Edge30,Edge31,Edge32,Edge33,Edge34,Edge35,Edge36,Edge37,Edge38,Edge39,Edge40,+56 more]
  BaseFeature = -> Pocket031
  Radius = 0.99
  Refine = true
  SupportTransform = false
  Suppressed = false
  UseAllEdges = true
FEATURE [PartDesign::Body] Body009  label="PowerPanelBottom"
  AllowCompound = true
  Group = -> [Binder015,Sketch036,Pad015,Hole014,Pocket030,Sketch042,Pocket031,Fillet023]
  Origin = -> Origin020
  Tip = -> Fillet023
FEATURE [App::Point] Origin025  label="Origin033"
  Role = Origin
FEATURE [PartDesign::SubShapeBinder] Binder016
  BindCopyOnChange = 0
  BindMode = 0
  ClaimChildren = false
  Context = -> Body011 [Binder016.]
  Fuse = false
  MakeFace = true
  OffsetFill = false
  OffsetIntersection = false
  OffsetJoinType = 0
  OffsetOpenResult = false
  PartialLoad = false
  Refine = true
  Relative = true
  Support = -> [Sketch043]
  _Version = 2
FEATURE [Sketcher::SketchObject] Sketch044
  ArcFitTolerance = 1e-06
  AttachmentSupport = -> [Origin024]
  ExternalGeometry = -> [Binder016]
  ExternalTypes = [0]
  FullyConstrained = true
  MakeInternals = false
  MapMode = 5
FEATURE [PartDesign::Pad] Pad016
  Direction = (0,0,1)
  Length = 20
  Length2 = 10
  Profile = -> Sketch044
  ReferenceAxis = -> Sketch044 [N_Axis]
  Refine = true
  SideType = 0
  Suppressed = false
  Type = 0
  Type2 = 0
FEATURE [Sketcher::SketchObject] Sketch045
  ArcFitTolerance = 1e-06
  AttachmentSupport = -> [Origin024]
  ExternalGeometry = -> [Binder016]
  ExternalTypes = [0]
  FullyConstrained = false
  MakeInternals = false
  MapMode = 5
  sketch-geometry (161):
    g0: LineSegment [constr] StartX=28 StartY=218 StartZ=0 EndX=28 EndY=18 EndZ=0
    g1: LineSegment [constr] StartX=28 StartY=18 StartZ=0 EndX=78 EndY=18 EndZ=0
    g2: LineSegment [constr] StartX=78 StartY=18 StartZ=0 EndX=78 EndY=218 EndZ=0
    g3: LineSegment [constr] StartX=78 StartY=218 StartZ=0 EndX=28 EndY=218 EndZ=0
    g4: GeomPoint [constr] X=14 Y=118 Z=0
    g5: GeomPoint [constr] X=53 Y=118 Z=0
    g6: LineSegment [constr] StartX=14 StartY=118 StartZ=0 EndX=153.665 EndY=118 EndZ=0
    g7: LineSegment [constr] StartX=28 StartY=218 StartZ=0 EndX=0.026334 EndY=218 EndZ=0
    g8: GeomPoint [constr] X=13 Y=218 Z=0
    g9: LineSegment [constr] StartX=8.5 StartY=123.8 StartZ=0 EndX=8.5 EndY=120.8 EndZ=0
    g10: LineSegment [constr] StartX=8.5 StartY=120.8 StartZ=0 EndX=17.5 EndY=120.8 EndZ=0
    g11: LineSegment [constr] StartX=17.5 StartY=120.8 StartZ=0 EndX=17.5 EndY=123.8 EndZ=0
    g12: LineSegment [constr] StartX=17.5 StartY=123.8 StartZ=0 EndX=8.5 EndY=123.8 EndZ=0
    g13: LineSegment [constr] StartX=14.5 StartY=120.8 StartZ=0 EndX=14.5 EndY=115.2 EndZ=0
    g14: LineSegment [constr] StartX=14.5 StartY=115.2 StartZ=0 EndX=11.5 EndY=115.2 EndZ=0
    g15: LineSegment [constr] StartX=11.5 StartY=115.2 StartZ=0 EndX=11.5 EndY=120.8 EndZ=0
    g16: LineSegment [constr] StartX=11.5 StartY=120.8 StartZ=0 EndX=14.5 EndY=120.8 EndZ=0
    g17: LineSegment [constr] StartX=8.5 StartY=115.2 StartZ=0 EndX=8.5 EndY=112.2 EndZ=0
    g18: LineSegment [constr] StartX=8.5 StartY=112.2 StartZ=0 EndX=17.5 EndY=112.2 EndZ=0
    g19: LineSegment [constr] StartX=17.5 StartY=112.2 StartZ=0 EndX=17.5 EndY=115.2 EndZ=0
    g20: LineSegment [constr] StartX=17.5 StartY=115.2 StartZ=0 EndX=8.5 EndY=115.2 EndZ=0
    g21: GeomPoint [constr] X=13 Y=120.8 Z=0
    g22: GeomPoint [constr] X=13 Y=115.2 Z=0
    g23: GeomPoint [constr] X=13 Y=118 Z=0
    g24: LineSegment [constr] StartX=8.5 StartY=223.8 StartZ=0 EndX=8.5 EndY=220.8 EndZ=0
    g25: LineSegment [constr] StartX=8.5 StartY=220.8 StartZ=0 EndX=17.5 EndY=220.8 EndZ=0
    g26: LineSegment [constr] StartX=17.5 StartY=220.8 StartZ=0 EndX=17.5 EndY=223.8 EndZ=0
    g27: LineSegment [constr] StartX=17.5 StartY=223.8 StartZ=0 EndX=8.5 EndY=223.8 EndZ=0
    g28: LineSegment [constr] StartX=14.5 StartY=220.8 StartZ=0 EndX=14.5 EndY=215.2 EndZ=0
    g29: LineSegment [constr] StartX=14.5 StartY=215.2 StartZ=0 EndX=11.5 EndY=215.2 EndZ=0
    g30: LineSegment [constr] StartX=11.5 StartY=215.2 StartZ=0 EndX=11.5 EndY=220.8 EndZ=0
    g31: LineSegment [constr] StartX=11.5 StartY=220.8 StartZ=0 EndX=14.5 EndY=220.8 EndZ=0
    g32: LineSegment [constr] StartX=8.5 StartY=215.2 StartZ=0 EndX=8.5 EndY=212.2 EndZ=0
    g33: LineSegment [constr] StartX=8.5 StartY=212.2 StartZ=0 EndX=17.5 EndY=212.2 EndZ=0
    g34: LineSegment [constr] StartX=17.5 StartY=212.2 StartZ=0 EndX=17.5 EndY=215.2 EndZ=0
    g35: LineSegment [constr] StartX=17.5 StartY=215.2 StartZ=0 EndX=8.5 EndY=215.2 EndZ=0
    g36: GeomPoint [constr] X=13 Y=220.8 Z=0
    g37: GeomPoint [constr] X=13 Y=215.2 Z=0
    g38: GeomPoint [constr] X=13 Y=218 Z=0
    g39: LineSegment [constr] StartX=28 StartY=18 StartZ=0 EndX=0.026334 EndY=18 EndZ=0
    g40: LineSegment [constr] StartX=13 StartY=218 StartZ=0 EndX=13 EndY=18 EndZ=0
    g41: LineSegment [constr] StartX=191.908 StartY=138.585 StartZ=0 EndX=191.908 EndY=135.585 EndZ=0
    g42: LineSegment [constr] StartX=191.908 StartY=135.585 StartZ=0 EndX=200.908 EndY=135.585 EndZ=0
    g43: LineSegment [constr] StartX=200.908 StartY=135.585 StartZ=0 EndX=200.908 EndY=138.585 EndZ=0
    g44: LineSegment [constr] StartX=200.908 StartY=138.585 StartZ=0 EndX=191.908 EndY=138.585 EndZ=0
    g45: LineSegment [constr] StartX=194.908 StartY=135.584 StartZ=0 EndX=194.908 EndY=129.984 EndZ=0
    g46: LineSegment [constr] StartX=194.908 StartY=129.984 StartZ=0 EndX=197.908 EndY=129.984 EndZ=0
    g47: LineSegment [constr] StartX=197.908 StartY=129.984 StartZ=0 EndX=197.908 EndY=135.584 EndZ=0
    g48: LineSegment [constr] StartX=197.908 StartY=135.584 StartZ=0 EndX=194.908 EndY=135.584 EndZ=0
    g49: LineSegment [constr] StartX=191.908 StartY=129.984 StartZ=0 EndX=191.908 EndY=126.984 EndZ=0
    g50: LineSegment [constr] StartX=191.908 StartY=126.984 StartZ=0 EndX=200.908 EndY=126.984 EndZ=0
    g51: LineSegment [constr] StartX=200.908 StartY=126.984 StartZ=0 EndX=200.908 EndY=129.984 EndZ=0
    g52: LineSegment [constr] StartX=200.908 StartY=129.984 StartZ=0 EndX=191.908 EndY=129.984 EndZ=0
    g53: GeomPoint [constr] X=196.408 Y=135.585 Z=0
    g54: GeomPoint [constr] X=196.408 Y=129.984 Z=0
    g55: GeomPoint [constr] X=196.408 Y=132.784 Z=0
    g56: LineSegment [constr] StartX=8.5 StartY=173.8 StartZ=0 EndX=8.5 EndY=170.8 EndZ=0
    g57: LineSegment [constr] StartX=8.5 StartY=170.8 StartZ=0 EndX=17.5 EndY=170.8 EndZ=0
    g58: LineSegment [constr] StartX=17.5 StartY=170.8 StartZ=0 EndX=17.5 EndY=173.8 EndZ=0
    g59: LineSegment [constr] StartX=17.5 StartY=173.8 StartZ=0 EndX=8.5 EndY=173.8 EndZ=0
    g60: LineSegment [constr] StartX=14.5 StartY=170.8 StartZ=0 EndX=14.5 EndY=165.2 EndZ=0
    g61: LineSegment [constr] StartX=14.5 StartY=165.2 StartZ=0 EndX=11.5 EndY=165.2 EndZ=0
    g62: LineSegment [constr] StartX=11.5 StartY=165.2 StartZ=0 EndX=11.5 EndY=170.8 EndZ=0
    g63: LineSegment [constr] StartX=11.5 StartY=170.8 StartZ=0 EndX=14.5 EndY=170.8 EndZ=0
    g64: LineSegment [constr] StartX=8.5 StartY=165.2 StartZ=0 EndX=8.5 EndY=162.2 EndZ=0
    g65: LineSegment [constr] StartX=8.5 StartY=162.2 StartZ=0 EndX=17.5 EndY=162.2 EndZ=0
    g66: LineSegment [constr] StartX=17.5 StartY=162.2 StartZ=0 EndX=17.5 EndY=165.2 EndZ=0
    g67: LineSegment [constr] StartX=17.5 StartY=165.2 StartZ=0 EndX=8.5 EndY=165.2 EndZ=0
    g68: GeomPoint [constr] X=13 Y=170.8 Z=0
    g69: GeomPoint [constr] X=13 Y=165.2 Z=0
    g70: GeomPoint [constr] X=13 Y=168 Z=0
    g71: LineSegment [constr] StartX=8.5 StartY=73.8 StartZ=0 EndX=8.5 EndY=70.8 EndZ=0
    g72: LineSegment [constr] StartX=8.5 StartY=70.8 StartZ=0 EndX=17.5 EndY=70.8 EndZ=0
    g73: LineSegment [constr] StartX=17.5 StartY=70.8 StartZ=0 EndX=17.5 EndY=73.8 EndZ=0
    g74: LineSegment [constr] StartX=17.5 StartY=73.8 StartZ=0 EndX=8.5 EndY=73.8 EndZ=0
    g75: LineSegment [constr] StartX=11.5 StartY=70.8 StartZ=0 EndX=11.5 EndY=65.2 EndZ=0
    g76: LineSegment [constr] StartX=11.5 StartY=65.2 StartZ=0 EndX=14.5 EndY=65.2 EndZ=0
    g77: LineSegment [constr] StartX=14.5 StartY=65.2 StartZ=0 EndX=14.5 EndY=70.8 EndZ=0
    g78: LineSegment [constr] StartX=14.5 StartY=70.8 StartZ=0 EndX=11.5 EndY=70.8 EndZ=0
    g79: LineSegment [constr] StartX=8.5 StartY=65.2 StartZ=0 EndX=8.5 EndY=62.2 EndZ=0
    g80: LineSegment [constr] StartX=8.5 StartY=62.2 StartZ=0 EndX=17.5 EndY=62.2 EndZ=0
    g81: LineSegment [constr] StartX=17.5 StartY=62.2 StartZ=0 EndX=17.5 EndY=65.2 EndZ=0
    g82: LineSegment [constr] StartX=17.5 StartY=65.2 StartZ=0 EndX=8.5 EndY=65.2 EndZ=0
    g83: GeomPoint [constr] X=13 Y=70.8 Z=0
    g84: GeomPoint [constr] X=13 Y=65.2 Z=0
    g85: GeomPoint [constr] X=13 Y=68 Z=0
    g86: LineSegment [constr] StartX=8.5 StartY=23.8 StartZ=0 EndX=8.5 EndY=20.8 EndZ=0
    g87: LineSegment [constr] StartX=8.5 StartY=20.8 StartZ=0 EndX=17.5 EndY=20.8 EndZ=0
    g88: LineSegment [constr] StartX=17.5 StartY=20.8 StartZ=0 EndX=17.5 EndY=23.8 EndZ=0
    g89: LineSegment [constr] StartX=17.5 StartY=23.8 StartZ=0 EndX=8.5 EndY=23.8 EndZ=0
    g90: LineSegment [constr] StartX=11.5 StartY=20.8 StartZ=0 EndX=11.5 EndY=15.2 EndZ=0
    g91: LineSegment [constr] StartX=11.5 StartY=15.2 StartZ=0 EndX=14.5 EndY=15.2 EndZ=0
    g92: LineSegment [constr] StartX=14.5 StartY=15.2 StartZ=0 EndX=14.5 EndY=20.8 EndZ=0
    g93: LineSegment [constr] StartX=14.5 StartY=20.8 StartZ=0 EndX=11.5 EndY=20.8 EndZ=0
    g94: LineSegment [constr] StartX=8.5 StartY=15.2 StartZ=0 EndX=8.5 EndY=12.2 EndZ=0
    g95: LineSegment [constr] StartX=8.5 StartY=12.2 StartZ=0 EndX=17.5 EndY=12.2 EndZ=0
    g96: LineSegment [constr] StartX=17.5 StartY=12.2 StartZ=0 EndX=17.5 EndY=15.2 EndZ=0
    g97: LineSegment [constr] StartX=17.5 StartY=15.2 StartZ=0 EndX=8.5 EndY=15.2 EndZ=0
    g98: GeomPoint [constr] X=13 Y=20.8 Z=0
    g99: GeomPoint [constr] X=13 Y=15.2 Z=0
    g100: GeomPoint [constr] X=13 Y=18 Z=0
    g101: LineSegment StartX=8.5 StartY=223.8 StartZ=0 EndX=17.5 EndY=223.8 EndZ=0
    g102: LineSegment StartX=17.5 StartY=223.8 StartZ=0 EndX=17.5 EndY=220.8 EndZ=0
    g103: LineSegment StartX=17.5 StartY=220.8 StartZ=0 EndX=14.5 EndY=220.8 EndZ=0
    g104: LineSegment StartX=14.5 StartY=220.8 StartZ=0 EndX=14.5 EndY=215.2 EndZ=0
    g105: LineSegment StartX=14.5 StartY=215.2 StartZ=0 EndX=17.5 EndY=215.2 EndZ=0
    g106: LineSegment StartX=17.5 StartY=215.2 StartZ=0 EndX=17.5 EndY=212.2 EndZ=0
    g107: LineSegment StartX=17.5 StartY=212.2 StartZ=0 EndX=8.5 EndY=212.2 EndZ=0
    g108: LineSegment StartX=8.5 StartY=212.2 StartZ=0 EndX=8.5 EndY=215.2 EndZ=0
    g109: LineSegment StartX=8.5 StartY=215.2 StartZ=0 EndX=11.5 EndY=215.2 EndZ=0
    g110: LineSegment StartX=11.5 StartY=215.2 StartZ=0 EndX=11.5 EndY=220.8 EndZ=0
    g111: LineSegment StartX=11.5 StartY=220.8 StartZ=0 EndX=8.5 EndY=220.8 EndZ=0
    g112: LineSegment StartX=8.5 StartY=223.8 StartZ=0 EndX=8.5 EndY=220.8 EndZ=0
    g113: LineSegment StartX=8.5 StartY=173.8 StartZ=0 EndX=17.5 EndY=173.8 EndZ=0
    g114: LineSegment StartX=17.5 StartY=173.8 StartZ=0 EndX=17.5 EndY=170.8 EndZ=0
    g115: LineSegment StartX=17.5 StartY=170.8 StartZ=0 EndX=14.5 EndY=170.8 EndZ=0
    g116: LineSegment StartX=14.5 StartY=170.8 StartZ=0 EndX=14.5 EndY=165.2 EndZ=0
    g117: LineSegment StartX=14.5 StartY=165.2 StartZ=0 EndX=17.5 EndY=165.2 EndZ=0
    g118: LineSegment StartX=17.5 StartY=165.2 StartZ=0 EndX=17.5 EndY=162.2 EndZ=0
    g119: LineSegment StartX=17.5 StartY=162.2 StartZ=0 EndX=8.5 EndY=162.2 EndZ=0
    g120: LineSegment StartX=8.5 StartY=162.2 StartZ=0 EndX=8.5 EndY=165.2 EndZ=0
    g121: LineSegment StartX=8.5 StartY=165.2 StartZ=0 EndX=11.5 EndY=165.2 EndZ=0
    g122: LineSegment StartX=11.5 StartY=165.2 StartZ=0 EndX=11.5 EndY=170.8 EndZ=0
    g123: LineSegment StartX=11.5 StartY=170.8 StartZ=0 EndX=8.5 EndY=170.8 EndZ=0
    g124: LineSegment StartX=8.5 StartY=170.8 StartZ=0 EndX=8.5 EndY=173.8 EndZ=0
    g125: LineSegment StartX=17.5 StartY=123.8 StartZ=0 EndX=8.5 EndY=123.8 EndZ=0
    g126: LineSegment StartX=8.5 StartY=123.8 StartZ=0 EndX=8.5 EndY=120.8 EndZ=0
    g127: LineSegment StartX=8.5 StartY=120.8 StartZ=0 EndX=11.5 EndY=120.8 EndZ=0
    g128: LineSegment StartX=11.5 StartY=120.8 StartZ=0 EndX=11.5 EndY=115.2 EndZ=0
    g129: LineSegment StartX=11.5 StartY=115.2 StartZ=0 EndX=8.5 EndY=115.2 EndZ=0
    g130: LineSegment StartX=8.5 StartY=115.2 StartZ=0 EndX=8.5 EndY=112.2 EndZ=0
    g131: LineSegment StartX=8.5 StartY=112.2 StartZ=0 EndX=17.5 EndY=112.2 EndZ=0
    g132: LineSegment StartX=17.5 StartY=112.2 StartZ=0 EndX=17.5 EndY=115.2 EndZ=0
    g133: LineSegment StartX=17.5 StartY=115.2 StartZ=0 EndX=14.5 EndY=115.2 EndZ=0
    g134: LineSegment StartX=14.5 StartY=115.2 StartZ=0 EndX=14.5 EndY=120.8 EndZ=0
    g135: LineSegment StartX=14.5 StartY=120.8 StartZ=0 EndX=17.5 EndY=120.8 EndZ=0
    g136: LineSegment StartX=17.5 StartY=120.8 StartZ=0 EndX=17.5 EndY=123.8 EndZ=0
    g137: LineSegment StartX=17.5 StartY=73.8 StartZ=0 EndX=8.5 EndY=73.8 EndZ=0
    g138: LineSegment StartX=8.5 StartY=73.8 StartZ=0 EndX=8.5 EndY=70.8 EndZ=0
    g139: LineSegment StartX=8.5 StartY=70.8 StartZ=0 EndX=11.5 EndY=70.8 EndZ=0
    g140: LineSegment StartX=11.5 StartY=70.8 StartZ=0 EndX=11.5 EndY=65.2 EndZ=0
    g141: LineSegment StartX=11.5 StartY=65.2 StartZ=0 EndX=8.5 EndY=65.2 EndZ=0
    g142: LineSegment StartX=8.5 StartY=65.2 StartZ=0 EndX=8.5 EndY=62.2 EndZ=0
    g143: LineSegment StartX=8.5 StartY=62.2 StartZ=0 EndX=17.5 EndY=62.2 EndZ=0
    g144: LineSegment StartX=17.5 StartY=62.2 StartZ=0 EndX=17.5 EndY=65.2 EndZ=0
    g145: LineSegment StartX=17.5 StartY=65.2 StartZ=0 EndX=14.5 EndY=65.2 EndZ=0
    g146: LineSegment StartX=14.5 StartY=65.2 StartZ=0 EndX=14.5 EndY=70.8 EndZ=0
    g147: LineSegment StartX=14.5 StartY=70.8 StartZ=0 EndX=17.5 EndY=70.8 EndZ=0
    g148: LineSegment StartX=17.5 StartY=70.8 StartZ=0 EndX=17.5 EndY=73.8 EndZ=0
    g149: LineSegment StartX=8.5 StartY=23.8 StartZ=0 EndX=17.5 EndY=23.8 EndZ=0
    g150: LineSegment StartX=17.5 StartY=23.8 StartZ=0 EndX=17.5 EndY=20.8 EndZ=0
    g151: LineSegment StartX=17.5 StartY=20.8 StartZ=0 EndX=14.5 EndY=20.8 EndZ=0
    g152: LineSegment StartX=14.5 StartY=20.8 StartZ=0 EndX=14.5 EndY=15.2 EndZ=0
    g153: LineSegment StartX=14.5 StartY=15.2 StartZ=0 EndX=17.5 EndY=15.2 EndZ=0
    g154: LineSegment StartX=17.5 StartY=15.2 StartZ=0 EndX=17.5 EndY=12.2 EndZ=0
    g155: LineSegment StartX=17.5 StartY=12.2 StartZ=0 EndX=8.5 EndY=12.2 EndZ=0
    g156: LineSegment StartX=8.5 StartY=12.2 StartZ=0 EndX=8.5 EndY=15.2 EndZ=0
    g157: LineSegment StartX=8.5 StartY=15.2 StartZ=0 EndX=11.5 EndY=15.2 EndZ=0
    g158: LineSegment StartX=11.5 StartY=15.2 StartZ=0 EndX=11.5 EndY=20.8 EndZ=0
    g159: LineSegment StartX=11.5 StartY=20.8 StartZ=0 EndX=8.5 EndY=20.8 EndZ=0
    g160: LineSegment StartX=8.5 StartY=20.8 StartZ=0 EndX=8.5 EndY=23.8 EndZ=0
  constraints (366):
    c: Coincident(g0,g1)
    c: Coincident(g1,g2)
    c: Coincident(g2,g3)
    c: Coincident(g3,g0)
    c: Vertical(g0)
    c: Vertical(g2)
    c: Horizontal(g1)
    c: Horizontal(g3)
    c: Distance(g0,g2) = 50
    c: Distance(g1,g3) = 200
    c: Symmetric(g-1,g-8,g4)
    c: Symmetric(g0,g2,g5)
    c: Coincident(g6,g4)
    c: Horizontal(g6)
    c: PointOnObject(g5,g6)
    c: PointOnObject(g0,g-7)
    c: Horizontal(g7)
    c: Coincident(g7,g0)
    c: PointOnObject(g7,g-3)
    c: PointOnObject(g8,g3)
    c: DistanceX(g8,g2) = 65
    c: Coincident(g9,g10)
    c: Coincident(g10,g11)
    c: Coincident(g11,g12)
    c: Coincident(g12,g9)
    c: Vertical(g9)
    c: Vertical(g11)
    c: Horizontal(g10)
    c: Horizontal(g12)
    c: Distance(g9,g11) = 9
    c: Distance(g10,g12) = 3
    c: Coincident(g13,g14)
    c: Coincident(g14,g15)
    c: Coincident(g15,g16)
    c: Coincident(g16,g13)
    c: Vertical(g13)
    c: Vertical(g15)
    c: Horizontal(g14)
    c: Horizontal(g16)
    c: Distance(g13,g15) = 3
    c: Distance(g14,g16) = 5.6
    c: Coincident(g17,g18)
    c: Coincident(g18,g19)
    c: Coincident(g19,g20)
    c: Coincident(g20,g17)
    c: Vertical(g17)
    c: Vertical(g19)
    c: Horizontal(g18)
    c: Horizontal(g20)
    c: Distance(g17,g19) = 9
    c: Distance(g18,g20) = 3
    c: Symmetric(g9,g10,g21)
    c: Symmetric(g13,g14,g22)
    c: Symmetric(g17,g19,g22)
    c: Symmetric(g13,g15,g21)
    c: Symmetric(g13,g15,g23)
    c: Coincident(g24,g25)
    c: Coincident(g25,g26)
    c: Coincident(g26,g27)
    c: Coincident(g27,g24)
    c: Vertical(g24)
    c: Vertical(g26)
    c: Horizontal(g25)
    c: Horizontal(g27)
    c: Distance(g24,g26) = 9
    c: Distance(g25,g27) = 3
    c: Coincident(g28,g29)
    c: Coincident(g29,g30)
    c: Coincident(g30,g31)
    c: Coincident(g31,g28)
    c: Vertical(g28)
    c: Vertical(g30)
    c: Horizontal(g29)
    c: Horizontal(g31)
    c: Distance(g28,g30) = 3
    c: Distance(g29,g31) = 5.6
    c: Coincident(g32,g33)
    c: Coincident(g33,g34)
    c: Coincident(g34,g35)
    c: Coincident(g35,g32)
    c: Vertical(g32)
    c: Vertical(g34)
    c: Horizontal(g33)
    c: Horizontal(g35)
    c: Distance(g32,g34) = 9
    c: Distance(g33,g35) = 3
    c: Symmetric(g24,g25,g36)
    c: Symmetric(g28,g29,g37)
    c: Symmetric(g32,g34,g37)
    c: Symmetric(g28,g30,g36)
    c: Symmetric(g28,g30,g38)
    c: Coincident(g39,g0)
    c: PointOnObject(g39,g-5)
    c: Horizontal(g39)
    c: Vertical(g40)
    c: PointOnObject(g40,g39)
    c: Coincident(g41,g42)
    c: Coincident(g42,g43)
    c: Coincident(g43,g44)
    c: Coincident(g44,g41)
    c: Vertical(g41)
    c: Vertical(g43)
    c: Horizontal(g42)
    c: Horizontal(g44)
    c: Distance(g41,g43) = 9
    c: Distance(g42,g44) = 3
    c: Coincident(g45,g46)
    c: Coincident(g46,g47)
    c: Coincident(g47,g48)
    c: Coincident(g48,g45)
    c: Vertical(g45)
    c: Vertical(g47)
    c: Horizontal(g46)
    c: Horizontal(g48)
    c: Distance(g45,g47) = 3
    c: Distance(g46,g48) = 5.6
    c: Coincident(g49,g50)
    c: Coincident(g50,g51)
    c: Coincident(g51,g52)
    c: Coincident(g52,g49)
    c: Vertical(g49)
    c: Vertical(g51)
    c: Horizontal(g50)
    c: Horizontal(g52)
    c: Distance(g49,g51) = 9
    c: Distance(g50,g52) = 3
    c: Symmetric(g41,g42,g53)
    c: Symmetric(g45,g46,g54)
    c: Symmetric(g49,g51,g54)
    c: Symmetric(g45,g47,g53)
    c: Symmetric(g45,g47,g55)
    c: Coincident(g56,g57)
    c: Coincident(g57,g58)
    c: Coincident(g58,g59)
    c: Coincident(g59,g56)
    c: Vertical(g56)
    c: Vertical(g58)
    c: Horizontal(g57)
    c: Horizontal(g59)
    c: Distance(g56,g58) = 9
    c: Distance(g57,g59) = 3
    c: Coincident(g60,g61)
    c: Coincident(g61,g62)
    c: Coincident(g62,g63)
    c: Coincident(g63,g60)
    c: Vertical(g60)
    c: Vertical(g62)
    c: Horizontal(g61)
    c: Horizontal(g63)
    c: Distance(g60,g62) = 3
    c: Distance(g61,g63) = 5.6
    c: Coincident(g64,g65)
    c: Coincident(g65,g66)
    c: Coincident(g66,g67)
    c: Coincident(g67,g64)
    c: Vertical(g64)
    c: Vertical(g66)
    c: Horizontal(g65)
    c: Horizontal(g67)
    c: Distance(g64,g66) = 9
    c: Distance(g65,g67) = 3
    c: Symmetric(g56,g57,g68)
    c: Symmetric(g60,g61,g69)
    c: Symmetric(g64,g66,g69)
    c: Symmetric(g60,g62,g68)
    c: Symmetric(g60,g62,g70)
    c: Coincident(g38,g8)
    c: Coincident(g40,g8)
    c: PointOnObject(g70,g40)
    c: PointOnObject(g23,g40)
    c: DistanceY(g70,g8) = 50
    c: DistanceY(g23,g70) = 50
    c: Coincident(g71,g72)
    c: Coincident(g72,g73)
    c: Coincident(g73,g74)
    c: Coincident(g74,g71)
    c: Vertical(g71)
    c: Vertical(g73)
    c: Horizontal(g72)
    c: Horizontal(g74)
    c: Distance(g71,g73) = 9
    c: Distance(g72,g74) = 3
    c: Coincident(g75,g76)
    c: Coincident(g76,g77)
    c: Coincident(g77,g78)
    c: Coincident(g78,g75)
    c: Vertical(g75)
    c: Vertical(g77)
    c: Horizontal(g76)
    c: Horizontal(g78)
    c: Distance(g75,g77) = 3
    c: Distance(g76,g78) = 5.6
    c: Coincident(g79,g80)
    c: Coincident(g80,g81)
    c: Coincident(g81,g82)
    c: Coincident(g82,g79)
    c: Vertical(g79)
    c: Vertical(g81)
    c: Horizontal(g80)
    c: Horizontal(g82)
    c: Distance(g79,g81) = 9
    c: Distance(g80,g82) = 3
    c: Symmetric(g71,g72,g83)
    c: Symmetric(g75,g76,g84)
    c: Symmetric(g79,g81,g84)
    c: Symmetric(g75,g77,g83)
    c: Symmetric(g75,g77,g85)
    c: Coincident(g86,g87)
    c: Coincident(g87,g88)
    c: Coincident(g88,g89)
    c: Coincident(g89,g86)
    c: Vertical(g86)
    c: Vertical(g88)
    c: Horizontal(g87)
    c: Horizontal(g89)
    c: Distance(g86,g88) = 9
    c: Distance(g87,g89) = 3
    c: Coincident(g90,g91)
    c: Coincident(g91,g92)
    c: Coincident(g92,g93)
    c: Coincident(g93,g90)
    c: Vertical(g90)
    c: Vertical(g92)
    c: Horizontal(g91)
    c: Horizontal(g93)
    c: Distance(g90,g92) = 3
    c: Distance(g91,g93) = 5.6
    c: Coincident(g94,g95)
    c: Coincident(g95,g96)
    c: Coincident(g96,g97)
    c: Coincident(g97,g94)
    c: Vertical(g94)
    c: Vertical(g96)
    c: Horizontal(g95)
    c: Horizontal(g97)
    c: Distance(g94,g96) = 9
    c: Distance(g95,g97) = 3
    c: Symmetric(g86,g87,g98)
    c: Symmetric(g90,g91,g99)
    c: Symmetric(g94,g96,g99)
    c: Symmetric(g90,g92,g98)
    c: Symmetric(g90,g92,g100)
    c: PointOnObject(g85,g40)
    c: DistanceY(g85,g23) = 50
    c: PointOnObject(g100,g40)
    c: DistanceY(g100,g85) = 50
    c: Coincident(g101,g24)
    c: Coincident(g101,g26)
    c: Coincident(g102,g26)
    c: Coincident(g102,g25)
    c: Coincident(g103,g25)
    c: Coincident(g103,g28)
    c: Coincident(g104,g28)
    c: Coincident(g104,g28)
    c: Coincident(g105,g28)
    c: Coincident(g105,g34)
    c: Coincident(g106,g34)
    c: Coincident(g106,g33)
    c: Coincident(g107,g33)
    c: Coincident(g107,g32)
    c: Coincident(g108,g32)
    c: Coincident(g108,g32)
    c: Coincident(g109,g32)
    c: Coincident(g109,g29)
    c: Coincident(g110,g29)
    c: Coincident(g110,g30)
    c: Coincident(g111,g30)
    c: Coincident(g111,g24)
    c: Coincident(g112,g24)
    c: Coincident(g112,g24)
    c: Coincident(g113,g56)
    c: Coincident(g113,g58)
    c: Coincident(g114,g58)
    c: Coincident(g114,g57)
    c: Coincident(g115,g57)
    c: Coincident(g115,g60)
    c: Coincident(g116,g60)
    c: Coincident(g116,g60)
    c: Coincident(g117,g60)
    c: Coincident(g117,g66)
    c: Coincident(g118,g66)
    c: Coincident(g118,g65)
    c: Coincident(g119,g65)
    c: Coincident(g119,g64)
    c: Coincident(g120,g64)
    c: Coincident(g120,g64)
    c: Coincident(g121,g64)
    c: Coincident(g121,g61)
    c: Coincident(g122,g61)
    c: Coincident(g122,g62)
    c: Coincident(g123,g62)
    c: Coincident(g123,g56)
    c: Coincident(g124,g56)
    c: Coincident(g124,g56)
    c: Coincident(g125,g11)
    c: Coincident(g125,g9)
    c: Coincident(g126,g9)
    c: Coincident(g126,g9)
    c: Coincident(g127,g9)
    c: Coincident(g127,g15)
    c: Coincident(g128,g15)
    c: Coincident(g128,g14)
    c: Coincident(g129,g14)
    c: Coincident(g129,g17)
    c: Coincident(g130,g17)
    c: Coincident(g130,g17)
    c: Coincident(g131,g17)
    c: Coincident(g131,g18)
    c: Coincident(g132,g18)
    c: Coincident(g132,g19)
    c: Coincident(g133,g19)
    c: Coincident(g133,g13)
    c: Coincident(g134,g13)
    c: Coincident(g134,g13)
    c: Coincident(g135,g13)
    c: Coincident(g135,g10)
    c: Coincident(g136,g10)
    c: Coincident(g136,g11)
    c: Coincident(g137,g73)
    c: Coincident(g137,g71)
    c: Coincident(g138,g71)
    c: Coincident(g138,g71)
    c: Coincident(g139,g71)
    c: Coincident(g139,g75)
    c: Coincident(g140,g75)
    c: Coincident(g140,g75)
    c: Coincident(g141,g75)
    c: Coincident(g141,g79)
    c: Coincident(g142,g79)
    c: Coincident(g142,g79)
    c: Coincident(g143,g79)
    c: Coincident(g143,g80)
    c: Coincident(g144,g80)
    c: Coincident(g144,g81)
    c: Coincident(g145,g81)
    c: Coincident(g145,g76)
    c: Coincident(g146,g76)
    c: Coincident(g146,g77)
    c: Coincident(g147,g77)
    c: Coincident(g147,g72)
    c: Coincident(g148,g72)
    c: Coincident(g148,g73)
    c: Coincident(g149,g86)
    c: Coincident(g149,g88)
    c: Coincident(g150,g88)
    c: Coincident(g150,g87)
    c: Coincident(g151,g87)
    c: Coincident(g151,g92)
    c: Coincident(g152,g92)
    c: Coincident(g152,g91)
    c: Coincident(g153,g91)
    c: Coincident(g153,g96)
    c: Coincident(g154,g96)
    c: Coincident(g154,g95)
    c: Coincident(g155,g95)
    c: Coincident(g155,g94)
    c: Coincident(g156,g94)
    c: Coincident(g156,g94)
    c: Coincident(g157,g94)
    c: Coincident(g157,g90)
    c: Coincident(g158,g90)
    c: Coincident(g158,g90)
    c: Coincident(g159,g90)
    c: Coincident(g159,g86)
    c: Coincident(g160,g86)
    c: Coincident(g160,g86)
FEATURE [PartDesign::Pocket] Pocket032
  BaseFeature = -> Pad016
  Direction = (0,0,-1)
  Length = 17
  Length2 = 5
  Profile = -> Sketch045
  ReferenceAxis = -> Sketch045 [N_Axis]
  Refine = true
  Reversed = true
  SideType = 0
  Suppressed = false
  Type = 0
  Type2 = 0
FEATURE [PartDesign::Fillet] Fillet024
  Base = -> Pocket032 [Face69,Edge18,Face13,Face14,Face12,Face15,Face16,Face17,Face11,Face20,Face9,Edge98,Face19,Face18,Face70,Face27,Face28,Face26,Face29,Edge110,Face25,Face24,Face30,Face10,Face31,Face23,Face21,Face22,Face32,Face40,Face39,Face38,Edge134,Face37,Face71,Face41,Face42,Face36,Face34,Face43,+29 more]
  BaseFeature = -> Pocket032
  Radius = 1
  Refine = true
  SupportTransform = false
  Suppressed = false
  UseAllEdges = false
FEATURE [PartDesign::Body] Body011  label="Strongway13inFrameLeft"
  AllowCompound = true
  Group = -> [Binder016,Sketch044,Pad016,Sketch045,Pocket032,Fillet024]
  Origin = -> Origin024
  Tip = -> Fillet024
FEATURE [Sketcher::SketchObject] Sketch043  label="MasterStrongway13inFrame"
  ArcFitTolerance = 1e-06
  ExternalTypes = [0]
  FullyConstrained = true
  MakeInternals = false
  MapMode = 5
  sketch-geometry (17):
    g0: LineSegment [constr] StartX=19 StartY=0 StartZ=0 EndX=296 EndY=0 EndZ=0
    g1: LineSegment StartX=315 StartY=19 StartZ=0 EndX=315 EndY=217 EndZ=0
    g2: LineSegment [constr] StartX=296 StartY=236 StartZ=0 EndX=19 EndY=236 EndZ=0
    g3: LineSegment StartX=0 StartY=217 StartZ=0 EndX=0 EndY=19 EndZ=0
    g4: ArcOfCircle CenterX=19 CenterY=19 CenterZ=0 NormalX=0 NormalY=0 NormalZ=1 AngleXU=0 Radius=19 StartAngle=3.14159 EndAngle=4.71239
    g5: ArcOfCircle CenterX=296 CenterY=19 CenterZ=0 NormalX=0 NormalY=0 NormalZ=1 AngleXU=0 Radius=19 StartAngle=4.71239 EndAngle=6.28319
    g6: ArcOfCircle CenterX=296 CenterY=217 CenterZ=0 NormalX=0 NormalY=0 NormalZ=1 AngleXU=0 Radius=19 StartAngle=1e-16 EndAngle=1.5708
    g7: ArcOfCircle CenterX=19 CenterY=217 CenterZ=0 NormalX=0 NormalY=0 NormalZ=1 AngleXU=0 Radius=19 StartAngle=1.5708 EndAngle=3.14159
    g8: GeomPoint [constr] X=0 Y=0 Z=0
    g9: GeomPoint [constr] X=315 Y=236 Z=0
    g10: LineSegment StartX=28 StartY=236 StartZ=0 EndX=28 EndY=0 EndZ=0
    g11: LineSegment StartX=287 StartY=236 StartZ=0 EndX=287 EndY=0 EndZ=0
    g12: LineSegment StartX=287 StartY=236 StartZ=0 EndX=296 EndY=236 EndZ=0
    g13: LineSegment StartX=287 StartY=0 StartZ=0 EndX=296 EndY=0 EndZ=0
    g14: LineSegment StartX=28 StartY=0 StartZ=0 EndX=19 EndY=0 EndZ=0
    g15: LineSegment StartX=19 StartY=236 StartZ=0 EndX=28 EndY=236 EndZ=0
    g16: GeomPoint [constr] X=157.5 Y=118 Z=0
  constraints (42):
    c: Tangent(g0,g4) = -1.5708
    c: Tangent(g0,g5) = -1.5708
    c: Tangent(g1,g5) = -1.5708
    c: Tangent(g1,g6) = -1.5708
    c: Tangent(g2,g6) = -1.5708
    c: Tangent(g2,g7) = -1.5708
    c: Tangent(g3,g7) = -1.5708
    c: Tangent(g3,g4) = -1.5708
    c: Horizontal(g0)
    c: Horizontal(g2)
    c: Vertical(g1)
    c: Vertical(g3)
    c: Equal(g4,g5)
    c: Equal(g5,g6)
    c: Equal(g6,g7)
    c: PointOnObject(g8,g0)
    c: PointOnObject(g8,g3)
    c: PointOnObject(g9,g1)
    c: PointOnObject(g9,g2)
    c: Radius(g5) = 19
    c: Coincident(g8,g-1)
    c: Distance(g1,g3) = 315
    c: Distance(g2,g0) = 236
    c: Vertical(g10)
    c: PointOnObject(g10,g2)
    c: PointOnObject(g10,g0)
    c: Distance(g10,g3) = 28
    c: Vertical(g11)
    c: PointOnObject(g11,g2)
    c: PointOnObject(g11,g0)
    c: Distance(g1,g11) = 28
    c: Coincident(g2,g12)
    c: Coincident(g12,g11)
    c: Coincident(g0,g13)
    c: Coincident(g11,g13)
    c: Coincident(g14,g10)
    c: Coincident(g14,g0)
    c: Coincident(g15,g2)
    c: Coincident(g15,g10)
    c: Horizontal(g15)
    c: Tangent(g15,g7)
    c: Symmetric(g8,g9,g16)
FEATURE [App::Point] Origin027  label="Origin036"
  Role = Origin
FEATURE [Sketcher::SketchObject] Sketch046
  ArcFitTolerance = 1e-06
  AttachmentSupport = -> [Origin026]
  ExternalTypes = [0]
  FullyConstrained = true
  MakeInternals = false
  MapMode = 5
  sketch-geometry (61):
    g0: LineSegment StartX=-125 StartY=-9 StartZ=0 EndX=125 EndY=-9 EndZ=0
    g1: LineSegment StartX=125 StartY=-9 StartZ=0 EndX=125 EndY=9 EndZ=0
    g2: LineSegment StartX=125 StartY=9 StartZ=0 EndX=-125 EndY=9 EndZ=0
    g3: LineSegment StartX=-125 StartY=9 StartZ=0 EndX=-125 EndY=-9 EndZ=0
    g4: LineSegment [constr] StartX=-79.5 StartY=-3 StartZ=0 EndX=-79.5 EndY=-6 EndZ=0
    g5: LineSegment [constr] StartX=-70.5 StartY=-6 StartZ=0 EndX=-70.5 EndY=-3 EndZ=0
    g6: LineSegment [constr] StartX=-70.5 StartY=-3 StartZ=0 EndX=-79.5 EndY=-3 EndZ=0
    g7: GeomPoint [constr] X=0 Y=0 Z=0
    g8: LineSegment StartX=-79.5 StartY=-3 StartZ=0 EndX=-70.5 EndY=-3 EndZ=0
    g9: LineSegment StartX=-79.5 StartY=-6 StartZ=0 EndX=-79.5 EndY=-3 EndZ=0
    g10: LineSegment [constr] StartX=-79.5 StartY=-6 StartZ=0 EndX=-70.5 EndY=-6 EndZ=0
    g11: LineSegment [constr] StartX=-76.5 StartY=-6 StartZ=0 EndX=-76.5 EndY=-9 EndZ=0
    g12: LineSegment [constr] StartX=-76.5 StartY=-9 StartZ=0 EndX=-73.5 EndY=-9 EndZ=0
    g13: LineSegment [constr] StartX=-73.5 StartY=-9 StartZ=0 EndX=-73.5 EndY=-6 EndZ=0
    g14: LineSegment [constr] StartX=-73.5 StartY=-6 StartZ=0 EndX=-76.5 EndY=-6 EndZ=0
    g15: GeomPoint [constr] X=-75 Y=-6 Z=0
    g16: LineSegment StartX=-79.5 StartY=-6 StartZ=0 EndX=-76.5 EndY=-6 EndZ=0
    g17: LineSegment StartX=-76.5 StartY=-6 StartZ=0 EndX=-76.5 EndY=-9 EndZ=0
    g18: LineSegment StartX=-76.5 StartY=-9 StartZ=0 EndX=-73.5 EndY=-9 EndZ=0
    g19: LineSegment StartX=-73.5 StartY=-9 StartZ=0 EndX=-73.5 EndY=-6 EndZ=0
    g20: LineSegment StartX=-73.5 StartY=-6 StartZ=0 EndX=-70.5 EndY=-6 EndZ=0
    g21: LineSegment StartX=-70.5 StartY=-6 StartZ=0 EndX=-70.5 EndY=-3 EndZ=0
    g22: GeomPoint [constr] X=0 Y=-9 Z=0
    g23: LineSegment [constr] StartX=-4.5 StartY=-3 StartZ=0 EndX=-4.5 EndY=-6 EndZ=0
    g24: LineSegment [constr] StartX=4.5 StartY=-6 StartZ=0 EndX=4.5 EndY=-3 EndZ=0
    g25: LineSegment [constr] StartX=4.5 StartY=-3 StartZ=0 EndX=-4.5 EndY=-3 EndZ=0
    g26: LineSegment StartX=-4.5 StartY=-3 StartZ=0 EndX=4.5 EndY=-3 EndZ=0
    g27: LineSegment StartX=-4.5 StartY=-6 StartZ=0 EndX=-4.5 EndY=-3 EndZ=0
    g28: LineSegment [constr] StartX=-4.5 StartY=-6 StartZ=0 EndX=4.5 EndY=-6 EndZ=0
    g29: LineSegment [constr] StartX=-1.5 StartY=-6 StartZ=0 EndX=-1.5 EndY=-9 EndZ=0
    g30: LineSegment [constr] StartX=-1.5 StartY=-9 StartZ=0 EndX=1.5 EndY=-9 EndZ=0
    g31: LineSegment [constr] StartX=1.5 StartY=-9 StartZ=0 EndX=1.5 EndY=-6 EndZ=0
    g32: LineSegment [constr] StartX=1.5 StartY=-6 StartZ=0 EndX=-1.5 EndY=-6 EndZ=0
    g33: GeomPoint [constr] X=2e-16 Y=-6 Z=0
    g34: LineSegment StartX=-4.5 StartY=-6 StartZ=0 EndX=-1.5 EndY=-6 EndZ=0
    g35: LineSegment StartX=-1.5 StartY=-6 StartZ=0 EndX=-1.5 EndY=-9 EndZ=0
    g36: LineSegment StartX=-1.5 StartY=-9 StartZ=0 EndX=1.5 EndY=-9 EndZ=0
    g37: LineSegment StartX=1.5 StartY=-9 StartZ=0 EndX=1.5 EndY=-6 EndZ=0
    g38: LineSegment StartX=1.5 StartY=-6 StartZ=0 EndX=4.5 EndY=-6 EndZ=0
    g39: LineSegment StartX=4.5 StartY=-6 StartZ=0 EndX=4.5 EndY=-3 EndZ=0
    g40: LineSegment [constr] StartX=70.5 StartY=-3 StartZ=0 EndX=70.5 EndY=-6 EndZ=0
    g41: LineSegment [constr] StartX=79.5 StartY=-6 StartZ=0 EndX=79.5 EndY=-3 EndZ=0
    g42: LineSegment [constr] StartX=79.5 StartY=-3 StartZ=0 EndX=70.5 EndY=-3 EndZ=0
    g43: LineSegment StartX=70.5 StartY=-3 StartZ=0 EndX=79.5 EndY=-3 EndZ=0
    g44: LineSegment StartX=70.5 StartY=-6 StartZ=0 EndX=70.5 EndY=-3 EndZ=0
    g45: LineSegment [constr] StartX=70.5 StartY=-6 StartZ=0 EndX=79.5 EndY=-6 EndZ=0
    g46: LineSegment [constr] StartX=73.5 StartY=-6 StartZ=0 EndX=73.5 EndY=-9 EndZ=0
    g47: LineSegment [constr] StartX=73.5 StartY=-9 StartZ=0 EndX=76.5 EndY=-9 EndZ=0
    g48: LineSegment [constr] StartX=76.5 StartY=-9 StartZ=0 EndX=76.5 EndY=-6 EndZ=0
    g49: LineSegment [constr] StartX=76.5 StartY=-6 StartZ=0 EndX=73.5 EndY=-6 EndZ=0
    g50: GeomPoint [constr] X=75 Y=-6 Z=0
    g51: LineSegment StartX=70.5 StartY=-6 StartZ=0 EndX=73.5 EndY=-6 EndZ=0
    g52: LineSegment StartX=73.5 StartY=-6 StartZ=0 EndX=73.5 EndY=-9 EndZ=0
    g53: LineSegment StartX=73.5 StartY=-9 StartZ=0 EndX=76.5 EndY=-9 EndZ=0
    g54: LineSegment StartX=76.5 StartY=-9 StartZ=0 EndX=76.5 EndY=-6 EndZ=0
    g55: LineSegment StartX=76.5 StartY=-6 StartZ=0 EndX=79.5 EndY=-6 EndZ=0
    g56: LineSegment StartX=79.5 StartY=-6 StartZ=0 EndX=79.5 EndY=-3 EndZ=0
    g57: GeomPoint [constr] X=75 Y=-9 Z=0
    g58: GeomPoint [constr] X=-75 Y=-9 Z=0
    g59: LineSegment StartX=-1.5 StartY=-9 StartZ=0 EndX=1.5 EndY=-9 EndZ=0
    g60: LineSegment StartX=73.5 StartY=-9 StartZ=0 EndX=76.5 EndY=-9 EndZ=0
  constraints (139):
    c: Coincident(g0,g1)
    c: Coincident(g1,g2)
    c: Coincident(g2,g3)
    c: Coincident(g3,g0)
    c: Horizontal(g0)
    c: Horizontal(g2)
    c: Vertical(g1)
    c: Vertical(g3)
    c: Symmetric(g2,g0,g-1)
    c: Distance(g1,g3) = 250
    c: Distance(g0,g2) = 18
    c: Coincident(g5,g6)
    c: Coincident(g6,g4)
    c: Vertical(g4)
    c: Vertical(g5)
    c: Horizontal(g6)
    c: Distance(g4,g5) = 9
    c: Distance(g4,g6) = 3
    c: Coincident(g7,g-1)
    c: Coincident(g8,g4)
    c: Coincident(g8,g5)
    c: Coincident(g9,g4)
    c: Coincident(g9,g4)
    c: Coincident(g10,g4)
    c: Horizontal(g10)
    c: Coincident(g5,g10)
    c: Coincident(g11,g12)
    c: Coincident(g12,g13)
    c: Coincident(g13,g14)
    c: Coincident(g14,g11)
    c: Vertical(g11)
    c: Vertical(g13)
    c: Horizontal(g12)
    c: Horizontal(g14)
    c: Distance(g11,g13) = 3
    c: Distance(g12,g14) = 3
    c: Symmetric(g4,g5,g15)
    c: Symmetric(g11,g13,g15)
    c: Coincident(g16,g4)
    c: Coincident(g16,g11)
    c: Coincident(g17,g11)
    c: Coincident(g17,g11)
    c: Coincident(g18,g11)
    c: Coincident(g18,g12)
    c: Coincident(g19,g12)
    c: Coincident(g19,g13)
    c: Coincident(g20,g13)
    c: Coincident(g20,g5)
    c: Coincident(g21,g5)
    c: Coincident(g21,g5)
    c: PointOnObject(g22,g-2)
    c: PointOnObject(g22,g0)
    c: Coincident(g24,g25)
    c: Coincident(g25,g23)
    c: Vertical(g23)
    c: Vertical(g24)
    c: Horizontal(g25)
    c: Distance(g23,g24) = 9
    c: Distance(g23,g25) = 3
    c: Coincident(g26,g23)
    c: Coincident(g26,g24)
    c: Coincident(g27,g23)
    c: Coincident(g27,g23)
    c: Coincident(g28,g23)
    c: Horizontal(g28)
    c: Coincident(g24,g28)
    c: Coincident(g29,g30)
    c: Coincident(g30,g31)
    c: Coincident(g31,g32)
    c: Coincident(g32,g29)
    c: Vertical(g29)
    c: Vertical(g31)
    c: Horizontal(g30)
    c: Horizontal(g32)
    c: Distance(g29,g31) = 3
    c: Distance(g30,g32) = 3
    c: Symmetric(g23,g24,g33)
    c: Symmetric(g29,g31,g33)
    c: Coincident(g34,g23)
    c: Coincident(g34,g29)
    c: Coincident(g35,g29)
    c: Coincident(g35,g29)
    c: Coincident(g36,g29)
    c: Coincident(g36,g30)
    c: Coincident(g37,g30)
    c: Coincident(g37,g31)
    c: Coincident(g38,g31)
    c: Coincident(g38,g24)
    c: Coincident(g39,g24)
    c: Coincident(g39,g24)
    c: Coincident(g41,g42)
    c: Coincident(g42,g40)
    c: Vertical(g40)
    c: Vertical(g41)
    c: Horizontal(g42)
    c: Distance(g40,g41) = 9
    c: Distance(g40,g42) = 3
    c: Coincident(g43,g40)
    c: Coincident(g43,g41)
    c: Coincident(g44,g40)
    c: Coincident(g44,g40)
    c: Coincident(g45,g40)
    c: Horizontal(g45)
    c: Coincident(g41,g45)
    c: Coincident(g46,g47)
    c: Coincident(g47,g48)
    c: Coincident(g48,g49)
    c: Coincident(g49,g46)
    c: Vertical(g46)
    c: Vertical(g48)
    c: Horizontal(g47)
    c: Horizontal(g49)
    c: Distance(g46,g48) = 3
    c: Distance(g47,g49) = 3
    c: Symmetric(g40,g41,g50)
    c: Symmetric(g46,g48,g50)
    c: Coincident(g51,g40)
    c: Coincident(g51,g46)
    c: Coincident(g52,g46)
    c: Coincident(g52,g46)
    c: Coincident(g53,g46)
    c: Coincident(g53,g47)
    c: Coincident(g54,g47)
    c: Coincident(g54,g48)
    c: Coincident(g55,g48)
    c: Coincident(g55,g41)
    c: Coincident(g56,g41)
    c: Coincident(g56,g41)
    c: Symmetric(g29,g30,g22)
    c: Symmetric(g46,g47,g57)
    c: Symmetric(g11,g12,g58)
    c: PointOnObject(g57,g0)
    c: PointOnObject(g58,g0)
    c: DistanceX(g58,g22) = 75
    c: DistanceX(g22,g57) = 75
    c: Coincident(g59,g29)
    c: Coincident(g59,g30)
    c: Coincident(g60,g46)
    c: Coincident(g60,g47)
FEATURE [PartDesign::Pad] Pad017
  Direction = (0,0,1)
  Length = 20
  Length2 = 10
  Profile = -> Sketch046 [Edge3,Edge4,Edge1,Edge2]
  ReferenceAxis = -> Sketch046 [N_Axis]
  Refine = true
  SideType = 0
  Suppressed = false
  Type = 0
  Type2 = 0
FEATURE [PartDesign::Pocket] Pocket033
  BaseFeature = -> Pad017
  Direction = (0,0,-1)
  Length = 17
  Length2 = 5
  Profile = -> Sketch046 [Edge10,Edge11,Edge12,Edge5,Edge6,Edge7,Edge8,Edge9]
  ReferenceAxis = -> Sketch046 [N_Axis]
  Refine = true
  Reversed = true
  SideType = 0
  Suppressed = false
  Type = 0
  Type2 = 0
FEATURE [PartDesign::Pocket] Pocket034
  BaseFeature = -> Pocket033
  Direction = (0,0,-1)
  Length = 17
  Length2 = 5
  Profile = -> Sketch046 [Edge17,Edge19,Edge20,Edge21,Edge13,Edge14,Edge15,Edge16]
  ReferenceAxis = -> Sketch046 [N_Axis]
  Refine = true
  Reversed = true
  SideType = 0
  Suppressed = false
  Type = 0
  Type2 = 0
FEATURE [PartDesign::Pocket] Pocket035
  BaseFeature = -> Pocket034
  Direction = (0,0,-1)
  Length = 17
  Length2 = 5
  Profile = -> Sketch046 [Edge26,Edge28,Edge29,Edge30,Edge22,Edge23,Edge24,Edge25]
  ReferenceAxis = -> Sketch046 [N_Axis]
  Refine = true
  Reversed = true
  SideType = 0
  Suppressed = false
  Type = 0
  Type2 = 0
FEATURE [PartDesign::Fillet] Fillet025
  Base = -> Pocket035 [Edge3,Edge6,Edge9,Edge11,Edge12,Edge13,Edge14,Edge15,Edge16,Edge17,Edge18,Edge19,Edge20,Edge21,Edge22,Edge23,Edge24,Edge25,Edge26,Edge27,Edge28,Edge29,Edge30,Edge31,Edge32,Edge33,Edge34,Edge35,Edge37,Edge38,Edge39,Edge40,Edge41,Edge42,Edge43,Edge44,Edge45,Edge46,Edge47,Edge48,+36 more]
  BaseFeature = -> Pocket035
  Radius = 1
  Refine = true
  SupportTransform = false
  Suppressed = false
  UseAllEdges = false
FEATURE [PartDesign::Body] Body012  label="Strongway13inFrameTop"
  AllowCompound = true
  Group = -> [Sketch046,Pad017,Pocket033,Pocket034,Pocket035,Fillet025]
  Origin = -> Origin026
  Tip = -> Fillet025
FEATURE [Sketcher::SketchObject] Sketch051
  ArcFitTolerance = 1e-06
  AttachmentSupport = -> [Origin018]
  ExternalGeometry = -> [Hole009]
  ExternalTypes = [0]
  FullyConstrained = true
  MakeInternals = false
  MapMode = 5
  sketch-geometry (34):
    g0: LineSegment [constr] StartX=-25 StartY=50 StartZ=0 EndX=25 EndY=50 EndZ=0
    g1: LineSegment [constr] StartX=-25 StartY=-7.9e-15 StartZ=0 EndX=25 EndY=-7.9e-15 EndZ=0
    g2: LineSegment [constr] StartX=-25 StartY=-50 StartZ=0 EndX=25 EndY=-50 EndZ=0
    g3: GeomPoint [constr] X=-6e-16 Y=75 Z=0
    g4: GeomPoint [constr] X=-5e-16 Y=25 Z=0
    g5: GeomPoint [constr] X=-1.7e-15 Y=-25 Z=0
    g6: GeomPoint [constr] X=-1.1e-15 Y=-75 Z=0
    g7: Circle CenterX=-5e-16 CenterY=25 CenterZ=0 NormalX=0 NormalY=0 NormalZ=1 AngleXU=0 Radius=11.85
    g8: Circle CenterX=-1.7e-15 CenterY=-25 CenterZ=0 NormalX=0 NormalY=0 NormalZ=1 AngleXU=0 Radius=3.5
    g9: Circle CenterX=-1.1e-15 CenterY=-75 CenterZ=0 NormalX=0 NormalY=0 NormalZ=1 AngleXU=0 Radius=3.5
    g10: LineSegment [constr] StartX=12.5 StartY=10 StartZ=0 EndX=12.5 EndY=40 EndZ=0
    g11: LineSegment [constr] StartX=12.5 StartY=40 StartZ=0 EndX=-12.5 EndY=40 EndZ=0
    g12: LineSegment [constr] StartX=-12.5 StartY=40 StartZ=0 EndX=-12.5 EndY=10 EndZ=0
    g13: LineSegment [constr] StartX=-12.5 StartY=10 StartZ=0 EndX=12.5 EndY=10 EndZ=0
    g14: LineSegment [constr] StartX=-11.5 StartY=11 StartZ=0 EndX=11.5 EndY=11 EndZ=0
    g15: LineSegment [constr] StartX=11.5 StartY=11 StartZ=0 EndX=11.5 EndY=39 EndZ=0
    g16: LineSegment [constr] StartX=11.5 StartY=39 StartZ=0 EndX=-11.5 EndY=39 EndZ=0
    g17: LineSegment [constr] StartX=-11.5 StartY=39 StartZ=0 EndX=-11.5 EndY=11 EndZ=0
    g18: GeomPoint [constr] X=-5e-16 Y=25 Z=0
    g19: Circle CenterX=-9.5 CenterY=37 CenterZ=0 NormalX=0 NormalY=0 NormalZ=1 AngleXU=0 Radius=2
    g20: Circle CenterX=9.5 CenterY=13 CenterZ=0 NormalX=0 NormalY=0 NormalZ=1 AngleXU=0 Radius=2
    g21: LineSegment [constr] StartX=-12.5 StartY=60 StartZ=0 EndX=12.5 EndY=60 EndZ=0
    g22: LineSegment [constr] StartX=12.5 StartY=60 StartZ=0 EndX=12.5 EndY=90 EndZ=0
    g23: LineSegment [constr] StartX=12.5 StartY=90 StartZ=0 EndX=-12.5 EndY=90 EndZ=0
    g24: LineSegment [constr] StartX=-12.5 StartY=90 StartZ=0 EndX=-12.5 EndY=60 EndZ=0
    g25: GeomPoint [constr] X=-6e-16 Y=75 Z=0
    g26: LineSegment [constr] StartX=-11.5 StartY=61 StartZ=0 EndX=11.5 EndY=61 EndZ=0
    g27: LineSegment [constr] StartX=11.5 StartY=61 StartZ=0 EndX=11.5 EndY=89 EndZ=0
    g28: LineSegment [constr] StartX=11.5 StartY=89 StartZ=0 EndX=-11.5 EndY=89 EndZ=0
    g29: LineSegment [constr] StartX=-11.5 StartY=89 StartZ=0 EndX=-11.5 EndY=61 EndZ=0
    g30: GeomPoint [constr] X=-6e-16 Y=75 Z=0
    g31: Circle CenterX=-6e-16 CenterY=75 CenterZ=0 NormalX=0 NormalY=0 NormalZ=1 AngleXU=0 Radius=11.85
    g32: Circle CenterX=-9.5 CenterY=87 CenterZ=0 NormalX=0 NormalY=0 NormalZ=1 AngleXU=0 Radius=2
    g33: Circle CenterX=9.5 CenterY=63 CenterZ=0 NormalX=0 NormalY=0 NormalZ=1 AngleXU=0 Radius=2
  constraints (83):
    c: PointOnObject(g0,g-3)
    c: PointOnObject(g0,g-6)
    c: Horizontal(g0)
    c: Distance(g-4,g0) = 50
    c: PointOnObject(g1,g-3)
    c: PointOnObject(g1,g-6)
    c: Horizontal(g1)
    c: PointOnObject(g2,g-3)
    c: PointOnObject(g2,g-6)
    c: Horizontal(g2)
    c: Distance(g0,g1) = 50
    c: Distance(g1,g2) = 50
    c: Symmetric(g0,g-6,g3)
    c: Symmetric(g1,g0,g4)
    c: Symmetric(g2,g1,g5)
    c: Symmetric(g-5,g2,g6)
    c: Diameter(g7) = 23.7
    c: Coincident(g7,g4)
    c: Diameter(g8) = 7
    c: Coincident(g8,g5)
    c: Diameter(g9) = 7
    c: Coincident(g9,g6)
    c: Coincident(g10,g11)
    c: Coincident(g11,g12)
    c: Coincident(g12,g13)
    c: Coincident(g13,g10)
    c: Vertical(g10)
    c: Vertical(g12)
    c: Horizontal(g11)
    c: Horizontal(g13)
    c: Symmetric(g12,g10,g4)
    c: DistanceX(g11,g11) = 25
    c: DistanceY(g10,g10) = 30
    c: Coincident(g14,g15)
    c: Coincident(g15,g16)
    c: Coincident(g16,g17)
    c: Coincident(g17,g14)
    c: Horizontal(g14)
    c: Horizontal(g16)
    c: Vertical(g15)
    c: Vertical(g17)
    c: Symmetric(g16,g14,g18)
    c: Coincident(g18,g4)
    c: Distance(g11,g16) = 1
    c: Distance(g10,g15) = 1
    c: Diameter(g19) = 4
    c: Tangent(g19,g16)
    c: Tangent(g19,g17)
    c: Tangent(g20,g14)
    c: Tangent(g20,g15)
    c: Equal(g20,g19)
    c: Coincident(g21,g22)
    c: Coincident(g22,g23)
    c: Coincident(g23,g24)
    c: Coincident(g24,g21)
    c: Horizontal(g21)
    c: Horizontal(g23)
    c: Vertical(g22)
    c: Vertical(g24)
    c: Symmetric(g23,g21,g25)
    c: Coincident(g25,g3)
    c: Coincident(g26,g27)
    c: Coincident(g27,g28)
    c: Coincident(g28,g29)
    c: Coincident(g29,g26)
    c: Horizontal(g26)
    c: Horizontal(g28)
    c: Vertical(g27)
    c: Vertical(g29)
    c: Symmetric(g28,g26,g30)
    c: Coincident(g30,g3)
    c: Equal(g23,g11)
    c: Equal(g22,g10)
    c: Equal(g27,g15)
    c: Equal(g28,g16)
    c: Coincident(g31,g3)
    c: Equal(g31,g7)
    c: Equal(g32,g33)
    c: Equal(g33,g19)
    c: Tangent(g32,g28)
    c: Tangent(g32,g29)
    c: Tangent(g33,g26)
    c: Tangent(g27,g33)
FEATURE [PartDesign::Pocket] Pocket038
  BaseFeature = -> Hole009
  Direction = (0,0,-1)
  Length = 5
  Length2 = 5
  Profile = -> Sketch051
  ReferenceAxis = -> Sketch051 [N_Axis]
  Refine = true
  SideType = 0
  Suppressed = false
  Type = 0
  Type2 = 0
FEATURE [PartDesign::Body] Body008  label="CenterPanelTop-Ethernet2-SMA2"
  AllowCompound = true
  Group = -> [Sketch031,Binder014,Pad011,Hole009,Sketch051,Pocket038]
  Origin = -> Origin018
  Tip = -> Pocket038
FEATURE [App::Point] Origin033  label="Origin042"
  Role = Origin
FEATURE [Sketcher::SketchObject] Sketch052
  ArcFitTolerance = 1e-06
  AttachmentSupport = -> [Origin032]
  ExternalTypes = [0]
  FullyConstrained = true
  MakeInternals = false
  MapMode = 5
  sketch-geometry (50):
    g0: LineSegment StartX=-50 StartY=-25 StartZ=0 EndX=50 EndY=-25 EndZ=0
    g1: LineSegment StartX=50 StartY=-25 StartZ=0 EndX=50 EndY=25 EndZ=0
    g2: LineSegment StartX=50 StartY=25 StartZ=0 EndX=-50 EndY=25 EndZ=0
    g3: LineSegment StartX=-50 StartY=25 StartZ=0 EndX=-50 EndY=-25 EndZ=0
    g4: GeomPoint [constr] X=0 Y=0 Z=0
    g5: LineSegment [constr] StartX=-45 StartY=-20 StartZ=0 EndX=45 EndY=-20 EndZ=0
    g6: LineSegment [constr] StartX=45 StartY=-20 StartZ=0 EndX=45 EndY=20 EndZ=0
    g7: LineSegment [constr] StartX=45 StartY=20 StartZ=0 EndX=-45 EndY=20 EndZ=0
    g8: LineSegment [constr] StartX=-45 StartY=20 StartZ=0 EndX=-45 EndY=-20 EndZ=0
    g9: GeomPoint [constr] X=0 Y=0 Z=0
    g10: Circle CenterX=45 CenterY=20 CenterZ=0 NormalX=0 NormalY=0 NormalZ=1 AngleXU=0 Radius=2
    g11: Circle CenterX=45 CenterY=-20 CenterZ=0 NormalX=0 NormalY=0 NormalZ=1 AngleXU=0 Radius=2
    g12: Circle CenterX=-45 CenterY=-20 CenterZ=0 NormalX=0 NormalY=0 NormalZ=1 AngleXU=0 Radius=2
    g13: Circle CenterX=-45 CenterY=20 CenterZ=0 NormalX=0 NormalY=0 NormalZ=1 AngleXU=0 Radius=2
    g14: GeomPoint [constr] X=0 Y=25 Z=0
    g15: GeomPoint [constr] X=0 Y=-25 Z=0
    g16: LineSegment [constr] StartX=-1.5 StartY=-22 StartZ=0 EndX=-1.5 EndY=-25 EndZ=0
    g17: LineSegment [constr] StartX=-1.5 StartY=-25 StartZ=0 EndX=1.5 EndY=-25 EndZ=0
    g18: LineSegment [constr] StartX=1.5 StartY=-25 StartZ=0 EndX=1.5 EndY=-22 EndZ=0
    g19: LineSegment [constr] StartX=1.5 StartY=-22 StartZ=0 EndX=-1.5 EndY=-22 EndZ=0
    g20: LineSegment [constr] StartX=-4.5 StartY=-19 StartZ=0 EndX=-4.5 EndY=-22 EndZ=0
    g21: LineSegment [constr] StartX=-4.5 StartY=-22 StartZ=0 EndX=4.5 EndY=-22 EndZ=0
    g22: LineSegment [constr] StartX=4.5 StartY=-22 StartZ=0 EndX=4.5 EndY=-19 EndZ=0
    g23: LineSegment [constr] StartX=4.5 StartY=-19 StartZ=0 EndX=-4.5 EndY=-19 EndZ=0
    g24: GeomPoint [constr] X=0 Y=-22 Z=0
    g25: LineSegment [constr] StartX=-1.5 StartY=25 StartZ=0 EndX=-1.5 EndY=22 EndZ=0
    g26: LineSegment [constr] StartX=-1.5 StartY=22 StartZ=0 EndX=1.5 EndY=22 EndZ=0
    g27: LineSegment [constr] StartX=1.5 StartY=22 StartZ=0 EndX=1.5 EndY=25 EndZ=0
    g28: LineSegment [constr] StartX=1.5 StartY=25 StartZ=0 EndX=-1.5 EndY=25 EndZ=0
    g29: LineSegment [constr] StartX=-4.5 StartY=22 StartZ=0 EndX=-4.5 EndY=19 EndZ=0
    g30: LineSegment [constr] StartX=-4.5 StartY=19 StartZ=0 EndX=4.5 EndY=19 EndZ=0
    g31: LineSegment [constr] StartX=4.5 StartY=19 StartZ=0 EndX=4.5 EndY=22 EndZ=0
    g32: LineSegment [constr] StartX=4.5 StartY=22 StartZ=0 EndX=-4.5 EndY=22 EndZ=0
    g33: GeomPoint [constr] X=0 Y=22 Z=0
    g34: LineSegment StartX=-1.5 StartY=25 StartZ=0 EndX=1.5 EndY=25 EndZ=0
    g35: LineSegment StartX=1.5 StartY=25 StartZ=0 EndX=1.5 EndY=22 EndZ=0
    g36: LineSegment StartX=1.5 StartY=22 StartZ=0 EndX=4.5 EndY=22 EndZ=0
    g37: LineSegment StartX=4.5 StartY=22 StartZ=0 EndX=4.5 EndY=19 EndZ=0
    g38: LineSegment StartX=4.5 StartY=19 StartZ=0 EndX=-4.5 EndY=19 EndZ=0
    g39: LineSegment StartX=-4.5 StartY=19 StartZ=0 EndX=-4.5 EndY=22 EndZ=0
    g40: LineSegment StartX=-4.5 StartY=22 StartZ=0 EndX=-1.5 EndY=22 EndZ=0
    g41: LineSegment StartX=-1.5 StartY=22 StartZ=0 EndX=-1.5 EndY=25 EndZ=0
    g42: LineSegment StartX=-4.5 StartY=-19 StartZ=0 EndX=4.5 EndY=-19 EndZ=0
    g43: LineSegment StartX=4.5 StartY=-19 StartZ=0 EndX=4.5 EndY=-22 EndZ=0
    g44: LineSegment StartX=4.5 StartY=-22 StartZ=0 EndX=1.5 EndY=-22 EndZ=0
    g45: LineSegment StartX=1.5 StartY=-22 StartZ=0 EndX=1.5 EndY=-25 EndZ=0
    g46: LineSegment StartX=1.5 StartY=-25 StartZ=0 EndX=-1.5 EndY=-25 EndZ=0
    g47: LineSegment StartX=-1.5 StartY=-25 StartZ=0 EndX=-1.5 EndY=-22 EndZ=0
    g48: LineSegment StartX=-1.5 StartY=-22 StartZ=0 EndX=-4.5 EndY=-22 EndZ=0
    g49: LineSegment StartX=-4.5 StartY=-22 StartZ=0 EndX=-4.5 EndY=-19 EndZ=0
  constraints (114):
    c: Coincident(g0,g1)
    c: Coincident(g1,g2)
    c: Coincident(g2,g3)
    c: Coincident(g3,g0)
    c: Horizontal(g0)
    c: Horizontal(g2)
    c: Vertical(g1)
    c: Vertical(g3)
    c: Symmetric(g2,g0,g4)
    c: Distance(g1,g3) = 100
    c: Distance(g0,g2) = 50
    c: Coincident(g4,g-1)
    c: Coincident(g5,g6)
    c: Coincident(g6,g7)
    c: Coincident(g7,g8)
    c: Coincident(g8,g5)
    c: Horizontal(g5)
    c: Horizontal(g7)
    c: Vertical(g6)
    c: Vertical(g8)
    c: Symmetric(g7,g5,g9)
    c: Coincident(g9,g4)
    c: Distance(g1,g6) = 5
    c: Distance(g2,g7) = 5
    c: Diameter(g10) = 4
    c: Coincident(g10,g6)
    c: Coincident(g11,g5)
    c: Coincident(g12,g5)
    c: Coincident(g13,g7)
    c: Equal(g13,g12)
    c: Equal(g12,g11)
    c: Equal(g11,g10)
    c: PointOnObject(g15,g0)
    c: PointOnObject(g15,g-2)
    c: PointOnObject(g14,g2)
    c: PointOnObject(g14,g-2)
    c: Coincident(g16,g17)
    c: Coincident(g17,g18)
    c: Coincident(g18,g19)
    c: Coincident(g19,g16)
    c: Vertical(g16)
    c: Vertical(g18)
    c: Horizontal(g17)
    c: Horizontal(g19)
    c: Distance(g16,g18) = 3
    c: Distance(g17,g19) = 3
    c: Coincident(g20,g21)
    c: Coincident(g21,g22)
    c: Coincident(g22,g23)
    c: Coincident(g23,g20)
    c: Vertical(g20)
    c: Vertical(g22)
    c: Horizontal(g21)
    c: Horizontal(g23)
    c: Distance(g20,g22) = 9
    c: Distance(g21,g23) = 3
    c: Symmetric(g20,g21,g24)
    c: Symmetric(g16,g18,g24)
    c: Symmetric(g16,g17,g15)
    c: Coincident(g25,g26)
    c: Coincident(g26,g27)
    c: Coincident(g27,g28)
    c: Coincident(g28,g25)
    c: Vertical(g25)
    c: Vertical(g27)
    c: Horizontal(g26)
    c: Horizontal(g28)
    c: Distance(g25,g27) = 3
    c: Distance(g26,g28) = 3
    c: Coincident(g29,g30)
    c: Coincident(g30,g31)
    c: Coincident(g31,g32)
    c: Coincident(g32,g29)
    c: Vertical(g29)
    c: Vertical(g31)
    c: Horizontal(g30)
    c: Horizontal(g32)
    c: Distance(g29,g31) = 9
    c: Distance(g30,g32) = 3
    c: Symmetric(g29,g31,g33)
    c: Symmetric(g25,g26,g33)
    c: Symmetric(g25,g27,g14)
    c: Coincident(g34,g25)
    c: Coincident(g34,g27)
    c: Coincident(g35,g27)
    c: Coincident(g35,g26)
    c: Coincident(g36,g26)
    c: Coincident(g36,g31)
    c: Coincident(g37,g31)
    c: Coincident(g37,g30)
    c: Coincident(g38,g30)
    c: Coincident(g38,g29)
    c: Coincident(g39,g29)
    c: Coincident(g39,g29)
    c: Coincident(g40,g29)
    c: Coincident(g40,g25)
    c: Coincident(g41,g25)
    c: Coincident(g41,g25)
    c: Coincident(g42,g20)
    c: Coincident(g42,g22)
    c: Coincident(g43,g22)
    c: Coincident(g43,g21)
    c: Coincident(g44,g21)
    c: Coincident(g44,g18)
    c: Coincident(g45,g18)
    c: Coincident(g45,g17)
    c: Coincident(g46,g17)
    c: Coincident(g46,g16)
    c: Coincident(g47,g16)
    c: Coincident(g47,g16)
    c: Coincident(g48,g16)
    c: Coincident(g48,g20)
    c: Coincident(g49,g20)
    c: Coincident(g49,g20)
FEATURE [PartDesign::Pad] Pad020
  Direction = (0,0,1)
  Length = 20
  Length2 = 10
  Profile = -> Sketch052 [Edge3,Edge4,Edge1,Edge7,Edge8,Edge5,Edge6,Edge2]
  ReferenceAxis = -> Sketch052 [N_Axis]
  Refine = true
  Reversed = true
  SideType = 0
  Suppressed = false
  Type = 0
  Type2 = 0
FEATURE [PartDesign::Pocket] Pocket039
  BaseFeature = -> Pad020
  Direction = (0,0,-1)
  Length = 5
  Length2 = 5
  Profile = -> Sketch052 [Edge21,Edge20,Edge19,Edge18,Edge17,Edge24,Edge23,Edge22,Edge9,Edge10,Edge11,Edge12,Edge13,Edge14,Edge15,Edge16]
  ReferenceAxis = -> Sketch052 [N_Axis]
  Refine = true
  SideType = 0
  Suppressed = false
  Type = 1
  Type2 = 0
FEATURE [Sketcher::SketchObject] Sketch053
  ArcFitTolerance = 1e-06
  AttachmentSupport = -> [Origin032]
  ExternalGeometry = -> [Sketch052]
  ExternalTypes = [0,0,0,0]
  FullyConstrained = true
  MakeInternals = false
  MapMode = 5
  sketch-geometry (37):
    g0: LineSegment [constr] StartX=-47.5 StartY=-17.5 StartZ=0 EndX=47.5 EndY=-17.5 EndZ=0
    g1: LineSegment [constr] StartX=47.5 StartY=-17.5 StartZ=0 EndX=47.5 EndY=17.5 EndZ=0
    g2: LineSegment [constr] StartX=47.5 StartY=17.5 StartZ=0 EndX=-47.5 EndY=17.5 EndZ=0
    g3: LineSegment [constr] StartX=-47.5 StartY=17.5 StartZ=0 EndX=-47.5 EndY=-17.5 EndZ=0
    g4: GeomPoint [constr] X=0 Y=0 Z=0
    g5: LineSegment [constr] StartX=-50 StartY=25 StartZ=0 EndX=-50 EndY=15 EndZ=0
    g6: LineSegment [constr] StartX=-50 StartY=15 StartZ=0 EndX=-40 EndY=15 EndZ=0
    g7: LineSegment [constr] StartX=-40 StartY=15 StartZ=0 EndX=-40 EndY=25 EndZ=0
    g8: LineSegment [constr] StartX=-40 StartY=25 StartZ=0 EndX=-50 EndY=25 EndZ=0
    g9: LineSegment [constr] StartX=50 StartY=25 StartZ=0 EndX=40 EndY=25 EndZ=0
    g10: LineSegment [constr] StartX=40 StartY=25 StartZ=0 EndX=40 EndY=15 EndZ=0
    g11: LineSegment [constr] StartX=40 StartY=15 StartZ=0 EndX=50 EndY=15 EndZ=0
    g12: LineSegment [constr] StartX=50 StartY=15 StartZ=0 EndX=50 EndY=25 EndZ=0
    g13: LineSegment [constr] StartX=50 StartY=-25 StartZ=0 EndX=50 EndY=-15 EndZ=0
    g14: LineSegment [constr] StartX=50 StartY=-15 StartZ=0 EndX=40 EndY=-15 EndZ=0
    g15: LineSegment [constr] StartX=40 StartY=-15 StartZ=0 EndX=40 EndY=-25 EndZ=0
    g16: LineSegment [constr] StartX=40 StartY=-25 StartZ=0 EndX=50 EndY=-25 EndZ=0
    g17: LineSegment [constr] StartX=-50 StartY=-25 StartZ=0 EndX=-40 EndY=-25 EndZ=0
    g18: LineSegment [constr] StartX=-40 StartY=-25 StartZ=0 EndX=-40 EndY=-15 EndZ=0
    g19: LineSegment [constr] StartX=-40 StartY=-15 StartZ=0 EndX=-50 EndY=-15 EndZ=0
    g20: LineSegment [constr] StartX=-50 StartY=-15 StartZ=0 EndX=-50 EndY=-25 EndZ=0
    g21: LineSegment StartX=-47.5 StartY=-15 StartZ=0 EndX=-47.5 EndY=15 EndZ=0
    g22: LineSegment StartX=-47.5 StartY=15 StartZ=0 EndX=-40 EndY=15 EndZ=0
    g23: LineSegment StartX=-40 StartY=15 StartZ=0 EndX=-40 EndY=17.5 EndZ=0
    g24: LineSegment StartX=-40 StartY=17.5 StartZ=0 EndX=40 EndY=17.5 EndZ=0
    g25: LineSegment StartX=40 StartY=17.5 StartZ=0 EndX=40 EndY=15 EndZ=0
    g26: LineSegment StartX=40 StartY=15 StartZ=0 EndX=47.5 EndY=15 EndZ=0
    g27: LineSegment StartX=47.5 StartY=15 StartZ=0 EndX=47.5 EndY=-15 EndZ=0
    g28: LineSegment StartX=47.5 StartY=-15 StartZ=0 EndX=40 EndY=-15 EndZ=0
    g29: LineSegment StartX=40 StartY=-15 StartZ=0 EndX=40 EndY=-17.5 EndZ=0
    g30: LineSegment StartX=40 StartY=-17.5 StartZ=0 EndX=-40 EndY=-17.5 EndZ=0
    g31: LineSegment StartX=-40 StartY=-17.5 StartZ=0 EndX=-40 EndY=-15 EndZ=0
    g32: LineSegment StartX=-40 StartY=-15 StartZ=0 EndX=-47.5 EndY=-15 EndZ=0
    g33: LineSegment StartX=-40 StartY=-15 StartZ=0 EndX=40 EndY=-15 EndZ=0
    g34: LineSegment StartX=-16 StartY=-15 StartZ=0 EndX=-16 EndY=-17.5 EndZ=0
    g35: LineSegment StartX=-16 StartY=-15 StartZ=0 EndX=40 EndY=-15 EndZ=0
    g36: LineSegment StartX=-16 StartY=-17.5 StartZ=0 EndX=40 EndY=-17.5 EndZ=0
  constraints (98):
    c: Coincident(g0,g1)
    c: Coincident(g1,g2)
    c: Coincident(g2,g3)
    c: Coincident(g3,g0)
    c: Horizontal(g2)
    c: Vertical(g1)
    c: Vertical(g3)
    c: Symmetric(g2,g0,g4)
    c: Distance(g1,g3) = 95
    c: Distance(g0,g2) = 35
    c: Coincident(g4,g-1)
    c: Coincident(g5,g6)
    c: Coincident(g6,g7)
    c: Coincident(g7,g8)
    c: Coincident(g8,g5)
    c: Vertical(g5)
    c: Vertical(g7)
    c: Horizontal(g6)
    c: Horizontal(g8)
    c: Distance(g5,g7) = 10
    c: Distance(g6,g8) = 10
    c: Coincident(g5,g-4)
    c: Coincident(g9,g10)
    c: Coincident(g10,g11)
    c: Coincident(g11,g12)
    c: Coincident(g12,g9)
    c: Horizontal(g9)
    c: Horizontal(g11)
    c: Vertical(g10)
    c: Vertical(g12)
    c: Distance(g10,g12) = 10
    c: Distance(g9,g11) = 10
    c: Coincident(g9,g-6)
    c: Coincident(g13,g14)
    c: Coincident(g14,g15)
    c: Coincident(g15,g16)
    c: Coincident(g16,g13)
    c: Vertical(g13)
    c: Vertical(g15)
    c: Horizontal(g14)
    c: Horizontal(g16)
    c: Distance(g13,g15) = 10
    c: Distance(g14,g16) = 10
    c: Coincident(g13,g-6)
    c: Coincident(g17,g18)
    c: Coincident(g18,g19)
    c: Coincident(g19,g20)
    c: Coincident(g20,g17)
    c: Horizontal(g17)
    c: Horizontal(g19)
    c: Vertical(g18)
    c: Vertical(g20)
    c: Distance(g18,g20) = 10
    c: Distance(g17,g19) = 10
    c: Coincident(g17,g-5)
    c: PointOnObject(g21,g3)
    c: PointOnObject(g21,g19)
    c: PointOnObject(g21,g3)
    c: PointOnObject(g21,g6)
    c: Coincident(g22,g21)
    c: Coincident(g22,g6)
    c: Coincident(g23,g6)
    c: PointOnObject(g23,g7)
    c: PointOnObject(g23,g2)
    c: Coincident(g24,g23)
    c: PointOnObject(g24,g2)
    c: PointOnObject(g24,g10)
    c: Coincident(g25,g24)
    c: Coincident(g25,g10)
    c: Coincident(g26,g10)
    c: PointOnObject(g26,g1)
    c: PointOnObject(g26,g11)
    c: Coincident(g27,g26)
    c: PointOnObject(g27,g1)
    c: PointOnObject(g27,g14)
    c: Coincident(g28,g27)
    c: Coincident(g28,g14)
    c: Coincident(g29,g14)
    c: PointOnObject(g29,g15)
    c: PointOnObject(g29,g0)
    c: Coincident(g30,g29)
    c: PointOnObject(g30,g0)
    c: PointOnObject(g30,g18)
    c: Coincident(g31,g30)
    c: Coincident(g31,g18)
    c: Coincident(g32,g18)
    c: Coincident(g32,g21)
    c: Horizontal(g0)
    c: Coincident(g33,g18)
    c: Coincident(g33,g14)
    c: PointOnObject(g34,g33)
    c: PointOnObject(g34,g30)
    c: Vertical(g34)
    c: Coincident(g35,g34)
    c: Coincident(g36,g34)
    c: Coincident(g35,g14)
    c: Coincident(g36,g29)
    c: Distance(g29,g34) = 56
FEATURE [PartDesign::Pocket] Pocket040
  BaseFeature = -> Pocket039
  Direction = (0,0,-1)
  Length = 5
  Length2 = 5
  Profile = -> Sketch053 [Edge16,Edge12,Edge8,Edge7,Edge6,Edge5,Edge4,Edge3,Edge2,Edge1]
  ReferenceAxis = -> Sketch053 [N_Axis]
  Refine = true
  SideType = 0
  Suppressed = false
  Type = 1
  Type2 = 0
FEATURE [Sketcher::SketchObject] Sketch054
  ArcFitTolerance = 1e-06
  AttachmentSupport = -> [Pocket040]
  ExternalGeometry = -> [Sketch053]
  ExternalTypes = [0,0,0,0]
  FullyConstrained = true
  MakeInternals = false
  MapMode = 5
  sketch-geometry (3):
    g0: LineSegment StartX=-16 StartY=-15 StartZ=0 EndX=40 EndY=-15 EndZ=0
    g1: LineSegment StartX=-16 StartY=-17.5 StartZ=0 EndX=40 EndY=-17.5 EndZ=0
    g2: LineSegment StartX=40 StartY=-15 StartZ=0 EndX=40 EndY=-17.5 EndZ=0
  constraints (6):
    c: Coincident(g0,g-4)
    c: Coincident(g1,g-5)
    c: Coincident(g2,g0)
    c: Coincident(g2,g1)
    c: Coincident(g0,g-4)
    c: Coincident(g1,g-3)
FEATURE [PartDesign::Pad] Pad021
  BaseFeature = -> Pocket040
  Direction = (0,0,1)
  Length = 85
  Length2 = 10
  Profile = -> Sketch054
  ReferenceAxis = -> Sketch054 [N_Axis]
  Refine = true
  Reversed = true
  SideType = 0
  Suppressed = false
  Type = 0
  Type2 = 0
FEATURE [Sketcher::SketchObject] Sketch055
  ArcFitTolerance = 1e-06
  AttachmentSupport = -> [Pad021]
  ExternalGeometry = -> [Pad021]
  ExternalTypes = [0]
  FullyConstrained = true
  MakeInternals = false
  MapMode = 5
  Placement = pos=(0,-15,0) rot=(0,0.707107,0.707107;3.14159rad)
  sketch-geometry (25):
    g0: LineSegment [constr] StartX=-36.75 StartY=-81.5 StartZ=0 EndX=12.75 EndY=-81.5 EndZ=0
    g1: LineSegment [constr] StartX=12.75 StartY=-81.5 StartZ=0 EndX=12.75 EndY=-24 EndZ=0
    g2: LineSegment [constr] StartX=12.75 StartY=-24 StartZ=0 EndX=-36.75 EndY=-24 EndZ=0
    g3: LineSegment [constr] StartX=-36.75 StartY=-24 StartZ=0 EndX=-36.75 EndY=-81.5 EndZ=0
    g4: GeomPoint [constr] X=-12 Y=-52.75 Z=0
    g5: Circle CenterX=-36.75 CenterY=-24 CenterZ=0 NormalX=0 NormalY=0 NormalZ=1 AngleXU=0 Radius=1
    g6: Circle CenterX=12.75 CenterY=-24 CenterZ=0 NormalX=0 NormalY=0 NormalZ=1 AngleXU=0 Radius=1
    g7: Circle CenterX=12.75 CenterY=-81.5 CenterZ=0 NormalX=0 NormalY=0 NormalZ=1 AngleXU=0 Radius=1
    g8: Circle CenterX=-36.75 CenterY=-81.5 CenterZ=0 NormalX=0 NormalY=0 NormalZ=1 AngleXU=0 Radius=1
    g9: LineSegment StartX=7.75 StartY=-76.5 StartZ=0 EndX=7.75 EndY=-5 EndZ=0
    g10: LineSegment StartX=7.75 StartY=-5 StartZ=0 EndX=-31.75 EndY=-5 EndZ=0
    g11: LineSegment StartX=-31.75 StartY=-5 StartZ=0 EndX=-31.75 EndY=-76.5 EndZ=0
    g12: GeomPoint [constr] X=-12 Y=-52.75 Z=0
    g13: GeomPoint [constr] X=-12 Y=-85 Z=0
    g14: LineSegment [constr] StartX=-12 StartY=-85 StartZ=0 EndX=-12 EndY=0 EndZ=0
    g15: GeomPoint [constr] X=-12 Y=-81.5 Z=0
    g16: LineSegment [constr] StartX=-18 StartY=-66.5 StartZ=0 EndX=-18 EndY=-81.5 EndZ=0
    g17: LineSegment [constr] StartX=-18 StartY=-81.5 StartZ=0 EndX=-6 EndY=-81.5 EndZ=0
    g18: LineSegment [constr] StartX=-6 StartY=-81.5 StartZ=0 EndX=-6 EndY=-66.5 EndZ=0
    g19: LineSegment [constr] StartX=-6 StartY=-66.5 StartZ=0 EndX=-18 EndY=-66.5 EndZ=0
    g20: LineSegment StartX=-31.75 StartY=-76.5 StartZ=0 EndX=-18 EndY=-76.5 EndZ=0
    g21: LineSegment StartX=-18 StartY=-76.5 StartZ=0 EndX=-18 EndY=-81.5 EndZ=0
    g22: LineSegment StartX=-18 StartY=-81.5 StartZ=0 EndX=-6 EndY=-81.5 EndZ=0
    g23: LineSegment StartX=7.75 StartY=-76.5 StartZ=0 EndX=-6 EndY=-76.5 EndZ=0
    g24: LineSegment StartX=-6 StartY=-76.5 StartZ=0 EndX=-6 EndY=-81.5 EndZ=0
  constraints (61):
    c: Coincident(g0,g1)
    c: Coincident(g1,g2)
    c: Coincident(g2,g3)
    c: Coincident(g3,g0)
    c: Horizontal(g0)
    c: Horizontal(g2)
    c: Vertical(g1)
    c: Vertical(g3)
    c: Symmetric(g2,g0,g4)
    c: Distance(g1,g3) = 49.5
    c: Distance(g0,g2) = 57.5
    c: Distance(g-5,g2) = 24
    c: Diameter(g5) = 2
    c: Coincident(g5,g2)
    c: Coincident(g7,g0)
    c: Coincident(g8,g0)
    c: Equal(g6,g7)
    c: Equal(g7,g8)
    c: Equal(g8,g5)
    c: Coincident(g6,g1)
    c: Coincident(g9,g10)
    c: Coincident(g10,g11)
    c: Horizontal(g10)
    c: Vertical(g9)
    c: Vertical(g11)
    c: Coincident(g12,g4)
    c: Distance(g-5,g10) = 5
    c: Distance(g1,g9) = 5
    c: Distance(g3,g11) = 5
    c: Symmetric(g-9,g-10,g13)
    c: Coincident(g14,g13)
    c: PointOnObject(g14,g-5)
    c: Vertical(g14)
    c: PointOnObject(g4,g14)
    c: PointOnObject(g15,g0)
    c: PointOnObject(g15,g14)
    c: Coincident(g16,g17)
    c: Coincident(g17,g18)
    c: Coincident(g18,g19)
    c: Coincident(g19,g16)
    c: Vertical(g16)
    c: Vertical(g18)
    c: Horizontal(g17)
    c: Horizontal(g19)
    c: Distance(g16,g18) = 12
    c: Distance(g17,g19) = 15
    c: Symmetric(g16,g17,g15)
    c: Coincident(g20,g11)
    c: PointOnObject(g20,g16)
    c: Horizontal(g20)
    c: Coincident(g21,g20)
    c: Coincident(g21,g16)
    c: Coincident(g22,g16)
    c: Coincident(g22,g17)
    c: Coincident(g23,g9)
    c: PointOnObject(g23,g18)
    c: Horizontal(g23)
    c: Coincident(g24,g23)
    c: Coincident(g24,g17)
    c: Distance(g0,g20) = 5
    c: Distance(g0,g23) = 5
FEATURE [PartDesign::Pocket] Pocket041
  BaseFeature = -> Pad021
  Direction = (0,-1,2e-16)
  Length = 5
  Length2 = 5
  Profile = -> Sketch055
  ReferenceAxis = -> Sketch055 [N_Axis]
  Refine = true
  SideType = 0
  Suppressed = false
  Type = 2
  Type2 = 0
FEATURE [PartDesign::Hole] Hole017
  BaseFeature = -> Pocket041
  BaseProfileType = 7
  CustomThreadClearance = 0
  Depth = 25
  DepthType = 0
  Diameter = 1.6
  DrillForDepth = false
  DrillPoint = 1
  DrillPointAngle = 118
  HoleCutCountersinkAngle = 90
  HoleCutCustomValues = false
  HoleCutDepth = 0
  HoleCutDiameter = 0
  HoleCutType = 0
  ModelThread = false
  Profile = -> Sketch055 [Edge1,Edge2,Edge3,Edge4]
  Refine = true
  Suppressed = false
  Tapered = false
  TaperedAngle = 90
  ThreadClass = 0
  ThreadDepth = 25
  ThreadDepthType = 0
  ThreadDiameter = 2
  ThreadDirection = 0
  ThreadFit = 0
  ThreadSize = 6
  ThreadType = 1
  Threaded = true
  UseCustomThreadClearance = false
FEATURE [PartDesign::Pad] Pad022
  BaseFeature = -> Hole017
  Direction = (0,1,0)
  Length = 10
  Length2 = 10
  Profile = -> Pocket041 [Face37]
  Refine = true
  SideType = 0
  Suppressed = false
  Type = 3
  Type2 = 0
  UpToFace = -> Hole017 [Face24]
FEATURE [Sketcher::SketchObject] Sketch056
  ArcFitTolerance = 1e-06
  AttachmentSupport = -> [Hole017]
  ExternalGeometry = -> [Hole017]
  ExternalTypes = [0]
  FullyConstrained = true
  MakeInternals = false
  MapMode = 5
  Placement = pos=(0,-15,0) rot=(0,0.707107,0.707107;3.14159rad)
  sketch-geometry (3):
    g0: LineSegment StartX=16 StartY=-20 StartZ=0 EndX=16 EndY=0 EndZ=0
    g1: LineSegment StartX=-40 StartY=-20 StartZ=0 EndX=-40 EndY=0 EndZ=0
    g2: LineSegment StartX=-40 StartY=0 StartZ=0 EndX=16 EndY=0 EndZ=0
  constraints (8):
    c: Coincident(g0,g-5)
    c: PointOnObject(g0,g-6)
    c: Vertical(g0)
    c: Coincident(g1,g-10)
    c: PointOnObject(g1,g-6)
    c: Vertical(g1)
    c: Coincident(g2,g1)
    c: Coincident(g2,g0)
FEATURE [PartDesign::Pad] Pad023
  BaseFeature = -> Pad022
  Direction = (0,1,-2e-16)
  Length = 5
  Length2 = 4
  Profile = -> Sketch056
  ReferenceAxis = -> Sketch056 [N_Axis]
  Refine = true
  SideType = 1
  Suppressed = false
  Type = 0
  Type2 = 0
FEATURE [Sketcher::SketchObject] Sketch057
  ArcFitTolerance = 1e-06
  AttachmentSupport = -> [Pad023]
  ExternalGeometry = -> [Pad023]
  ExternalTypes = [0,0,0,0]
  FullyConstrained = true
  MakeInternals = false
  MapMode = 5
  Placement = pos=(0,-10,2.2e-15) rot=(0,0.707107,0.707107;3.14159rad)
  sketch-geometry (4):
    g0: LineSegment StartX=-47.5 StartY=0 StartZ=0 EndX=-47.5 EndY=-20 EndZ=0
    g1: LineSegment StartX=-47.5 StartY=-20 StartZ=0 EndX=47.5 EndY=-20 EndZ=0
    g2: LineSegment StartX=47.5 StartY=-20 StartZ=0 EndX=47.5 EndY=0 EndZ=0
    g3: LineSegment StartX=47.5 StartY=0 StartZ=0 EndX=-47.5 EndY=0 EndZ=0
  constraints (10):
    c: Coincident(g0,g1)
    c: Coincident(g1,g2)
    c: Coincident(g2,g3)
    c: Coincident(g3,g0)
    c: Vertical(g0)
    c: Vertical(g2)
    c: Horizontal(g1)
    c: Horizontal(g3)
    c: Coincident(g0,g-3)
    c: Coincident(g1,g-4)
FEATURE [PartDesign::Pocket] Pocket042
  BaseFeature = -> Pad023
  Direction = (0,-1,2e-16)
  Length = 5
  Length2 = 5
  Profile = -> Sketch057
  ReferenceAxis = -> Sketch057 [N_Axis]
  Refine = true
  SideType = 0
  Suppressed = false
  Type = 2
  Type2 = 0
FEATURE [Sketcher::SketchObject] Sketch058
  ArcFitTolerance = 1e-06
  AttachmentSupport = -> [Pocket042]
  ExternalGeometry = -> [Pocket042]
  ExternalTypes = [0]
  FullyConstrained = true
  MakeInternals = false
  MapMode = 5
  Placement = pos=(0,-10,2.2e-15) rot=(0,0.707107,0.707107;3.14159rad)
  sketch-geometry (4):
    g0: LineSegment StartX=-18 StartY=-81.5 StartZ=0 EndX=-18 EndY=-85 EndZ=0
    g1: LineSegment StartX=-18 StartY=-85 StartZ=0 EndX=-6 EndY=-85 EndZ=0
    g2: LineSegment StartX=-6 StartY=-85 StartZ=0 EndX=-6 EndY=-81.5 EndZ=0
    g3: LineSegment StartX=-6 StartY=-81.5 StartZ=0 EndX=-18 EndY=-81.5 EndZ=0
  constraints (11):
    c: Coincident(g0,g1)
    c: Coincident(g1,g2)
    c: Coincident(g2,g3)
    c: Coincident(g3,g0)
    c: Vertical(g0)
    c: Vertical(g2)
    c: Horizontal(g1)
    c: Horizontal(g3)
    c: Coincident(g0,g-7)
    c: PointOnObject(g1,g-13)
    c: Equal(g3,g-7)
FEATURE [PartDesign::Pocket] Pocket043
  BaseFeature = -> Pocket042
  Direction = (0,-1,2e-16)
  Length = 3
  Length2 = 5
  Profile = -> Sketch058
  ReferenceAxis = -> Sketch058 [N_Axis]
  Refine = true
  SideType = 0
  Suppressed = false
  Type = 0
  Type2 = 0
FEATURE [PartDesign::Pad] Pad024
  BaseFeature = -> Pocket043
  Direction = (0,2e-16,1)
  Length = 5
  Length2 = 10
  Profile = -> Pocket043 [Face41,Face40]
  Refine = true
  SideType = 0
  Suppressed = false
  Type = 0
  Type2 = 0
FEATURE [Sketcher::SketchObject] Sketch059
  ArcFitTolerance = 1e-06
  AttachmentSupport = -> [Pad024]
  ExternalGeometry = -> [Pad024]
  ExternalTypes = [0,0]
  FullyConstrained = true
  MakeInternals = false
  MapMode = 5
  Placement = pos=(-16,0,0) rot=(0.57735,-0.57735,-0.57735;2.0944rad)
  sketch-geometry (3):
    g0: LineSegment [constr] StartX=15 StartY=-20 StartZ=0 EndX=10 EndY=-20 EndZ=0
    g1: LineSegment StartX=10 StartY=-20 StartZ=0 EndX=15 EndY=-15 EndZ=0
    g2: LineSegment StartX=10 StartY=-20 StartZ=0 EndX=10 EndY=-15 EndZ=0
  constraints (7):
    c: Coincident(g0,g-9)
    c: PointOnObject(g0,g-8)
    c: Horizontal(g0)
    c: Coincident(g1,g0)
    c: Coincident(g1,g-7)
    c: Coincident(g2,g0)
    c: Coincident(g2,g-8)
FEATURE [PartDesign::Pocket] Pocket044
  BaseFeature = -> Pad024
  Direction = (1,0,0)
  Length = 5
  Length2 = 5
  Profile = -> Sketch059
  ReferenceAxis = -> Sketch059 [N_Axis]
  Refine = true
  SideType = 0
  Suppressed = false
  Type = 3
  Type2 = 0
  UpToFace = -> Pad024 [Face49]
FEATURE [PartDesign::Fillet] Fillet034
  Base = -> Pocket044 [Edge1,Edge2,Edge3,Edge4,Edge5,Edge6,Edge7,Edge8,Edge9,Edge10,Edge11,Edge12,Edge13,Edge14,Edge15,Edge16,Edge17,Edge18,Edge19,Edge20,Edge21,Edge22,Edge23,Edge24,Edge25,Edge26,Edge27,Edge28,Edge29,Edge30,Edge31,Edge32,Edge33,Edge34,Edge35,Edge36,Edge37,Edge38,Edge39,Edge40,+122 more]
  BaseFeature = -> Pocket044
  Radius = 0.74
  Refine = true
  SupportTransform = false
  Suppressed = false
  UseAllEdges = true
FEATURE [PartDesign::Body] Body015  label="RaspberryPiBottom"
  AllowCompound = true
  Group = -> [Sketch052,Pad020,Pocket039,Sketch053,Pocket040,Sketch054,Pad021,Sketch055,Pocket041,Hole017,Pad022,Sketch056,Pad023,Sketch057,Pocket042,Sketch058,Pocket043,Pad024,Sketch059,Pocket044,Fillet034]
  Origin = -> Origin032
  Tip = -> Fillet034
FEATURE [App::Link] RaspberryPiBottom  label="RaspberryPiBottom001"
  LinkPlacement = pos=(137.313,27.2188,0.123096) rot=(0,0,1;0rad)
  LinkedObject = -> Body015
  Placement = pos=(137.313,27.2188,0.123096) rot=(0,0,1;0rad)
FEATURE [App::Link] Connector5Way004
  LinkPlacement = pos=(132.813,57.3188,-85.6169) rot=(0,0,1;0rad)
  LinkedObject = -> <external Joints.FCStd>#Body001
  Placement = pos=(132.813,57.3188,-85.6169) rot=(0,0,1;0rad)
FEATURE [App::Link] Pole65mm
  LinkPlacement = pos=(66.8132,47.3188,-87.4169) rot=(0.57735,0.57735,0.57735;2.0944rad)
  LinkedObject = -> <external Joints.FCStd>#Body005
  Placement = pos=(66.8132,47.3188,-87.4169) rot=(0.57735,0.57735,0.57735;2.0944rad)
FEATURE [App::Link] Pole85mm001
  LinkedObject = -> <external Joints.FCStd>#Body003
FEATURE [App::Link] Pole35mm
  LinkPlacement = pos=(133.113,44.7188,-87.4169) rot=(-1,0,0;4.71239rad)
  LinkedObject = -> <external Joints.FCStd>#Body004
  Placement = pos=(133.113,44.7188,-87.4169) rot=(-1,0,0;4.71239rad)
FEATURE [App::Link] Connector5Way005
  LinkPlacement = pos=(144.913,8.7188,-88.7169) rot=(0,-1,0;4.71239rad)
  LinkedObject = -> <external Joints.FCStd>#Body001
  Placement = pos=(144.913,8.7188,-88.7169) rot=(0,-1,0;4.71239rad)
FEATURE [Assembly::AssemblyObject] Assembly
  Group = -> [Joints,Pole82mm,SwitchBoxTop,SwitchBoxBottom,Fan_Bottom,Fan_Right_Top,Connector5Way,GroundedJoint,Connector5Way001,Simulations,Simulation,Motion,Pole82mm001,Connector5Way002,Pole82mm002,Connector5Way003,Pole85mm,CenterPanelBottom,CenterPanelTop,RaspberryPiBottom,Connector5Way004,Pole65mm,Pole85mm001,Pole35mm,Connector5Way005]
  Origin = -> Origin006
  Type = Assembly
FEATURE [App::Point] Origin035  label="Origin045"
  Role = Origin
FEATURE [Sketcher::SketchObject] Sketch060
  ArcFitTolerance = 1e-06
  AttachmentSupport = -> [Origin034]
  ExternalTypes = [0]
  FullyConstrained = true
  MakeInternals = false
  MapMode = 5
  sketch-geometry (43):
    g0: LineSegment StartX=-50 StartY=-25 StartZ=0 EndX=50 EndY=-25 EndZ=0
    g1: LineSegment StartX=50 StartY=-25 StartZ=0 EndX=50 EndY=25 EndZ=0
    g2: LineSegment StartX=50 StartY=25 StartZ=0 EndX=-50 EndY=25 EndZ=0
    g3: LineSegment StartX=-50 StartY=25 StartZ=0 EndX=-50 EndY=-25 EndZ=0
    g4: GeomPoint [constr] X=0 Y=0 Z=0
    g5: LineSegment [constr] StartX=-45 StartY=-20 StartZ=0 EndX=45 EndY=-20 EndZ=0
    g6: LineSegment [constr] StartX=45 StartY=-20 StartZ=0 EndX=45 EndY=20 EndZ=0
    g7: LineSegment [constr] StartX=45 StartY=20 StartZ=0 EndX=-45 EndY=20 EndZ=0
    g8: LineSegment [constr] StartX=-45 StartY=20 StartZ=0 EndX=-45 EndY=-20 EndZ=0
    g9: GeomPoint [constr] X=0 Y=0 Z=0
    g10: Circle CenterX=-45 CenterY=20 CenterZ=0 NormalX=0 NormalY=0 NormalZ=1 AngleXU=0 Radius=2
    g11: Circle CenterX=45 CenterY=20 CenterZ=0 NormalX=0 NormalY=0 NormalZ=1 AngleXU=0 Radius=2
    g12: Circle CenterX=45 CenterY=-20 CenterZ=0 NormalX=0 NormalY=0 NormalZ=1 AngleXU=0 Radius=2
    g13: Circle CenterX=-45 CenterY=-20 CenterZ=0 NormalX=0 NormalY=0 NormalZ=1 AngleXU=0 Radius=2
    g14: LineSegment StartX=23 StartY=9 StartZ=0 EndX=23 EndY=-7 EndZ=0
    g15: LineSegment StartX=23 StartY=-7 StartZ=0 EndX=38 EndY=-7 EndZ=0
    g16: LineSegment StartX=38 StartY=-7 StartZ=0 EndX=38 EndY=9 EndZ=0
    g17: LineSegment StartX=38 StartY=9 StartZ=0 EndX=23 EndY=9 EndZ=0
    g18: LineSegment StartX=5 StartY=9 StartZ=0 EndX=5 EndY=-7 EndZ=0
    g19: LineSegment StartX=5 StartY=-7 StartZ=0 EndX=20 EndY=-7 EndZ=0
    g20: LineSegment StartX=20 StartY=-7 StartZ=0 EndX=20 EndY=9 EndZ=0
    g21: LineSegment StartX=20 StartY=9 StartZ=0 EndX=5 EndY=9 EndZ=0
    g22: GeomPoint [constr] X=12.5 Y=1 Z=0
    g23: GeomPoint [constr] X=30.5 Y=1 Z=0
    g24: LineSegment [constr] StartX=-45 StartY=-7 StartZ=0 EndX=45 EndY=-7 EndZ=0
    g25: LineSegment StartX=-14 StartY=7 StartZ=0 EndX=-14 EndY=-7 EndZ=0
    g26: LineSegment StartX=-14 StartY=-7 StartZ=0 EndX=2 EndY=-7 EndZ=0
    g27: LineSegment StartX=2 StartY=-7 StartZ=0 EndX=2 EndY=7 EndZ=0
    g28: LineSegment StartX=2 StartY=7 StartZ=0 EndX=-14 EndY=7 EndZ=0
    g29: LineSegment [constr] StartX=-42 StartY=15.5 StartZ=0 EndX=-42 EndY=-15.5 EndZ=0
    g30: LineSegment [constr] StartX=-42 StartY=-15.5 StartZ=0 EndX=-17 EndY=-15.5 EndZ=0
    g31: LineSegment [constr] StartX=-17 StartY=-15.5 StartZ=0 EndX=-17 EndY=15.5 EndZ=0
    g32: LineSegment [constr] StartX=-17 StartY=15.5 StartZ=0 EndX=-42 EndY=15.5 EndZ=0
    g33: Circle CenterX=-38.5 CenterY=12 CenterZ=0 NormalX=0 NormalY=0 NormalZ=1 AngleXU=0 Radius=2
    g34: GeomPoint [constr] X=-29.5 Y=-2e-16 Z=0
    g35: LineSegment [constr] StartX=-38.5 StartY=-12 StartZ=0 EndX=-20.5 EndY=-12 EndZ=0
    g36: LineSegment [constr] StartX=-20.5 StartY=-12 StartZ=0 EndX=-20.5 EndY=12 EndZ=0
    g37: LineSegment [constr] StartX=-20.5 StartY=12 StartZ=0 EndX=-38.5 EndY=12 EndZ=0
    g38: LineSegment [constr] StartX=-38.5 StartY=12 StartZ=0 EndX=-38.5 EndY=-12 EndZ=0
    g39: GeomPoint [constr] X=-29.5 Y=-2e-16 Z=0
    g40: Circle CenterX=-20.5 CenterY=-12 CenterZ=0 NormalX=0 NormalY=0 NormalZ=1 AngleXU=0 Radius=2
    g41: Circle CenterX=-29.5 CenterY=-2e-16 CenterZ=0 NormalX=0 NormalY=0 NormalZ=1 AngleXU=0 Radius=12
    g42: LineSegment [constr] StartX=-45 StartY=-2e-16 StartZ=0 EndX=45 EndY=-2e-16 EndZ=0
  constraints (109):
    c: Coincident(g0,g1)
    c: Coincident(g1,g2)
    c: Coincident(g2,g3)
    c: Coincident(g3,g0)
    c: Horizontal(g0)
    c: Horizontal(g2)
    c: Vertical(g1)
    c: Vertical(g3)
    c: Symmetric(g2,g0,g4)
    c: Distance(g1,g3) = 100
    c: Distance(g0,g2) = 50
    c: Coincident(g4,g-1)
    c: Coincident(g5,g6)
    c: Coincident(g6,g7)
    c: Coincident(g7,g8)
    c: Coincident(g8,g5)
    c: Horizontal(g5)
    c: Horizontal(g7)
    c: Vertical(g6)
    c: Vertical(g8)
    c: Symmetric(g7,g5,g9)
    c: Coincident(g9,g4)
    c: Distance(g2,g7) = 5
    c: Distance(g1,g6) = 5
    c: Diameter(g10) = 4
    c: Coincident(g10,g7)
    c: Coincident(g11,g6)
    c: Coincident(g12,g5)
    c: Coincident(g13,g5)
    c: Equal(g12,g11)
    c: Equal(g11,g13)
    c: Equal(g13,g10)
    c: Coincident(g14,g15)
    c: Coincident(g15,g16)
    c: Coincident(g16,g17)
    c: Coincident(g17,g14)
    c: Vertical(g14)
    c: Vertical(g16)
    c: Horizontal(g15)
    c: Horizontal(g17)
    c: Distance(g14,g16) = 15
    c: Distance(g15,g17) = 16
    c: Coincident(g18,g19)
    c: Coincident(g19,g20)
    c: Coincident(g20,g21)
    c: Coincident(g21,g18)
    c: Vertical(g18)
    c: Vertical(g20)
    c: Horizontal(g19)
    c: Horizontal(g21)
    c: Equal(g21,g17)
    c: Equal(g20,g14)
    c: Symmetric(g18,g20,g22)
    c: Symmetric(g14,g16,g23)
    c: Distance(g1,g16) = 12
    c: Distance(g14,g20) = 3
    c: PointOnObject(g24,g8)
    c: PointOnObject(g24,g6)
    c: Horizontal(g24)
    c: Distance(g0,g24) = 18
    c: PointOnObject(g15,g24)
    c: PointOnObject(g19,g24)
    c: Coincident(g25,g26)
    c: Coincident(g26,g27)
    c: Coincident(g27,g28)
    c: Coincident(g28,g25)
    c: Vertical(g25)
    c: Vertical(g27)
    c: Horizontal(g26)
    c: Horizontal(g28)
    c: Distance(g25,g27) = 16
    c: Distance(g26,g28) = 14
    c: PointOnObject(g26,g24)
    c: Distance(g18,g27) = 3
    c: Coincident(g29,g30)
    c: Coincident(g30,g31)
    c: Coincident(g31,g32)
    c: Coincident(g32,g29)
    c: Vertical(g29)
    c: Vertical(g31)
    c: Horizontal(g30)
    c: Horizontal(g32)
    c: Distance(g29,g31) = 25
    c: Distance(g30,g32) = 31
    c: Diameter(g33) = 4
    c: Symmetric(g29,g31,g34)
    c: Coincident(g35,g36)
    c: Coincident(g36,g37)
    c: Coincident(g37,g38)
    c: Coincident(g38,g35)
    c: Horizontal(g35)
    c: Horizontal(g37)
    c: Vertical(g36)
    c: Vertical(g38)
    c: Symmetric(g37,g35,g39)
    c: Coincident(g39,g34)
    c: Distance(g37,g32) = 3.5
    c: Distance(g36,g31) = 3.5
    c: Coincident(g33,g37)
    c: Coincident(g40,g35)
    c: Equal(g40,g33)
    c: Diameter(g41) = 24
    c: Coincident(g41,g34)
    c: Distance(g25,g31) = 3
    c: PointOnObject(g42,g8)
    c: PointOnObject(g42,g6)
    c: Horizontal(g42)
    c: Distance(g0,g42) = 25
    c: PointOnObject(g34,g42)
FEATURE [PartDesign::Pad] Pad025
  Direction = (0,0,1)
  Length = 3
  Length2 = 10
  Profile = -> Sketch060
  ReferenceAxis = -> Sketch060 [N_Axis]
  Refine = true
  SideType = 0
  Suppressed = false
  Type = 0
  Type2 = 0
FEATURE [PartDesign::Hole] Hole018
  BaseFeature = -> Pad025
  BaseProfileType = 7
  CustomThreadClearance = 0
  Depth = 25
  DepthType = 0
  Diameter = 4.5
  DrillForDepth = false
  DrillPoint = 1
  DrillPointAngle = 118
  HoleCutCountersinkAngle = 90
  HoleCutCustomValues = false
  HoleCutDepth = 4
  HoleCutDiameter = 8
  HoleCutType = 2
  ModelThread = false
  Profile = -> Pad025 [Edge54,Edge57,Edge60,Edge63]
  Refine = true
  Suppressed = false
  Tapered = false
  TaperedAngle = 90
  ThreadClass = 0
  ThreadDepth = 25
  ThreadDepthType = 0
  ThreadDiameter = 4
  ThreadDirection = 0
  ThreadFit = 0
  ThreadSize = 11
  ThreadType = 1
  Threaded = false
  UseCustomThreadClearance = false
FEATURE [PartDesign::Body] Body016  label="RaspberryPiTop"
  AllowCompound = true
  Group = -> [Sketch060,Pad025,Hole018]
  Origin = -> Origin034
  Tip = -> Hole018
FEATURE [Sketcher::SketchObject] Sketch061
  ArcFitTolerance = 1e-06
  AttachmentSupport = -> [Origin016]
  ExternalGeometry = -> [Sketch035]
  ExternalTypes = [0,0,0,0,0,0,0,0,0,0,0,0,0,0,0,0]
  FullyConstrained = true
  MakeInternals = false
  MapMode = 5
  sketch-geometry (12):
    g0: GeomPoint [constr] X=1.8e-15 Y=74.9 Z=0
    g1: GeomPoint [constr] X=-2.2e-15 Y=25.1 Z=0
    g2: GeomPoint [constr] X=0 Y=-24.9 Z=0
    g3: GeomPoint [constr] X=3.1e-15 Y=-74.9 Z=0
    g4: LineSegment StartX=-13.5 StartY=91.4 StartZ=0 EndX=-13.5 EndY=58.4 EndZ=0
    g5: LineSegment StartX=-13.5 StartY=58.4 StartZ=0 EndX=13.5 EndY=58.4 EndZ=0
    g6: LineSegment StartX=13.5 StartY=58.4 StartZ=0 EndX=13.5 EndY=91.4 EndZ=0
    g7: LineSegment StartX=13.5 StartY=91.4 StartZ=0 EndX=-13.5 EndY=91.4 EndZ=0
    g8: LineSegment StartX=-13.5 StartY=41.6 StartZ=0 EndX=-13.5 EndY=8.6 EndZ=0
    g9: LineSegment StartX=-13.5 StartY=8.6 StartZ=0 EndX=13.5 EndY=8.6 EndZ=0
    g10: LineSegment StartX=13.5 StartY=8.6 StartZ=0 EndX=13.5 EndY=41.6 EndZ=0
    g11: LineSegment StartX=13.5 StartY=41.6 StartZ=0 EndX=-13.5 EndY=41.6 EndZ=0
  constraints (26):
    c: Symmetric(g-18,g-16,g3)
    c: Symmetric(g-14,g-12,g2)
    c: Symmetric(g-9,g-10,g1)
    c: Symmetric(g-6,g-5,g0)
    c: Coincident(g4,g5)
    c: Coincident(g5,g6)
    c: Coincident(g6,g7)
    c: Coincident(g7,g4)
    c: Vertical(g4)
    c: Vertical(g6)
    c: Horizontal(g5)
    c: Horizontal(g7)
    c: Distance(g4,g6) = 27
    c: Distance(g5,g7) = 33
    c: Coincident(g8,g9)
    c: Coincident(g9,g10)
    c: Coincident(g10,g11)
    c: Coincident(g11,g8)
    c: Vertical(g8)
    c: Vertical(g10)
    c: Horizontal(g9)
    c: Horizontal(g11)
    c: Equal(g11,g5)
    c: Equal(g10,g6)
    c: Symmetric(g4,g6,g0)
    c: Symmetric(g8,g10,g1)
FEATURE [PartDesign::Pocket] Pocket045
  BaseFeature = -> Hole010
  Direction = (0,0,-1)
  Length = 5
  Length2 = 5
  Profile = -> Sketch061
  ReferenceAxis = -> Sketch061 [N_Axis]
  Refine = true
  SideType = 0
  Suppressed = false
  Type = 1
  Type2 = 0
FEATURE [PartDesign::Fillet] Fillet035
  Base = -> Pocket045 [Edge1,Edge2,Edge3,Edge4,Edge5,Edge6,Edge7,Edge8,Edge9,Edge10,Edge11,Edge12,Edge13,Edge14,Edge15,Edge16,Edge17,Edge18,Edge19,Edge20,Edge21,Edge22,Edge23,Edge24,Edge25,Edge26,Edge27,Edge28,Edge29,Edge30,Edge31,Edge32,Edge33,Edge34,Edge35,Edge36,Edge37,Edge38,Edge39,Edge40,+236 more]
  BaseFeature = -> Pocket045
  Radius = 1
  Refine = true
  SupportTransform = false
  Suppressed = false
  UseAllEdges = true
FEATURE [PartDesign::Body] Body007  label="CenterPanelBottom"
  AllowCompound = true
  Group = -> [Binder012,Sketch032,Pad012,Sketch033,Pocket023,Sketch034,Pocket024,Sketch035,Pocket025,Hole010,Sketch061,Pocket045,Fillet035]
  Origin = -> Origin016
  Tip = -> Fillet035
FEATURE [PartDesign::Hole] Hole019
  BaseFeature = -> Pad006
  BaseProfileType = 7
  CustomThreadClearance = 0
  Depth = 25
  DepthType = 0
  Diameter = 4.5
  DrillForDepth = false
  DrillPoint = 1
  DrillPointAngle = 118
  HoleCutCountersinkAngle = 90
  HoleCutCustomValues = false
  HoleCutDepth = 4
  HoleCutDiameter = 8
  HoleCutType = 2
  ModelThread = false
  Profile = -> Pad006 [Edge27,Edge33,Edge30,Edge36]
  Refine = true
  Suppressed = false
  Tapered = false
  TaperedAngle = 90
  ThreadClass = 0
  ThreadDepth = 25
  ThreadDepthType = 0
  ThreadDiameter = 4
  ThreadDirection = 0
  ThreadFit = 0
  ThreadSize = 11
  ThreadType = 1
  Threaded = false
  UseCustomThreadClearance = false
FEATURE [PartDesign::Fillet] Fillet036
  Base = -> Hole019 [Edge22,Edge23,Edge25,Edge26,Edge12,Edge15,Edge19,Edge18,Edge13,Edge14,Edge16,Edge17]
  BaseFeature = -> Hole019
  Radius = 1
  Refine = true
  SupportTransform = false
  Suppressed = false
  UseAllEdges = false
FEATURE [PartDesign::Body] Body004  label="SwitchBoxTop"
  AllowCompound = true
  Group = -> [Binder009,Sketch017,Pad006,Hole019,Fillet036]
  Origin = -> Origin010
  Tip = -> Fillet036

RESOLVED EXTERNAL PARTS (link-assembly join: the EXTERNAL_REF files above that resolve inside this repo's crawl, each included once):
---- part Joints.FCStd = doc fcstd_34421f11bd4d (114591 chars; too large to inline — full recipe in that document) ----
